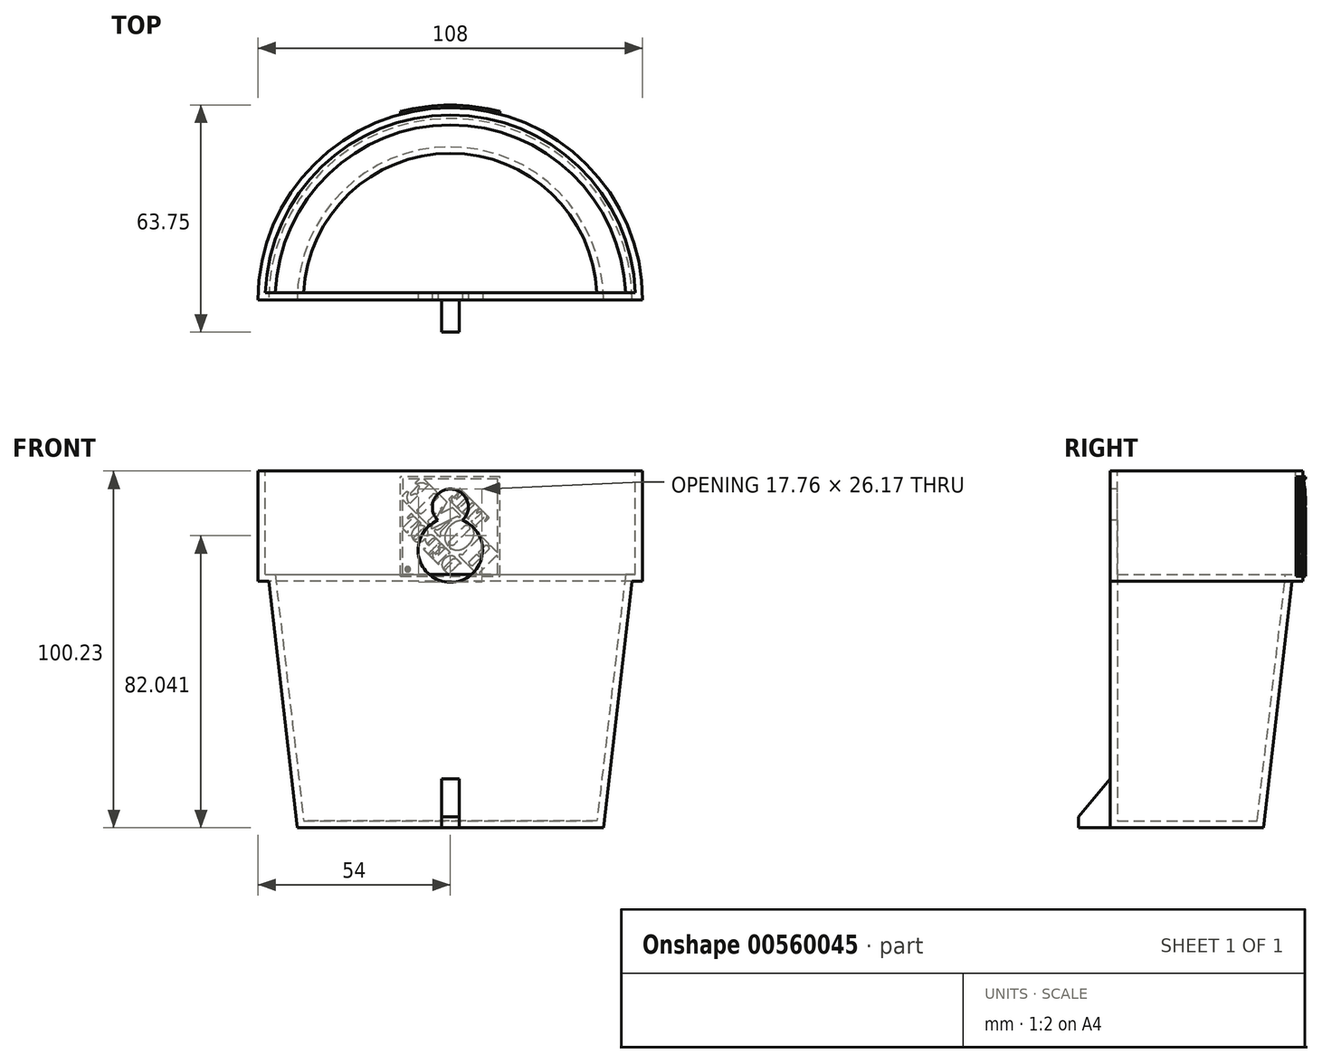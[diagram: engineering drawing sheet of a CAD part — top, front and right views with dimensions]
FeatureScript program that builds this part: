
annotation { "Feature Type Name" : "Feature", "Feature Type Description" : "" }
export const myFeature = defineFeature(function(context is Context, id is Id, definition is map)
    precondition{}
    {
        {
            var Q0;
            Q0=qCreatedBy(makeId("Front.planeOp"),FACE);
            var sketch = newSketch(context, id + "F0", { "sketchPlane" : qUnion([Q0])});
            skLineSegment(sketch, "E0", {"start": v(0, 77.42) * mm, "end": v(-54, 77.42) * mm});
            skLineSegment(sketch, "E1", {"start": v(-54, 77.42) * mm, "end": v(-54, 46.42) * mm});
            skLineSegment(sketch, "E2", {"start": v(0, -22.8) * mm, "end": v(-43, -22.8) * mm});
            skLineSegment(sketch, "E3", {"start": v(-54, 46.42) * mm, "end": v(-51, 46.42) * mm});
            skLineSegment(sketch, "E4", {"start": v(0, 77.42) * mm, "end": v(0, -22.8) * mm});
            skLineSegment(sketch, "E5", {"start": v(-51, 46.42) * mm, "end": v(-43, -22.8) * mm});
            skLineSegment(sketch, "E6.MirrorCS", {"start": v(0, 77.42) * mm, "end": v(54, 77.42) * mm});
            skLineSegment(sketch, "E7.MirrorCS", {"start": v(54, 77.42) * mm, "end": v(54, 46.42) * mm});
            skLineSegment(sketch, "E8.MirrorCS", {"start": v(54, 46.42) * mm, "end": v(51, 46.42) * mm});
            skLineSegment(sketch, "E9.MirrorCS", {"start": v(51, 46.42) * mm, "end": v(43, -22.8) * mm});
            skLineSegment(sketch, "E10.MirrorCS", {"start": v(0, -22.8) * mm, "end": v(43, -22.8) * mm});
            skSolve(sketch);
        }
        {
            var Q0;
            {var subQ0=sQuery(id+"F0.wireOp",EDGE,"E3");Q0=makeQuery(id+"F0.imprint","IMPRINT",FACE,{"disambiguationData":[TD([[makeQuery(id+"F0.imprint","IMPRINT",EDGE,{"derivedFrom":subQ0}),1.0]])]});}
            var Q1;
            {var subQ1=sQuery(id+"F0.wireOp",EDGE,"E0");Q1=makeQuery(id+"F0.imprint","IMPRINT",FACE,{"disambiguationData":[TD([[makeQuery(id+"F0.imprint","IMPRINT",EDGE,{"derivedFrom":subQ1}),1.0]])]});}
            var Q2;
            Q2=makeQuery(id+"F0.imprint","IMPRINT",FACE,{"disambiguationData":[TD([[makeQuery(id+"F0.imprint","IMPRINT",EDGE,{"derivedFrom":sQuery(id+"F0.wireOp",EDGE,"Kfnrekvc-ZjTY-c2iQ-cK4z-hKnBe4uEAVNk")}),1.0]])]});
            var Q3;
            Q3=sQuery(id+"F0.wireOp",EDGE,"E4");
            revolve(context, id + "F1", {"entities" : qUnion([Q0, Q1, Q2]), "axis" : qUnion([Q3]), "revolveType" : RevolveType.ONE_DIRECTION, "angle" : 180 * degree});
        }
        {
            var Q0;
            Q0=makeQuery(id+"FK2OT3XlAi37Aaq_1.splitOp","SPLIT",FACE,{"derivedFrom":makeQuery(id+"F1.opRevolve","SWEPT_FACE",FACE,{"disambiguationData":[OSD([sQuery(id+"F0.wireOp",EDGE,"E0")])]}),"isFromBackBody":true});
            shell(context, id + "F2", {"entities" : qUnion([Q0]), "thickness" : 2 * mm});
        }
        {
            var Q0;
            Q0=qCreatedBy(makeId("Front.planeOp"),FACE);
            var sketch = newSketch(context, id + "F3", { "sketchPlane" : qUnion([Q0])});
            skLineSegment(sketch, "E11.bottom", {"start": v(-2.5, -7.8) * mm, "end": v(2.5, -7.8) * mm});
            skLineSegment(sketch, "E11.top", {"start": v(-2.5, -22.8) * mm, "end": v(2.5, -22.8) * mm});
            skLineSegment(sketch, "E11.left", {"start": v(-2.5, -7.8) * mm, "end": v(-2.5, -22.8) * mm});
            skLineSegment(sketch, "E11.right", {"start": v(2.5, -7.8) * mm, "end": v(2.5, -22.8) * mm});
            skPoint(sketch, "E11.middle", {"position": v(0, -15.3) * mm});
            skSolve(sketch);
        }
        {
            var Q0;
            Q0=qSketchRegion(id+"F3",true);
            extrude(context, id + "F4", {"entities" : qUnion([Q0]), "operationType" : NewBodyOperationType.ADD, "depth" : 9 * mm});
        }
        {
            var Q0;
            Q0=qCreatedBy(makeId("Front.planeOp"),FACE);
            var sketch = newSketch(context, id + "F5", { "sketchPlane" : qUnion([Q0])});
            skCircle(sketch, "E12", {"center": v(0, 67.27) * mm, "radius": 5.05 * mm});
            skCircle(sketch, "E13", {"center": v(0, 55.2) * mm, "radius": 9.05 * mm});
            skSolve(sketch);
        }
        {
            var Q0;
            {var subQ0=sQuery(id+"F5.wireOp",EDGE,"E13");var subQ1=sQuery(id+"F5.wireOp",EDGE,"E12");var subQ2=makeQuery(id+"F5.imprint","INTERSECT",VERTEX,{"disambiguationData":[OD(0.0)],"derivedFrom":[subQ1,subQ0]});Q0=makeQuery(id+"F5.imprint","IMPRINT",FACE,{"disambiguationData":[TD([[makeQuery(id+"F5.imprint","IMPRINT",EDGE,{"disambiguationData":[TD([[subQ2,1.0]])],"derivedFrom":subQ1}),1.0]])]});}
            var Q1;
            {var subQ0=sQuery(id+"F5.wireOp",EDGE,"E13");var subQ1=sQuery(id+"F5.wireOp",EDGE,"E12");var subQ2=makeQuery(id+"F5.imprint","INTERSECT",VERTEX,{"disambiguationData":[OD(0.0)],"derivedFrom":[subQ1,subQ0]});Q1=makeQuery(id+"F5.imprint","IMPRINT",FACE,{"disambiguationData":[TD([[makeQuery(id+"F5.imprint","IMPRINT",EDGE,{"disambiguationData":[TD([[subQ2,-1.0]])],"derivedFrom":subQ1}),-1.0]])]});}
            var Q2;
            {var subQ0=sQuery(id+"F5.wireOp",EDGE,"E13");var subQ1=sQuery(id+"F5.wireOp",EDGE,"E12");var subQ2=makeQuery(id+"F5.imprint","INTERSECT",VERTEX,{"disambiguationData":[OD(0.0)],"derivedFrom":[subQ1,subQ0]});Q2=makeQuery(id+"F5.imprint","IMPRINT",FACE,{"disambiguationData":[TD([[makeQuery(id+"F5.imprint","IMPRINT",EDGE,{"disambiguationData":[TD([[subQ2,-1.0]])],"derivedFrom":subQ1}),1.0]])]});}
            var Q3;
            Q3=sQuery(id+"F5.wireOp",EDGE,"E12");
            var Q4;
            Q4=sQuery(id+"F5.wireOp",EDGE,"E13");
            extrude(context, id + "F6", {"entities" : qUnion([Q0, Q1, Q2]), "operationType" : NewBodyOperationType.REMOVE, "surfaceEntities" : qUnion([Q3, Q4]), "oppositeDirection" : true, "depth" : 10 * mm});
        }
        {
            var Q0;
            Q0=makeQuery(id+"F4.opExtrude","CAP_EDGE",EDGE,{"disambiguationData":[OSD([sQuery(id+"F3.wireOp",EDGE,"E11.bottom")])],"isStart":false});
            chamfer(context, id + "F7", {"entities" : qUnion([Q0]), "chamferType" : ChamferType.OFFSET_ANGLE, "width" : 10 * mm, "oppositeDirection" : false, "angle" : 50 * degree, "tangentPropagation" : true});
        }
        {
            var Q0;
            Q0=makeQuery(id+"F1.opRevolve","SWEPT_BODY",BODY,{"disambiguationData":[OSD([sQuery(id+"F0.wireOp",EDGE,"E0"),sQuery(id+"F0.wireOp",EDGE,"E1"),sQuery(id+"F0.wireOp",EDGE,"E2"),sQuery(id+"F0.wireOp",EDGE,"E3"),sQuery(id+"F0.wireOp",EDGE,"E4"),sQuery(id+"F0.wireOp",EDGE,"E5")])]});
            transform(context, id + "F8", {"entities" : qUnion([Q0]), "transformType" : TransformType.TRANSLATION_3D, "dx" : 0 * mm, "dy" : 0 * mm, "dz" : -7 * mm, "makeCopy" : false});
        }
        {
            var Q0;
            Q0=makeQuery(id+"F2.opShell","OFFSET_FACE",FACE,{"disambiguationData":[OSD([sQuery(id+"F0.wireOp",EDGE,"E0"),sQuery(id+"F0.wireOp",EDGE,"E1"),sQuery(id+"F0.wireOp",EDGE,"E2"),sQuery(id+"F0.wireOp",EDGE,"E3"),sQuery(id+"F0.wireOp",EDGE,"E4"),sQuery(id+"F0.wireOp",EDGE,"E5")])]});
            cPlane(context, id + "F9", {"entities" : qUnion([Q0]), "cplaneType" : CPlaneType.OFFSET, "offset" : 80 * mm, "width" : 150 * mm, "height" : 150 * mm});
        }
        {
            var Q0;
            Q0=qCreatedBy(id+"F9.planeOp",FACE);
            var sketch = newSketch(context, id + "F10", { "sketchPlane" : qUnion([Q0])});
            skLineSegment(sketch, "E14", {"start": v(0.66, 41.55) * mm, "end": v(0.66, 41.55) * mm});
            skLineSegment(sketch, "E15", {"start": v(0.66, 41.55) * mm, "end": v(0.66, 41.54) * mm});
            skLineSegment(sketch, "E16", {"start": v(0.66, 41.54) * mm, "end": v(0.66, 41.55) * mm});
            skLineSegment(sketch, "E17", {"start": v(11.7, 43.25) * mm, "end": v(11.7, 42.39) * mm});
            skLineSegment(sketch, "E18", {"start": v(11.7, 42.39) * mm, "end": v(11.82, 42.39) * mm});
            skLineSegment(sketch, "E19", {"start": v(11.82, 42.39) * mm, "end": v(11.82, 42.76) * mm});
            skLineSegment(sketch, "E20", {"start": v(11.82, 42.76) * mm, "end": v(11.97, 42.76) * mm});
            skLineSegment(sketch, "E21", {"start": v(11.97, 42.76) * mm, "end": v(12.05, 42.63) * mm});
            skLineSegment(sketch, "E22", {"start": v(12.05, 42.63) * mm, "end": v(12.07, 42.6) * mm});
            skLineSegment(sketch, "E23", {"start": v(12.07, 42.6) * mm, "end": v(12.2, 42.4) * mm});
            skLineSegment(sketch, "E24", {"start": v(12.2, 42.4) * mm, "end": v(12.34, 42.39) * mm});
            skLineSegment(sketch, "E25", {"start": v(12.34, 42.39) * mm, "end": v(12.34, 42.4) * mm});
            skLineSegment(sketch, "E26", {"start": v(12.34, 42.4) * mm, "end": v(12.32, 42.42) * mm});
            skLineSegment(sketch, "E27", {"start": v(12.32, 42.42) * mm, "end": v(12.3, 42.45) * mm});
            skLineSegment(sketch, "E28", {"start": v(12.3, 42.45) * mm, "end": v(12.14, 42.7) * mm});
            skLineSegment(sketch, "E29", {"start": v(12.14, 42.7) * mm, "end": v(12.12, 42.73) * mm});
            skLineSegment(sketch, "E30", {"start": v(12.12, 42.73) * mm, "end": v(12.1, 42.76) * mm});
            skLineSegment(sketch, "E31", {"start": v(12.1, 42.76) * mm, "end": v(12.1, 42.77) * mm});
            skLineSegment(sketch, "E32", {"start": v(12.1, 42.77) * mm, "end": v(12.12, 42.77) * mm});
            skLineSegment(sketch, "E33", {"start": v(12.12, 42.77) * mm, "end": v(12.17, 42.78) * mm});
            skLineSegment(sketch, "E34", {"start": v(12.17, 42.78) * mm, "end": v(12.2, 42.8) * mm});
            skLineSegment(sketch, "E35", {"start": v(12.2, 42.8) * mm, "end": v(12.23, 42.82) * mm});
            skLineSegment(sketch, "E36", {"start": v(12.23, 42.82) * mm, "end": v(12.26, 42.84) * mm});
            skLineSegment(sketch, "E37", {"start": v(12.26, 42.84) * mm, "end": v(12.3, 42.87) * mm});
            skLineSegment(sketch, "E38", {"start": v(12.3, 42.87) * mm, "end": v(12.3, 42.9) * mm});
            skLineSegment(sketch, "E39", {"start": v(12.3, 42.9) * mm, "end": v(12.32, 42.95) * mm});
            skLineSegment(sketch, "E40", {"start": v(12.32, 42.95) * mm, "end": v(12.32, 43) * mm});
            skLineSegment(sketch, "E41", {"start": v(12.32, 43) * mm, "end": v(12.32, 43.06) * mm});
            skLineSegment(sketch, "E42", {"start": v(12.32, 43.06) * mm, "end": v(12.31, 43.1) * mm});
            skLineSegment(sketch, "E43", {"start": v(12.31, 43.1) * mm, "end": v(12.3, 43.13) * mm});
            skLineSegment(sketch, "E44", {"start": v(12.3, 43.13) * mm, "end": v(12.28, 43.16) * mm});
            skLineSegment(sketch, "E45", {"start": v(12.28, 43.16) * mm, "end": v(12.26, 43.18) * mm});
            skLineSegment(sketch, "E46", {"start": v(12.26, 43.18) * mm, "end": v(12.23, 43.2) * mm});
            skLineSegment(sketch, "E47", {"start": v(12.23, 43.2) * mm, "end": v(12.2, 43.22) * mm});
            skLineSegment(sketch, "E48", {"start": v(12.2, 43.22) * mm, "end": v(12.15, 43.23) * mm});
            skLineSegment(sketch, "E49", {"start": v(12.15, 43.23) * mm, "end": v(12.1, 43.25) * mm});
            skLineSegment(sketch, "E50", {"start": v(12.1, 43.25) * mm, "end": v(11.7, 43.25) * mm});
            skLineSegment(sketch, "E51", {"start": v(12.1, 42.2) * mm, "end": v(12.16, 42.22) * mm});
            skLineSegment(sketch, "E52", {"start": v(12.16, 42.22) * mm, "end": v(12.2, 42.24) * mm});
            skLineSegment(sketch, "E53", {"start": v(12.2, 42.24) * mm, "end": v(12.28, 42.27) * mm});
            skLineSegment(sketch, "E54", {"start": v(12.28, 42.27) * mm, "end": v(12.35, 42.31) * mm});
            skLineSegment(sketch, "E55", {"start": v(12.35, 42.31) * mm, "end": v(12.37, 42.32) * mm});
            skLineSegment(sketch, "E56", {"start": v(12.37, 42.32) * mm, "end": v(12.37, 42.33) * mm});
            skLineSegment(sketch, "E57", {"start": v(12.37, 42.33) * mm, "end": v(12.4, 42.37) * mm});
            skLineSegment(sketch, "E58", {"start": v(12.4, 42.37) * mm, "end": v(12.47, 42.43) * mm});
            skLineSegment(sketch, "E59", {"start": v(12.47, 42.43) * mm, "end": v(12.48, 42.45) * mm});
            skLineSegment(sketch, "E60", {"start": v(12.48, 42.45) * mm, "end": v(12.48, 42.45) * mm});
            skLineSegment(sketch, "E61", {"start": v(12.48, 42.45) * mm, "end": v(12.49, 42.46) * mm});
            skLineSegment(sketch, "E62", {"start": v(12.49, 42.46) * mm, "end": v(12.55, 42.57) * mm});
            skLineSegment(sketch, "E63", {"start": v(12.55, 42.57) * mm, "end": v(12.55, 42.58) * mm});
            skLineSegment(sketch, "E64", {"start": v(12.55, 42.58) * mm, "end": v(12.56, 42.61) * mm});
            skLineSegment(sketch, "E65", {"start": v(12.56, 42.61) * mm, "end": v(12.57, 42.66) * mm});
            skLineSegment(sketch, "E66", {"start": v(12.57, 42.66) * mm, "end": v(12.58, 42.7) * mm});
            skLineSegment(sketch, "E67", {"start": v(12.58, 42.7) * mm, "end": v(12.59, 42.8) * mm});
            skLineSegment(sketch, "E68", {"start": v(12.59, 42.8) * mm, "end": v(12.58, 42.9) * mm});
            skLineSegment(sketch, "E69", {"start": v(12.58, 42.9) * mm, "end": v(12.58, 42.95) * mm});
            skLineSegment(sketch, "E70", {"start": v(12.58, 42.95) * mm, "end": v(12.57, 43) * mm});
            skLineSegment(sketch, "E71", {"start": v(12.57, 43) * mm, "end": v(12.54, 43.06) * mm});
            skLineSegment(sketch, "E72", {"start": v(12.54, 43.06) * mm, "end": v(12.51, 43.13) * mm});
            skLineSegment(sketch, "E73", {"start": v(12.51, 43.13) * mm, "end": v(12.47, 43.2) * mm});
            skLineSegment(sketch, "E74", {"start": v(12.47, 43.2) * mm, "end": v(12.43, 43.25) * mm});
            skLineSegment(sketch, "E75", {"start": v(12.43, 43.25) * mm, "end": v(12.37, 43.3) * mm});
            skLineSegment(sketch, "E76", {"start": v(12.37, 43.3) * mm, "end": v(12.31, 43.34) * mm});
            skLineSegment(sketch, "E77", {"start": v(12.31, 43.34) * mm, "end": v(12.25, 43.38) * mm});
            skLineSegment(sketch, "E78", {"start": v(12.25, 43.38) * mm, "end": v(12.18, 43.4) * mm});
            skLineSegment(sketch, "E79", {"start": v(12.18, 43.4) * mm, "end": v(12.13, 43.43) * mm});
            skLineSegment(sketch, "E80", {"start": v(12.13, 43.43) * mm, "end": v(12.07, 43.44) * mm});
            skLineSegment(sketch, "E81", {"start": v(12.07, 43.44) * mm, "end": v(12, 43.44) * mm});
            skLineSegment(sketch, "E82", {"start": v(12, 43.44) * mm, "end": v(11.95, 43.44) * mm});
            skLineSegment(sketch, "E83", {"start": v(11.95, 43.44) * mm, "end": v(11.89, 43.44) * mm});
            skLineSegment(sketch, "E84", {"start": v(11.89, 43.44) * mm, "end": v(11.83, 43.43) * mm});
            skLineSegment(sketch, "E85", {"start": v(11.83, 43.43) * mm, "end": v(11.78, 43.41) * mm});
            skLineSegment(sketch, "E86", {"start": v(11.78, 43.41) * mm, "end": v(11.72, 43.39) * mm});
            skLineSegment(sketch, "E87", {"start": v(11.72, 43.39) * mm, "end": v(11.68, 43.37) * mm});
            skLineSegment(sketch, "E88", {"start": v(11.68, 43.37) * mm, "end": v(11.67, 43.37) * mm});
            skLineSegment(sketch, "E89", {"start": v(11.67, 43.37) * mm, "end": v(11.67, 43.37) * mm});
            skLineSegment(sketch, "E90", {"start": v(11.67, 43.37) * mm, "end": v(11.64, 43.34) * mm});
            skLineSegment(sketch, "E91", {"start": v(11.64, 43.34) * mm, "end": v(11.6, 43.31) * mm});
            skLineSegment(sketch, "E92", {"start": v(11.6, 43.31) * mm, "end": v(11.56, 43.28) * mm});
            skLineSegment(sketch, "E93", {"start": v(11.56, 43.28) * mm, "end": v(11.53, 43.25) * mm});
            skLineSegment(sketch, "E94", {"start": v(11.53, 43.25) * mm, "end": v(11.5, 43.21) * mm});
            skLineSegment(sketch, "E95", {"start": v(11.5, 43.21) * mm, "end": v(11.47, 43.17) * mm});
            skLineSegment(sketch, "E96", {"start": v(11.47, 43.17) * mm, "end": v(11.45, 43.13) * mm});
            skLineSegment(sketch, "E97", {"start": v(11.45, 43.13) * mm, "end": v(11.42, 43.09) * mm});
            skLineSegment(sketch, "E98", {"start": v(11.42, 43.09) * mm, "end": v(11.4, 43.04) * mm});
            skLineSegment(sketch, "E99", {"start": v(11.4, 43.04) * mm, "end": v(11.4, 43) * mm});
            skLineSegment(sketch, "E100", {"start": v(11.4, 43) * mm, "end": v(11.38, 42.95) * mm});
            skLineSegment(sketch, "E101", {"start": v(11.38, 42.95) * mm, "end": v(11.37, 42.9) * mm});
            skLineSegment(sketch, "E102", {"start": v(11.37, 42.9) * mm, "end": v(11.37, 42.85) * mm});
            skLineSegment(sketch, "E103", {"start": v(11.37, 42.85) * mm, "end": v(11.37, 42.8) * mm});
            skLineSegment(sketch, "E104", {"start": v(11.37, 42.8) * mm, "end": v(11.37, 42.75) * mm});
            skLineSegment(sketch, "E105", {"start": v(11.37, 42.75) * mm, "end": v(11.38, 42.7) * mm});
            skLineSegment(sketch, "E106", {"start": v(11.38, 42.7) * mm, "end": v(11.39, 42.65) * mm});
            skLineSegment(sketch, "E107", {"start": v(11.39, 42.65) * mm, "end": v(11.4, 42.6) * mm});
            skLineSegment(sketch, "E108", {"start": v(11.4, 42.6) * mm, "end": v(11.43, 42.53) * mm});
            skLineSegment(sketch, "E109", {"start": v(11.43, 42.53) * mm, "end": v(11.46, 42.48) * mm});
            skLineSegment(sketch, "E110", {"start": v(11.46, 42.48) * mm, "end": v(11.5, 42.43) * mm});
            skLineSegment(sketch, "E111", {"start": v(11.5, 42.43) * mm, "end": v(11.53, 42.39) * mm});
            skLineSegment(sketch, "E112", {"start": v(11.53, 42.39) * mm, "end": v(11.58, 42.34) * mm});
            skLineSegment(sketch, "E113", {"start": v(11.58, 42.34) * mm, "end": v(11.62, 42.3) * mm});
            skLineSegment(sketch, "E114", {"start": v(11.62, 42.3) * mm, "end": v(11.68, 42.27) * mm});
            skLineSegment(sketch, "E115", {"start": v(11.68, 42.27) * mm, "end": v(11.72, 42.25) * mm});
            skLineSegment(sketch, "E116", {"start": v(11.72, 42.25) * mm, "end": v(11.77, 42.23) * mm});
            skLineSegment(sketch, "E117", {"start": v(11.77, 42.23) * mm, "end": v(11.82, 42.21) * mm});
            skLineSegment(sketch, "E118", {"start": v(11.82, 42.21) * mm, "end": v(11.86, 42.2) * mm});
            skLineSegment(sketch, "E119", {"start": v(11.86, 42.2) * mm, "end": v(11.92, 42.2) * mm});
            skLineSegment(sketch, "E120", {"start": v(11.92, 42.2) * mm, "end": v(11.99, 42.2) * mm});
            skLineSegment(sketch, "E121", {"start": v(11.99, 42.2) * mm, "end": v(12.05, 42.2) * mm});
            skLineSegment(sketch, "E122", {"start": v(12.05, 42.2) * mm, "end": v(12.1, 42.2) * mm});
            skLineSegment(sketch, "E123", {"start": v(11.82, 42.87) * mm, "end": v(12.09, 42.88) * mm});
            skLineSegment(sketch, "E124", {"start": v(12.09, 42.88) * mm, "end": v(12.1, 42.88) * mm});
            skLineSegment(sketch, "E125", {"start": v(12.1, 42.88) * mm, "end": v(12.14, 42.9) * mm});
            skLineSegment(sketch, "E126", {"start": v(12.14, 42.9) * mm, "end": v(12.16, 42.91) * mm});
            skLineSegment(sketch, "E127", {"start": v(12.16, 42.91) * mm, "end": v(12.17, 42.93) * mm});
            skLineSegment(sketch, "E128", {"start": v(12.17, 42.93) * mm, "end": v(12.18, 42.97) * mm});
            skLineSegment(sketch, "E129", {"start": v(12.18, 42.97) * mm, "end": v(12.19, 43.01) * mm});
            skLineSegment(sketch, "E130", {"start": v(12.19, 43.01) * mm, "end": v(12.18, 43.05) * mm});
            skLineSegment(sketch, "E131", {"start": v(12.18, 43.05) * mm, "end": v(12.17, 43.08) * mm});
            skLineSegment(sketch, "E132", {"start": v(12.17, 43.08) * mm, "end": v(12.14, 43.1) * mm});
            skLineSegment(sketch, "E133", {"start": v(12.14, 43.1) * mm, "end": v(12.11, 43.13) * mm});
            skLineSegment(sketch, "E134", {"start": v(12.11, 43.13) * mm, "end": v(12.09, 43.14) * mm});
            skLineSegment(sketch, "E135", {"start": v(12.09, 43.14) * mm, "end": v(11.82, 43.14) * mm});
            skLineSegment(sketch, "E136", {"start": v(11.82, 43.14) * mm, "end": v(11.82, 42.87) * mm});
            skLineSegment(sketch, "E137", {"start": v(11.82, 42.87) * mm, "end": v(11.82, 42.87) * mm});
            skLineSegment(sketch, "E138", {"start": v(1.57, 42.94) * mm, "end": v(1.82, 42.7) * mm});
            skLineSegment(sketch, "E139", {"start": v(1.82, 42.7) * mm, "end": v(1.83, 42.7) * mm});
            skLineSegment(sketch, "E140", {"start": v(1.83, 42.7) * mm, "end": v(1.93, 42.8) * mm});
            skLineSegment(sketch, "E141", {"start": v(1.93, 42.8) * mm, "end": v(1.93, 42.8) * mm});
            skLineSegment(sketch, "E142", {"start": v(1.93, 42.8) * mm, "end": v(1.96, 42.84) * mm});
            skLineSegment(sketch, "E143", {"start": v(1.96, 42.84) * mm, "end": v(2.02, 42.92) * mm});
            skLineSegment(sketch, "E144", {"start": v(2.02, 42.92) * mm, "end": v(2.06, 42.97) * mm});
            skLineSegment(sketch, "E145", {"start": v(2.06, 42.97) * mm, "end": v(2.06, 42.98) * mm});
            skLineSegment(sketch, "E146", {"start": v(2.06, 42.98) * mm, "end": v(2.06, 42.98) * mm});
            skLineSegment(sketch, "E147", {"start": v(2.06, 42.98) * mm, "end": v(2.07, 42.98) * mm});
            skLineSegment(sketch, "E148", {"start": v(2.07, 42.98) * mm, "end": v(2.1, 43.04) * mm});
            skLineSegment(sketch, "E149", {"start": v(2.1, 43.04) * mm, "end": v(2.16, 43.14) * mm});
            skLineSegment(sketch, "E150", {"start": v(2.16, 43.14) * mm, "end": v(2.2, 43.24) * mm});
            skLineSegment(sketch, "E151", {"start": v(2.2, 43.24) * mm, "end": v(2.25, 43.33) * mm});
            skLineSegment(sketch, "E152", {"start": v(2.25, 43.33) * mm, "end": v(2.29, 43.43) * mm});
            skLineSegment(sketch, "E153", {"start": v(2.29, 43.43) * mm, "end": v(2.32, 43.53) * mm});
            skLineSegment(sketch, "E154", {"start": v(2.32, 43.53) * mm, "end": v(2.35, 43.64) * mm});
            skLineSegment(sketch, "E155", {"start": v(2.35, 43.64) * mm, "end": v(2.37, 43.74) * mm});
            skLineSegment(sketch, "E156", {"start": v(2.37, 43.74) * mm, "end": v(2.38, 43.85) * mm});
            skLineSegment(sketch, "E157", {"start": v(2.38, 43.85) * mm, "end": v(2.4, 43.92) * mm});
            skLineSegment(sketch, "E158", {"start": v(2.4, 43.92) * mm, "end": v(2.4, 44.17) * mm});
            skLineSegment(sketch, "E159", {"start": v(2.4, 44.17) * mm, "end": v(2.4, 44.25) * mm});
            skLineSegment(sketch, "E160", {"start": v(2.4, 44.25) * mm, "end": v(2.37, 44.4) * mm});
            skLineSegment(sketch, "E161", {"start": v(2.37, 44.4) * mm, "end": v(2.35, 44.56) * mm});
            skLineSegment(sketch, "E162", {"start": v(2.35, 44.56) * mm, "end": v(2.3, 44.7) * mm});
            skLineSegment(sketch, "E163", {"start": v(2.3, 44.7) * mm, "end": v(2.26, 44.85) * mm});
            skLineSegment(sketch, "E164", {"start": v(2.26, 44.85) * mm, "end": v(2.2, 45) * mm});
            skLineSegment(sketch, "E165", {"start": v(2.2, 45) * mm, "end": v(2.12, 45.13) * mm});
            skLineSegment(sketch, "E166", {"start": v(2.12, 45.13) * mm, "end": v(2.04, 45.27) * mm});
            skLineSegment(sketch, "E167", {"start": v(2.04, 45.27) * mm, "end": v(1.94, 45.4) * mm});
            skLineSegment(sketch, "E168", {"start": v(1.94, 45.4) * mm, "end": v(1.9, 45.47) * mm});
            skLineSegment(sketch, "E169", {"start": v(1.9, 45.47) * mm, "end": v(1.87, 45.5) * mm});
            skLineSegment(sketch, "E170", {"start": v(1.87, 45.5) * mm, "end": v(1.82, 45.56) * mm});
            skLineSegment(sketch, "E171", {"start": v(1.82, 45.56) * mm, "end": v(1.79, 45.6) * mm});
            skLineSegment(sketch, "E172", {"start": v(1.79, 45.6) * mm, "end": v(1.72, 45.66) * mm});
            skLineSegment(sketch, "E173", {"start": v(1.72, 45.66) * mm, "end": v(1.63, 45.75) * mm});
            skLineSegment(sketch, "E174", {"start": v(1.63, 45.75) * mm, "end": v(1.53, 45.84) * mm});
            skLineSegment(sketch, "E175", {"start": v(1.53, 45.84) * mm, "end": v(1.43, 45.93) * mm});
            skLineSegment(sketch, "E176", {"start": v(1.43, 45.93) * mm, "end": v(1.32, 46) * mm});
            skLineSegment(sketch, "E177", {"start": v(1.32, 46) * mm, "end": v(1.21, 46.1) * mm});
            skLineSegment(sketch, "E178", {"start": v(1.21, 46.1) * mm, "end": v(1.1, 46.17) * mm});
            skLineSegment(sketch, "E179", {"start": v(1.1, 46.17) * mm, "end": v(1, 46.23) * mm});
            skLineSegment(sketch, "E180", {"start": v(1, 46.23) * mm, "end": v(0.88, 46.3) * mm});
            skLineSegment(sketch, "E181", {"start": v(0.88, 46.3) * mm, "end": v(0.82, 46.33) * mm});
            skLineSegment(sketch, "E182", {"start": v(0.82, 46.33) * mm, "end": v(0.82, 46.33) * mm});
            skLineSegment(sketch, "E183", {"start": v(0.82, 46.33) * mm, "end": v(0.77, 46.35) * mm});
            skLineSegment(sketch, "E184", {"start": v(0.77, 46.35) * mm, "end": v(0.68, 46.4) * mm});
            skLineSegment(sketch, "E185", {"start": v(0.68, 46.4) * mm, "end": v(0.58, 46.44) * mm});
            skLineSegment(sketch, "E186", {"start": v(0.58, 46.44) * mm, "end": v(0.49, 46.47) * mm});
            skLineSegment(sketch, "E187", {"start": v(0.49, 46.47) * mm, "end": v(0.4, 46.5) * mm});
            skLineSegment(sketch, "E188", {"start": v(0.4, 46.5) * mm, "end": v(0.3, 46.53) * mm});
            skLineSegment(sketch, "E189", {"start": v(0.3, 46.53) * mm, "end": v(0.2, 46.55) * mm});
            skLineSegment(sketch, "E190", {"start": v(0.2, 46.55) * mm, "end": v(0.1, 46.56) * mm});
            skLineSegment(sketch, "E191", {"start": v(0.1, 46.56) * mm, "end": v(0, 46.57) * mm});
            skLineSegment(sketch, "E192", {"start": v(0, 46.57) * mm, "end": v(-0.06, 46.58) * mm});
            skLineSegment(sketch, "E193", {"start": v(-0.06, 46.58) * mm, "end": v(-0.34, 46.57) * mm});
            skLineSegment(sketch, "E194", {"start": v(-0.34, 46.57) * mm, "end": v(-0.41, 46.56) * mm});
            skLineSegment(sketch, "E195", {"start": v(-0.41, 46.56) * mm, "end": v(-0.52, 46.54) * mm});
            skLineSegment(sketch, "E196", {"start": v(-0.52, 46.54) * mm, "end": v(-0.62, 46.52) * mm});
            skLineSegment(sketch, "E197", {"start": v(-0.62, 46.52) * mm, "end": v(-0.72, 46.49) * mm});
            skLineSegment(sketch, "E198", {"start": v(-0.72, 46.49) * mm, "end": v(-0.82, 46.45) * mm});
            skLineSegment(sketch, "E199", {"start": v(-0.82, 46.45) * mm, "end": v(-0.91, 46.4) * mm});
            skLineSegment(sketch, "E200", {"start": v(-0.91, 46.4) * mm, "end": v(-1, 46.36) * mm});
            skLineSegment(sketch, "E201", {"start": v(-1, 46.36) * mm, "end": v(-1.1, 46.3) * mm});
            skLineSegment(sketch, "E202", {"start": v(-1.1, 46.3) * mm, "end": v(-1.2, 46.25) * mm});
            skLineSegment(sketch, "E203", {"start": v(-1.2, 46.25) * mm, "end": v(-1.23, 46.22) * mm});
            skLineSegment(sketch, "E204", {"start": v(-1.23, 46.22) * mm, "end": v(-1.27, 46.19) * mm});
            skLineSegment(sketch, "E205", {"start": v(-1.27, 46.19) * mm, "end": v(-1.36, 46.11) * mm});
            skLineSegment(sketch, "E206", {"start": v(-1.36, 46.11) * mm, "end": v(-1.45, 46.03) * mm});
            skLineSegment(sketch, "E207", {"start": v(-1.45, 46.03) * mm, "end": v(-1.48, 46) * mm});
            skLineSegment(sketch, "E208", {"start": v(-1.48, 46) * mm, "end": v(-1.23, 45.74) * mm});
            skLineSegment(sketch, "E209", {"start": v(-1.23, 45.74) * mm, "end": v(-1.2, 45.77) * mm});
            skLineSegment(sketch, "E210", {"start": v(-1.2, 45.77) * mm, "end": v(-1.13, 45.8) * mm});
            skLineSegment(sketch, "E211", {"start": v(-1.13, 45.8) * mm, "end": v(-1.07, 45.83) * mm});
            skLineSegment(sketch, "E212", {"start": v(-1.07, 45.83) * mm, "end": v(-1, 45.84) * mm});
            skLineSegment(sketch, "E213", {"start": v(-1, 45.84) * mm, "end": v(-0.94, 45.84) * mm});
            skLineSegment(sketch, "E214", {"start": v(-0.94, 45.84) * mm, "end": v(-0.87, 45.83) * mm});
            skLineSegment(sketch, "E215", {"start": v(-0.87, 45.83) * mm, "end": v(-0.8, 45.8) * mm});
            skLineSegment(sketch, "E216", {"start": v(-0.8, 45.8) * mm, "end": v(-0.73, 45.77) * mm});
            skLineSegment(sketch, "E217", {"start": v(-0.73, 45.77) * mm, "end": v(-0.65, 45.71) * mm});
            skLineSegment(sketch, "E218", {"start": v(-0.65, 45.71) * mm, "end": v(-0.59, 45.67) * mm});
            skLineSegment(sketch, "E219", {"start": v(-0.59, 45.67) * mm, "end": v(1.47, 43.6) * mm});
            skLineSegment(sketch, "E220", {"start": v(1.47, 43.6) * mm, "end": v(1.5, 43.59) * mm});
            skLineSegment(sketch, "E221", {"start": v(1.5, 43.59) * mm, "end": v(1.55, 43.51) * mm});
            skLineSegment(sketch, "E222", {"start": v(1.55, 43.51) * mm, "end": v(1.59, 43.47) * mm});
            skLineSegment(sketch, "E223", {"start": v(1.59, 43.47) * mm, "end": v(1.59, 43.46) * mm});
            skLineSegment(sketch, "E224", {"start": v(1.59, 43.46) * mm, "end": v(1.6, 43.46) * mm});
            skLineSegment(sketch, "E225", {"start": v(1.6, 43.46) * mm, "end": v(1.6, 43.46) * mm});
            skLineSegment(sketch, "E226", {"start": v(1.6, 43.46) * mm, "end": v(1.61, 43.42) * mm});
            skLineSegment(sketch, "E227", {"start": v(1.61, 43.42) * mm, "end": v(1.64, 43.36) * mm});
            skLineSegment(sketch, "E228", {"start": v(1.64, 43.36) * mm, "end": v(1.66, 43.3) * mm});
            skLineSegment(sketch, "E229", {"start": v(1.66, 43.3) * mm, "end": v(1.67, 43.25) * mm});
            skLineSegment(sketch, "E230", {"start": v(1.67, 43.25) * mm, "end": v(1.67, 43.2) * mm});
            skLineSegment(sketch, "E231", {"start": v(1.67, 43.2) * mm, "end": v(1.66, 43.14) * mm});
            skLineSegment(sketch, "E232", {"start": v(1.66, 43.14) * mm, "end": v(1.65, 43.08) * mm});
            skLineSegment(sketch, "E233", {"start": v(1.65, 43.08) * mm, "end": v(1.62, 43.03) * mm});
            skLineSegment(sketch, "E234", {"start": v(1.62, 43.03) * mm, "end": v(1.6, 42.97) * mm});
            skLineSegment(sketch, "E235", {"start": v(1.6, 42.97) * mm, "end": v(1.57, 42.94) * mm});
            skLineSegment(sketch, "E236", {"start": v(11.84, 42.08) * mm, "end": v(11.9, 42.07) * mm});
            skLineSegment(sketch, "E237", {"start": v(11.9, 42.07) * mm, "end": v(12, 42.07) * mm});
            skLineSegment(sketch, "E238", {"start": v(12, 42.07) * mm, "end": v(12.1, 42.08) * mm});
            skLineSegment(sketch, "E239", {"start": v(12.1, 42.08) * mm, "end": v(12.14, 42.09) * mm});
            skLineSegment(sketch, "E240", {"start": v(12.14, 42.09) * mm, "end": v(12.2, 42.1) * mm});
            skLineSegment(sketch, "E241", {"start": v(12.2, 42.1) * mm, "end": v(12.25, 42.12) * mm});
            skLineSegment(sketch, "E242", {"start": v(12.25, 42.12) * mm, "end": v(12.3, 42.14) * mm});
            skLineSegment(sketch, "E243", {"start": v(12.3, 42.14) * mm, "end": v(12.35, 42.17) * mm});
            skLineSegment(sketch, "E244", {"start": v(12.35, 42.17) * mm, "end": v(12.4, 42.2) * mm});
            skLineSegment(sketch, "E245", {"start": v(12.4, 42.2) * mm, "end": v(12.44, 42.23) * mm});
            skLineSegment(sketch, "E246", {"start": v(12.44, 42.23) * mm, "end": v(12.49, 42.26) * mm});
            skLineSegment(sketch, "E247", {"start": v(12.49, 42.26) * mm, "end": v(12.53, 42.3) * mm});
            skLineSegment(sketch, "E248", {"start": v(12.53, 42.3) * mm, "end": v(12.56, 42.34) * mm});
            skLineSegment(sketch, "E249", {"start": v(12.56, 42.34) * mm, "end": v(12.6, 42.38) * mm});
            skLineSegment(sketch, "E250", {"start": v(12.6, 42.38) * mm, "end": v(12.63, 42.43) * mm});
            skLineSegment(sketch, "E251", {"start": v(12.63, 42.43) * mm, "end": v(12.65, 42.48) * mm});
            skLineSegment(sketch, "E252", {"start": v(12.65, 42.48) * mm, "end": v(12.68, 42.53) * mm});
            skLineSegment(sketch, "E253", {"start": v(12.68, 42.53) * mm, "end": v(12.7, 42.58) * mm});
            skLineSegment(sketch, "E254", {"start": v(12.7, 42.58) * mm, "end": v(12.71, 42.63) * mm});
            skLineSegment(sketch, "E255", {"start": v(12.71, 42.63) * mm, "end": v(12.73, 42.69) * mm});
            skLineSegment(sketch, "E256", {"start": v(12.73, 42.69) * mm, "end": v(12.73, 42.75) * mm});
            skLineSegment(sketch, "E257", {"start": v(12.73, 42.75) * mm, "end": v(12.73, 42.82) * mm});
            skLineSegment(sketch, "E258", {"start": v(12.73, 42.82) * mm, "end": v(12.73, 42.89) * mm});
            skLineSegment(sketch, "E259", {"start": v(12.73, 42.89) * mm, "end": v(12.73, 42.95) * mm});
            skLineSegment(sketch, "E260", {"start": v(12.73, 42.95) * mm, "end": v(12.71, 43) * mm});
            skLineSegment(sketch, "E261", {"start": v(12.71, 43) * mm, "end": v(12.7, 43.06) * mm});
            skLineSegment(sketch, "E262", {"start": v(12.7, 43.06) * mm, "end": v(12.67, 43.12) * mm});
            skLineSegment(sketch, "E263", {"start": v(12.67, 43.12) * mm, "end": v(12.65, 43.17) * mm});
            skLineSegment(sketch, "E264", {"start": v(12.65, 43.17) * mm, "end": v(12.62, 43.22) * mm});
            skLineSegment(sketch, "E265", {"start": v(12.62, 43.22) * mm, "end": v(12.58, 43.27) * mm});
            skLineSegment(sketch, "E266", {"start": v(12.58, 43.27) * mm, "end": v(12.55, 43.32) * mm});
            skLineSegment(sketch, "E267", {"start": v(12.55, 43.32) * mm, "end": v(12.5, 43.36) * mm});
            skLineSegment(sketch, "E268", {"start": v(12.5, 43.36) * mm, "end": v(12.46, 43.4) * mm});
            skLineSegment(sketch, "E269", {"start": v(12.46, 43.4) * mm, "end": v(12.42, 43.43) * mm});
            skLineSegment(sketch, "E270", {"start": v(12.42, 43.43) * mm, "end": v(12.38, 43.45) * mm});
            skLineSegment(sketch, "E271", {"start": v(12.38, 43.45) * mm, "end": v(12.33, 43.48) * mm});
            skLineSegment(sketch, "E272", {"start": v(12.33, 43.48) * mm, "end": v(12.29, 43.5) * mm});
            skLineSegment(sketch, "E273", {"start": v(12.29, 43.5) * mm, "end": v(12.24, 43.52) * mm});
            skLineSegment(sketch, "E274", {"start": v(12.24, 43.52) * mm, "end": v(12.19, 43.54) * mm});
            skLineSegment(sketch, "E275", {"start": v(12.19, 43.54) * mm, "end": v(12.13, 43.55) * mm});
            skLineSegment(sketch, "E276", {"start": v(12.13, 43.55) * mm, "end": v(12.07, 43.56) * mm});
            skLineSegment(sketch, "E277", {"start": v(12.07, 43.56) * mm, "end": v(12, 43.57) * mm});
            skLineSegment(sketch, "E278", {"start": v(12, 43.57) * mm, "end": v(11.94, 43.56) * mm});
            skLineSegment(sketch, "E279", {"start": v(11.94, 43.56) * mm, "end": v(11.88, 43.56) * mm});
            skLineSegment(sketch, "E280", {"start": v(11.88, 43.56) * mm, "end": v(11.81, 43.55) * mm});
            skLineSegment(sketch, "E281", {"start": v(11.81, 43.55) * mm, "end": v(11.75, 43.53) * mm});
            skLineSegment(sketch, "E282", {"start": v(11.75, 43.53) * mm, "end": v(11.7, 43.5) * mm});
            skLineSegment(sketch, "E283", {"start": v(11.7, 43.5) * mm, "end": v(11.63, 43.48) * mm});
            skLineSegment(sketch, "E284", {"start": v(11.63, 43.48) * mm, "end": v(11.56, 43.44) * mm});
            skLineSegment(sketch, "E285", {"start": v(11.56, 43.44) * mm, "end": v(11.49, 43.4) * mm});
            skLineSegment(sketch, "E286", {"start": v(11.49, 43.4) * mm, "end": v(11.43, 43.34) * mm});
            skLineSegment(sketch, "E287", {"start": v(11.43, 43.34) * mm, "end": v(11.37, 43.27) * mm});
            skLineSegment(sketch, "E288", {"start": v(11.37, 43.27) * mm, "end": v(11.33, 43.2) * mm});
            skLineSegment(sketch, "E289", {"start": v(11.33, 43.2) * mm, "end": v(11.29, 43.13) * mm});
            skLineSegment(sketch, "E290", {"start": v(11.29, 43.13) * mm, "end": v(11.26, 43.05) * mm});
            skLineSegment(sketch, "E291", {"start": v(11.26, 43.05) * mm, "end": v(11.23, 42.97) * mm});
            skLineSegment(sketch, "E292", {"start": v(11.23, 42.97) * mm, "end": v(11.22, 42.92) * mm});
            skLineSegment(sketch, "E293", {"start": v(11.22, 42.92) * mm, "end": v(11.22, 42.71) * mm});
            skLineSegment(sketch, "E294", {"start": v(11.22, 42.71) * mm, "end": v(11.23, 42.67) * mm});
            skLineSegment(sketch, "E295", {"start": v(11.23, 42.67) * mm, "end": v(11.25, 42.61) * mm});
            skLineSegment(sketch, "E296", {"start": v(11.25, 42.61) * mm, "end": v(11.27, 42.56) * mm});
            skLineSegment(sketch, "E297", {"start": v(11.27, 42.56) * mm, "end": v(11.29, 42.51) * mm});
            skLineSegment(sketch, "E298", {"start": v(11.29, 42.51) * mm, "end": v(11.3, 42.47) * mm});
            skLineSegment(sketch, "E299", {"start": v(11.3, 42.47) * mm, "end": v(11.34, 42.42) * mm});
            skLineSegment(sketch, "E300", {"start": v(11.34, 42.42) * mm, "end": v(11.37, 42.38) * mm});
            skLineSegment(sketch, "E301", {"start": v(11.37, 42.38) * mm, "end": v(11.4, 42.33) * mm});
            skLineSegment(sketch, "E302", {"start": v(11.4, 42.33) * mm, "end": v(11.44, 42.3) * mm});
            skLineSegment(sketch, "E303", {"start": v(11.44, 42.3) * mm, "end": v(11.48, 42.25) * mm});
            skLineSegment(sketch, "E304", {"start": v(11.48, 42.25) * mm, "end": v(11.53, 42.22) * mm});
            skLineSegment(sketch, "E305", {"start": v(11.53, 42.22) * mm, "end": v(11.57, 42.19) * mm});
            skLineSegment(sketch, "E306", {"start": v(11.57, 42.19) * mm, "end": v(11.62, 42.16) * mm});
            skLineSegment(sketch, "E307", {"start": v(11.62, 42.16) * mm, "end": v(11.67, 42.13) * mm});
            skLineSegment(sketch, "E308", {"start": v(11.67, 42.13) * mm, "end": v(11.73, 42.11) * mm});
            skLineSegment(sketch, "E309", {"start": v(11.73, 42.11) * mm, "end": v(11.78, 42.1) * mm});
            skLineSegment(sketch, "E310", {"start": v(11.78, 42.1) * mm, "end": v(11.84, 42.08) * mm});
            skLineSegment(sketch, "E311", {"start": v(4.6, 45.96) * mm, "end": v(4.84, 45.71) * mm});
            skLineSegment(sketch, "E312", {"start": v(4.84, 45.71) * mm, "end": v(4.85, 45.71) * mm});
            skLineSegment(sketch, "E313", {"start": v(4.85, 45.71) * mm, "end": v(5.86, 46.72) * mm});
            skLineSegment(sketch, "E314", {"start": v(5.86, 46.72) * mm, "end": v(4.92, 47.66) * mm});
            skLineSegment(sketch, "E315", {"start": v(4.92, 47.66) * mm, "end": v(4.9, 47.67) * mm});
            skLineSegment(sketch, "E316", {"start": v(4.9, 47.67) * mm, "end": v(4.85, 47.69) * mm});
            skLineSegment(sketch, "E317", {"start": v(4.85, 47.69) * mm, "end": v(4.8, 47.69) * mm});
            skLineSegment(sketch, "E318", {"start": v(4.8, 47.69) * mm, "end": v(4.76, 47.68) * mm});
            skLineSegment(sketch, "E319", {"start": v(4.76, 47.68) * mm, "end": v(4.72, 47.65) * mm});
            skLineSegment(sketch, "E320", {"start": v(4.72, 47.65) * mm, "end": v(4.7, 47.63) * mm});
            skLineSegment(sketch, "E321", {"start": v(4.7, 47.63) * mm, "end": v(4.68, 47.6) * mm});
            skLineSegment(sketch, "E322", {"start": v(4.68, 47.6) * mm, "end": v(4.67, 47.58) * mm});
            skLineSegment(sketch, "E323", {"start": v(4.67, 47.58) * mm, "end": v(4.66, 47.56) * mm});
            skLineSegment(sketch, "E324", {"start": v(4.66, 47.56) * mm, "end": v(4.66, 47.53) * mm});
            skLineSegment(sketch, "E325", {"start": v(4.66, 47.53) * mm, "end": v(4.66, 47.5) * mm});
            skLineSegment(sketch, "E326", {"start": v(4.66, 47.5) * mm, "end": v(4.66, 47.47) * mm});
            skLineSegment(sketch, "E327", {"start": v(4.66, 47.47) * mm, "end": v(4.67, 47.43) * mm});
            skLineSegment(sketch, "E328", {"start": v(4.67, 47.43) * mm, "end": v(4.72, 47.31) * mm});
            skLineSegment(sketch, "E329", {"start": v(4.72, 47.31) * mm, "end": v(4.76, 47.21) * mm});
            skLineSegment(sketch, "E330", {"start": v(4.76, 47.21) * mm, "end": v(4.8, 47.11) * mm});
            skLineSegment(sketch, "E331", {"start": v(4.8, 47.11) * mm, "end": v(4.82, 47.01) * mm});
            skLineSegment(sketch, "E332", {"start": v(4.82, 47.01) * mm, "end": v(4.84, 46.91) * mm});
            skLineSegment(sketch, "E333", {"start": v(4.84, 46.91) * mm, "end": v(4.85, 46.85) * mm});
            skLineSegment(sketch, "E334", {"start": v(4.85, 46.85) * mm, "end": v(4.85, 46.6) * mm});
            skLineSegment(sketch, "E335", {"start": v(4.85, 46.6) * mm, "end": v(4.84, 46.54) * mm});
            skLineSegment(sketch, "E336", {"start": v(4.84, 46.54) * mm, "end": v(4.82, 46.43) * mm});
            skLineSegment(sketch, "E337", {"start": v(4.82, 46.43) * mm, "end": v(4.79, 46.32) * mm});
            skLineSegment(sketch, "E338", {"start": v(4.79, 46.32) * mm, "end": v(4.75, 46.22) * mm});
            skLineSegment(sketch, "E339", {"start": v(4.75, 46.22) * mm, "end": v(4.7, 46.13) * mm});
            skLineSegment(sketch, "E340", {"start": v(4.7, 46.13) * mm, "end": v(4.68, 46.09) * mm});
            skLineSegment(sketch, "E341", {"start": v(4.68, 46.09) * mm, "end": v(4.68, 46.09) * mm});
            skLineSegment(sketch, "E342", {"start": v(4.68, 46.09) * mm, "end": v(4.68, 46.08) * mm});
            skLineSegment(sketch, "E343", {"start": v(4.68, 46.08) * mm, "end": v(4.67, 46.08) * mm});
            skLineSegment(sketch, "E344", {"start": v(4.67, 46.08) * mm, "end": v(4.6, 45.97) * mm});
            skLineSegment(sketch, "E345", {"start": v(4.6, 45.97) * mm, "end": v(4.6, 45.96) * mm});
            skLineSegment(sketch, "E346", {"start": v(-1.23, 45.77) * mm, "end": v(-1.23, 45.77) * mm});
            skLineSegment(sketch, "E347", {"start": v(-3.36, 46.87) * mm, "end": v(-3.36, 46.87) * mm});
            skLineSegment(sketch, "E348", {"start": v(3.25, 44.27) * mm, "end": v(3.27, 44.26) * mm});
            skLineSegment(sketch, "E349", {"start": v(3.27, 44.26) * mm, "end": v(3.3, 44.26) * mm});
            skLineSegment(sketch, "E350", {"start": v(3.3, 44.26) * mm, "end": v(3.33, 44.26) * mm});
            skLineSegment(sketch, "E351", {"start": v(3.33, 44.26) * mm, "end": v(3.36, 44.27) * mm});
            skLineSegment(sketch, "E352", {"start": v(3.36, 44.27) * mm, "end": v(3.4, 44.29) * mm});
            skLineSegment(sketch, "E353", {"start": v(3.4, 44.29) * mm, "end": v(3.43, 44.3) * mm});
            skLineSegment(sketch, "E354", {"start": v(3.43, 44.3) * mm, "end": v(3.46, 44.32) * mm});
            skLineSegment(sketch, "E355", {"start": v(3.46, 44.32) * mm, "end": v(4.64, 45.5) * mm});
            skLineSegment(sketch, "E356", {"start": v(4.64, 45.5) * mm, "end": v(1.34, 48.82) * mm});
            skLineSegment(sketch, "E357", {"start": v(1.34, 48.82) * mm, "end": v(0.14, 47.62) * mm});
            skLineSegment(sketch, "E358", {"start": v(0.14, 47.62) * mm, "end": v(0.14, 47.61) * mm});
            skLineSegment(sketch, "E359", {"start": v(0.14, 47.61) * mm, "end": v(0.14, 47.6) * mm});
            skLineSegment(sketch, "E360", {"start": v(0.14, 47.6) * mm, "end": v(0.14, 47.6) * mm});
            skLineSegment(sketch, "E361", {"start": v(0.14, 47.6) * mm, "end": v(0.13, 47.6) * mm});
            skLineSegment(sketch, "E362", {"start": v(0.13, 47.6) * mm, "end": v(0.1, 47.56) * mm});
            skLineSegment(sketch, "E363", {"start": v(0.1, 47.56) * mm, "end": v(0.1, 47.51) * mm});
            skLineSegment(sketch, "E364", {"start": v(0.1, 47.51) * mm, "end": v(0.09, 47.47) * mm});
            skLineSegment(sketch, "E365", {"start": v(0.09, 47.47) * mm, "end": v(0.1, 47.42) * mm});
            skLineSegment(sketch, "E366", {"start": v(0.1, 47.42) * mm, "end": v(0.1, 47.4) * mm});
            skLineSegment(sketch, "E367", {"start": v(0.1, 47.4) * mm, "end": v(0.1, 47.4) * mm});
            skLineSegment(sketch, "E368", {"start": v(0.1, 47.4) * mm, "end": v(0.11, 47.4) * mm});
            skLineSegment(sketch, "E369", {"start": v(0.11, 47.4) * mm, "end": v(0.11, 47.4) * mm});
            skLineSegment(sketch, "E370", {"start": v(0.11, 47.4) * mm, "end": v(0.12, 47.38) * mm});
            skLineSegment(sketch, "E371", {"start": v(0.12, 47.38) * mm, "end": v(0.14, 47.35) * mm});
            skLineSegment(sketch, "E372", {"start": v(0.14, 47.35) * mm, "end": v(0.17, 47.33) * mm});
            skLineSegment(sketch, "E373", {"start": v(0.17, 47.33) * mm, "end": v(0.2, 47.3) * mm});
            skLineSegment(sketch, "E374", {"start": v(0.2, 47.3) * mm, "end": v(0.24, 47.3) * mm});
            skLineSegment(sketch, "E375", {"start": v(0.24, 47.3) * mm, "end": v(0.28, 47.3) * mm});
            skLineSegment(sketch, "E376", {"start": v(0.28, 47.3) * mm, "end": v(0.32, 47.31) * mm});
            skLineSegment(sketch, "E377", {"start": v(0.32, 47.31) * mm, "end": v(0.38, 47.34) * mm});
            skLineSegment(sketch, "E378", {"start": v(0.38, 47.34) * mm, "end": v(0.45, 47.37) * mm});
            skLineSegment(sketch, "E379", {"start": v(0.45, 47.37) * mm, "end": v(0.48, 47.38) * mm});
            skLineSegment(sketch, "E380", {"start": v(0.48, 47.38) * mm, "end": v(0.52, 47.39) * mm});
            skLineSegment(sketch, "E381", {"start": v(0.52, 47.39) * mm, "end": v(0.55, 47.39) * mm});
            skLineSegment(sketch, "E382", {"start": v(0.55, 47.39) * mm, "end": v(0.58, 47.38) * mm});
            skLineSegment(sketch, "E383", {"start": v(0.58, 47.38) * mm, "end": v(0.62, 47.36) * mm});
            skLineSegment(sketch, "E384", {"start": v(0.62, 47.36) * mm, "end": v(0.64, 47.34) * mm});
            skLineSegment(sketch, "E385", {"start": v(0.64, 47.34) * mm, "end": v(3.19, 44.8) * mm});
            skLineSegment(sketch, "E386", {"start": v(3.19, 44.8) * mm, "end": v(3.2, 44.77) * mm});
            skLineSegment(sketch, "E387", {"start": v(3.2, 44.77) * mm, "end": v(3.2, 44.75) * mm});
            skLineSegment(sketch, "E388", {"start": v(3.2, 44.75) * mm, "end": v(3.21, 44.72) * mm});
            skLineSegment(sketch, "E389", {"start": v(3.21, 44.72) * mm, "end": v(3.22, 44.7) * mm});
            skLineSegment(sketch, "E390", {"start": v(3.22, 44.7) * mm, "end": v(3.21, 44.67) * mm});
            skLineSegment(sketch, "E391", {"start": v(3.21, 44.67) * mm, "end": v(3.2, 44.61) * mm});
            skLineSegment(sketch, "E392", {"start": v(3.2, 44.61) * mm, "end": v(3.16, 44.53) * mm});
            skLineSegment(sketch, "E393", {"start": v(3.16, 44.53) * mm, "end": v(3.14, 44.5) * mm});
            skLineSegment(sketch, "E394", {"start": v(3.14, 44.5) * mm, "end": v(3.13, 44.46) * mm});
            skLineSegment(sketch, "E395", {"start": v(3.13, 44.46) * mm, "end": v(3.13, 44.43) * mm});
            skLineSegment(sketch, "E396", {"start": v(3.13, 44.43) * mm, "end": v(3.13, 44.4) * mm});
            skLineSegment(sketch, "E397", {"start": v(3.13, 44.4) * mm, "end": v(3.14, 44.37) * mm});
            skLineSegment(sketch, "E398", {"start": v(3.14, 44.37) * mm, "end": v(3.15, 44.35) * mm});
            skLineSegment(sketch, "E399", {"start": v(3.15, 44.35) * mm, "end": v(3.17, 44.32) * mm});
            skLineSegment(sketch, "E400", {"start": v(3.17, 44.32) * mm, "end": v(3.19, 44.3) * mm});
            skLineSegment(sketch, "E401", {"start": v(3.19, 44.3) * mm, "end": v(3.22, 44.28) * mm});
            skLineSegment(sketch, "E402", {"start": v(3.22, 44.28) * mm, "end": v(3.25, 44.27) * mm});
            skLineSegment(sketch, "E403", {"start": v(-5.16, 44.02) * mm, "end": v(-5.1, 44.02) * mm});
            skLineSegment(sketch, "E404", {"start": v(-5.1, 44.02) * mm, "end": v(-5.03, 44.03) * mm});
            skLineSegment(sketch, "E405", {"start": v(-5.03, 44.03) * mm, "end": v(-5, 44.05) * mm});
            skLineSegment(sketch, "E406", {"start": v(-5, 44.05) * mm, "end": v(-4.94, 44.07) * mm});
            skLineSegment(sketch, "E407", {"start": v(-4.94, 44.07) * mm, "end": v(-4.9, 44.1) * mm});
            skLineSegment(sketch, "E408", {"start": v(-4.9, 44.1) * mm, "end": v(-4.86, 44.12) * mm});
            skLineSegment(sketch, "E409", {"start": v(-4.86, 44.12) * mm, "end": v(-4.83, 44.14) * mm});
            skLineSegment(sketch, "E410", {"start": v(-4.83, 44.14) * mm, "end": v(-2.57, 46.4) * mm});
            skLineSegment(sketch, "E411", {"start": v(-2.57, 46.4) * mm, "end": v(-2.54, 46.44) * mm});
            skLineSegment(sketch, "E412", {"start": v(-2.54, 46.44) * mm, "end": v(-2.5, 46.51) * mm});
            skLineSegment(sketch, "E413", {"start": v(-2.5, 46.51) * mm, "end": v(-2.47, 46.55) * mm});
            skLineSegment(sketch, "E414", {"start": v(-2.47, 46.55) * mm, "end": v(-2.46, 46.6) * mm});
            skLineSegment(sketch, "E415", {"start": v(-2.46, 46.6) * mm, "end": v(-2.44, 46.64) * mm});
            skLineSegment(sketch, "E416", {"start": v(-2.44, 46.64) * mm, "end": v(-2.44, 46.7) * mm});
            skLineSegment(sketch, "E417", {"start": v(-2.44, 46.7) * mm, "end": v(-2.44, 46.75) * mm});
            skLineSegment(sketch, "E418", {"start": v(-2.44, 46.75) * mm, "end": v(-2.45, 46.8) * mm});
            skLineSegment(sketch, "E419", {"start": v(-2.45, 46.8) * mm, "end": v(-2.48, 46.84) * mm});
            skLineSegment(sketch, "E420", {"start": v(-2.48, 46.84) * mm, "end": v(-2.5, 46.89) * mm});
            skLineSegment(sketch, "E421", {"start": v(-2.5, 46.89) * mm, "end": v(-2.55, 46.93) * mm});
            skLineSegment(sketch, "E422", {"start": v(-2.55, 46.93) * mm, "end": v(-2.6, 46.96) * mm});
            skLineSegment(sketch, "E423", {"start": v(-2.6, 46.96) * mm, "end": v(-2.62, 46.98) * mm});
            skLineSegment(sketch, "E424", {"start": v(-2.62, 46.98) * mm, "end": v(-2.65, 46.99) * mm});
            skLineSegment(sketch, "E425", {"start": v(-2.65, 46.99) * mm, "end": v(-2.7, 47) * mm});
            skLineSegment(sketch, "E426", {"start": v(-2.7, 47) * mm, "end": v(-2.77, 47) * mm});
            skLineSegment(sketch, "E427", {"start": v(-2.77, 47) * mm, "end": v(-2.8, 47) * mm});
            skLineSegment(sketch, "E428", {"start": v(-2.8, 47) * mm, "end": v(-2.84, 47) * mm});
            skLineSegment(sketch, "E429", {"start": v(-2.84, 47) * mm, "end": v(-2.88, 46.98) * mm});
            skLineSegment(sketch, "E430", {"start": v(-2.88, 46.98) * mm, "end": v(-2.95, 46.94) * mm});
            skLineSegment(sketch, "E431", {"start": v(-2.95, 46.94) * mm, "end": v(-3.03, 46.9) * mm});
            skLineSegment(sketch, "E432", {"start": v(-3.03, 46.9) * mm, "end": v(-3.1, 46.87) * mm});
            skLineSegment(sketch, "E433", {"start": v(-3.1, 46.87) * mm, "end": v(-3.16, 46.86) * mm});
            skLineSegment(sketch, "E434", {"start": v(-3.16, 46.86) * mm, "end": v(-3.21, 46.85) * mm});
            skLineSegment(sketch, "E435", {"start": v(-3.21, 46.85) * mm, "end": v(-3.26, 46.85) * mm});
            skLineSegment(sketch, "E436", {"start": v(-3.26, 46.85) * mm, "end": v(-3.3, 46.86) * mm});
            skLineSegment(sketch, "E437", {"start": v(-3.3, 46.86) * mm, "end": v(-3.35, 46.88) * mm});
            skLineSegment(sketch, "E438", {"start": v(-3.35, 46.88) * mm, "end": v(-3.4, 46.9) * mm});
            skLineSegment(sketch, "E439", {"start": v(-3.4, 46.9) * mm, "end": v(-3.44, 46.94) * mm});
            skLineSegment(sketch, "E440", {"start": v(-3.44, 46.94) * mm, "end": v(-7.89, 51.4) * mm});
            skLineSegment(sketch, "E441", {"start": v(-7.89, 51.4) * mm, "end": v(-7.92, 51.44) * mm});
            skLineSegment(sketch, "E442", {"start": v(-7.92, 51.44) * mm, "end": v(-7.96, 51.48) * mm});
            skLineSegment(sketch, "E443", {"start": v(-7.96, 51.48) * mm, "end": v(-7.98, 51.52) * mm});
            skLineSegment(sketch, "E444", {"start": v(-7.98, 51.52) * mm, "end": v(-8, 51.55) * mm});
            skLineSegment(sketch, "E445", {"start": v(-8, 51.55) * mm, "end": v(-8, 51.57) * mm});
            skLineSegment(sketch, "E446", {"start": v(-8, 51.57) * mm, "end": v(-8, 51.63) * mm});
            skLineSegment(sketch, "E447", {"start": v(-8, 51.63) * mm, "end": v(-8, 51.69) * mm});
            skLineSegment(sketch, "E448", {"start": v(-8, 51.69) * mm, "end": v(-7.98, 51.74) * mm});
            skLineSegment(sketch, "E449", {"start": v(-7.98, 51.74) * mm, "end": v(-7.96, 51.8) * mm});
            skLineSegment(sketch, "E450", {"start": v(-7.96, 51.8) * mm, "end": v(-7.87, 51.99) * mm});
            skLineSegment(sketch, "E451", {"start": v(-7.87, 51.99) * mm, "end": v(-7.86, 52.03) * mm});
            skLineSegment(sketch, "E452", {"start": v(-7.86, 52.03) * mm, "end": v(-7.85, 52.09) * mm});
            skLineSegment(sketch, "E453", {"start": v(-7.85, 52.09) * mm, "end": v(-7.85, 52.15) * mm});
            skLineSegment(sketch, "E454", {"start": v(-7.85, 52.15) * mm, "end": v(-7.86, 52.2) * mm});
            skLineSegment(sketch, "E455", {"start": v(-7.86, 52.2) * mm, "end": v(-7.88, 52.25) * mm});
            skLineSegment(sketch, "E456", {"start": v(-7.88, 52.25) * mm, "end": v(-7.9, 52.29) * mm});
            skLineSegment(sketch, "E457", {"start": v(-7.9, 52.29) * mm, "end": v(-7.94, 52.32) * mm});
            skLineSegment(sketch, "E458", {"start": v(-7.94, 52.32) * mm, "end": v(-7.97, 52.35) * mm});
            skLineSegment(sketch, "E459", {"start": v(-7.97, 52.35) * mm, "end": v(-8, 52.37) * mm});
            skLineSegment(sketch, "E460", {"start": v(-8, 52.37) * mm, "end": v(-8.04, 52.39) * mm});
            skLineSegment(sketch, "E461", {"start": v(-8.04, 52.39) * mm, "end": v(-8.07, 52.4) * mm});
            skLineSegment(sketch, "E462", {"start": v(-8.07, 52.4) * mm, "end": v(-8.11, 52.41) * mm});
            skLineSegment(sketch, "E463", {"start": v(-8.11, 52.41) * mm, "end": v(-8.15, 52.41) * mm});
            skLineSegment(sketch, "E464", {"start": v(-8.15, 52.41) * mm, "end": v(-8.21, 52.4) * mm});
            skLineSegment(sketch, "E465", {"start": v(-8.21, 52.4) * mm, "end": v(-8.27, 52.4) * mm});
            skLineSegment(sketch, "E466", {"start": v(-8.27, 52.4) * mm, "end": v(-8.33, 52.37) * mm});
            skLineSegment(sketch, "E467", {"start": v(-8.33, 52.37) * mm, "end": v(-8.4, 52.33) * mm});
            skLineSegment(sketch, "E468", {"start": v(-8.4, 52.33) * mm, "end": v(-8.43, 52.3) * mm});
            skLineSegment(sketch, "E469", {"start": v(-8.43, 52.3) * mm, "end": v(-10.7, 50.03) * mm});
            skLineSegment(sketch, "E470", {"start": v(-10.7, 50.03) * mm, "end": v(-10.73, 50) * mm});
            skLineSegment(sketch, "E471", {"start": v(-10.73, 50) * mm, "end": v(-10.76, 49.95) * mm});
            skLineSegment(sketch, "E472", {"start": v(-10.76, 49.95) * mm, "end": v(-10.79, 49.91) * mm});
            skLineSegment(sketch, "E473", {"start": v(-10.79, 49.91) * mm, "end": v(-10.8, 49.87) * mm});
            skLineSegment(sketch, "E474", {"start": v(-10.8, 49.87) * mm, "end": v(-10.82, 49.83) * mm});
            skLineSegment(sketch, "E475", {"start": v(-10.82, 49.83) * mm, "end": v(-10.83, 49.78) * mm});
            skLineSegment(sketch, "E476", {"start": v(-10.83, 49.78) * mm, "end": v(-10.83, 49.74) * mm});
            skLineSegment(sketch, "E477", {"start": v(-10.83, 49.74) * mm, "end": v(-10.83, 49.7) * mm});
            skLineSegment(sketch, "E478", {"start": v(-10.83, 49.7) * mm, "end": v(-10.82, 49.66) * mm});
            skLineSegment(sketch, "E479", {"start": v(-10.82, 49.66) * mm, "end": v(-10.8, 49.6) * mm});
            skLineSegment(sketch, "E480", {"start": v(-10.8, 49.6) * mm, "end": v(-10.8, 49.58) * mm});
            skLineSegment(sketch, "E481", {"start": v(-10.8, 49.58) * mm, "end": v(-10.78, 49.58) * mm});
            skLineSegment(sketch, "E482", {"start": v(-10.78, 49.58) * mm, "end": v(-10.78, 49.58) * mm});
            skLineSegment(sketch, "E483", {"start": v(-10.78, 49.58) * mm, "end": v(-10.78, 49.57) * mm});
            skLineSegment(sketch, "E484", {"start": v(-10.78, 49.57) * mm, "end": v(-10.78, 49.56) * mm});
            skLineSegment(sketch, "E485", {"start": v(-10.78, 49.56) * mm, "end": v(-10.75, 49.53) * mm});
            skLineSegment(sketch, "E486", {"start": v(-10.75, 49.53) * mm, "end": v(-10.71, 49.5) * mm});
            skLineSegment(sketch, "E487", {"start": v(-10.71, 49.5) * mm, "end": v(-10.68, 49.47) * mm});
            skLineSegment(sketch, "E488", {"start": v(-10.68, 49.47) * mm, "end": v(-10.65, 49.46) * mm});
            skLineSegment(sketch, "E489", {"start": v(-10.65, 49.46) * mm, "end": v(-10.62, 49.44) * mm});
            skLineSegment(sketch, "E490", {"start": v(-10.62, 49.44) * mm, "end": v(-10.58, 49.43) * mm});
            skLineSegment(sketch, "E491", {"start": v(-10.58, 49.43) * mm, "end": v(-10.54, 49.43) * mm});
            skLineSegment(sketch, "E492", {"start": v(-10.54, 49.43) * mm, "end": v(-10.5, 49.43) * mm});
            skLineSegment(sketch, "E493", {"start": v(-10.5, 49.43) * mm, "end": v(-10.45, 49.44) * mm});
            skLineSegment(sketch, "E494", {"start": v(-10.45, 49.44) * mm, "end": v(-10.42, 49.45) * mm});
            skLineSegment(sketch, "E495", {"start": v(-10.42, 49.45) * mm, "end": v(-10.2, 49.55) * mm});
            skLineSegment(sketch, "E496", {"start": v(-10.2, 49.55) * mm, "end": v(-10.15, 49.57) * mm});
            skLineSegment(sketch, "E497", {"start": v(-10.15, 49.57) * mm, "end": v(-10.1, 49.58) * mm});
            skLineSegment(sketch, "E498", {"start": v(-10.1, 49.58) * mm, "end": v(-10.06, 49.58) * mm});
            skLineSegment(sketch, "E499", {"start": v(-10.06, 49.58) * mm, "end": v(-10.02, 49.58) * mm});
            skLineSegment(sketch, "E500", {"start": v(-10.02, 49.58) * mm, "end": v(-9.98, 49.58) * mm});
            skLineSegment(sketch, "E501", {"start": v(-9.98, 49.58) * mm, "end": v(-9.94, 49.56) * mm});
            skLineSegment(sketch, "E502", {"start": v(-9.94, 49.56) * mm, "end": v(-9.9, 49.53) * mm});
            skLineSegment(sketch, "E503", {"start": v(-9.9, 49.53) * mm, "end": v(-9.85, 49.5) * mm});
            skLineSegment(sketch, "E504", {"start": v(-9.85, 49.5) * mm, "end": v(-9.8, 49.45) * mm});
            skLineSegment(sketch, "E505", {"start": v(-9.8, 49.45) * mm, "end": v(-9.73, 49.39) * mm});
            skLineSegment(sketch, "E506", {"start": v(-9.73, 49.39) * mm, "end": v(-7.88, 47.53) * mm});
            skLineSegment(sketch, "E507", {"start": v(-7.88, 47.53) * mm, "end": v(-7.88, 47.52) * mm});
            skLineSegment(sketch, "E508", {"start": v(-7.88, 47.52) * mm, "end": v(-8.56, 46.84) * mm});
            skLineSegment(sketch, "E509", {"start": v(-8.56, 46.84) * mm, "end": v(-8.19, 46.46) * mm});
            skLineSegment(sketch, "E510", {"start": v(-8.19, 46.46) * mm, "end": v(-8.1, 46.38) * mm});
            skLineSegment(sketch, "E511", {"start": v(-8.1, 46.38) * mm, "end": v(-7.42, 47.07) * mm});
            skLineSegment(sketch, "E512", {"start": v(-7.42, 47.07) * mm, "end": v(-7.42, 47.07) * mm});
            skLineSegment(sketch, "E513", {"start": v(-7.42, 47.07) * mm, "end": v(-5.38, 45.04) * mm});
            skLineSegment(sketch, "E514", {"start": v(-5.38, 45.04) * mm, "end": v(-5.35, 45) * mm});
            skLineSegment(sketch, "E515", {"start": v(-5.35, 45) * mm, "end": v(-5.3, 44.93) * mm});
            skLineSegment(sketch, "E516", {"start": v(-5.3, 44.93) * mm, "end": v(-5.28, 44.89) * mm});
            skLineSegment(sketch, "E517", {"start": v(-5.28, 44.89) * mm, "end": v(-5.28, 44.89) * mm});
            skLineSegment(sketch, "E518", {"start": v(-5.28, 44.89) * mm, "end": v(-5.27, 44.84) * mm});
            skLineSegment(sketch, "E519", {"start": v(-5.27, 44.84) * mm, "end": v(-5.27, 44.82) * mm});
            skLineSegment(sketch, "E520", {"start": v(-5.27, 44.82) * mm, "end": v(-5.27, 44.79) * mm});
            skLineSegment(sketch, "E521", {"start": v(-5.27, 44.79) * mm, "end": v(-5.28, 44.72) * mm});
            skLineSegment(sketch, "E522", {"start": v(-5.28, 44.72) * mm, "end": v(-5.31, 44.64) * mm});
            skLineSegment(sketch, "E523", {"start": v(-5.31, 44.64) * mm, "end": v(-5.36, 44.53) * mm});
            skLineSegment(sketch, "E524", {"start": v(-5.36, 44.53) * mm, "end": v(-5.4, 44.46) * mm});
            skLineSegment(sketch, "E525", {"start": v(-5.4, 44.46) * mm, "end": v(-5.4, 44.42) * mm});
            skLineSegment(sketch, "E526", {"start": v(-5.4, 44.42) * mm, "end": v(-5.42, 44.38) * mm});
            skLineSegment(sketch, "E527", {"start": v(-5.42, 44.38) * mm, "end": v(-5.42, 44.34) * mm});
            skLineSegment(sketch, "E528", {"start": v(-5.42, 44.34) * mm, "end": v(-5.42, 44.3) * mm});
            skLineSegment(sketch, "E529", {"start": v(-5.42, 44.3) * mm, "end": v(-5.42, 44.26) * mm});
            skLineSegment(sketch, "E530", {"start": v(-5.42, 44.26) * mm, "end": v(-5.4, 44.22) * mm});
            skLineSegment(sketch, "E531", {"start": v(-5.4, 44.22) * mm, "end": v(-5.4, 44.2) * mm});
            skLineSegment(sketch, "E532", {"start": v(-5.4, 44.2) * mm, "end": v(-5.38, 44.17) * mm});
            skLineSegment(sketch, "E533", {"start": v(-5.38, 44.17) * mm, "end": v(-5.37, 44.16) * mm});
            skLineSegment(sketch, "E534", {"start": v(-5.37, 44.16) * mm, "end": v(-5.37, 44.16) * mm});
            skLineSegment(sketch, "E535", {"start": v(-5.37, 44.16) * mm, "end": v(-5.37, 44.15) * mm});
            skLineSegment(sketch, "E536", {"start": v(-5.37, 44.15) * mm, "end": v(-5.36, 44.15) * mm});
            skLineSegment(sketch, "E537", {"start": v(-5.36, 44.15) * mm, "end": v(-5.36, 44.14) * mm});
            skLineSegment(sketch, "E538", {"start": v(-5.36, 44.14) * mm, "end": v(-5.36, 44.14) * mm});
            skLineSegment(sketch, "E539", {"start": v(-5.36, 44.14) * mm, "end": v(-5.36, 44.13) * mm});
            skLineSegment(sketch, "E540", {"start": v(-5.36, 44.13) * mm, "end": v(-5.33, 44.1) * mm});
            skLineSegment(sketch, "E541", {"start": v(-5.33, 44.1) * mm, "end": v(-5.29, 44.07) * mm});
            skLineSegment(sketch, "E542", {"start": v(-5.29, 44.07) * mm, "end": v(-5.25, 44.05) * mm});
            skLineSegment(sketch, "E543", {"start": v(-5.25, 44.05) * mm, "end": v(-5.2, 44.03) * mm});
            skLineSegment(sketch, "E544", {"start": v(-5.2, 44.03) * mm, "end": v(-5.16, 44.02) * mm});
            skLineSegment(sketch, "E545", {"start": v(5.99, 46.99) * mm, "end": v(6.02, 46.98) * mm});
            skLineSegment(sketch, "E546", {"start": v(6.02, 46.98) * mm, "end": v(6.05, 46.98) * mm});
            skLineSegment(sketch, "E547", {"start": v(6.05, 46.98) * mm, "end": v(6.09, 46.99) * mm});
            skLineSegment(sketch, "E548", {"start": v(6.09, 46.99) * mm, "end": v(6.12, 47) * mm});
            skLineSegment(sketch, "E549", {"start": v(6.12, 47) * mm, "end": v(6.15, 47.01) * mm});
            skLineSegment(sketch, "E550", {"start": v(6.15, 47.01) * mm, "end": v(7.45, 48.31) * mm});
            skLineSegment(sketch, "E551", {"start": v(7.45, 48.31) * mm, "end": v(7.47, 48.35) * mm});
            skLineSegment(sketch, "E552", {"start": v(7.47, 48.35) * mm, "end": v(7.48, 48.38) * mm});
            skLineSegment(sketch, "E553", {"start": v(7.48, 48.38) * mm, "end": v(7.5, 48.41) * mm});
            skLineSegment(sketch, "E554", {"start": v(7.5, 48.41) * mm, "end": v(7.5, 48.44) * mm});
            skLineSegment(sketch, "E555", {"start": v(7.5, 48.44) * mm, "end": v(7.5, 48.47) * mm});
            skLineSegment(sketch, "E556", {"start": v(7.5, 48.47) * mm, "end": v(7.5, 48.5) * mm});
            skLineSegment(sketch, "E557", {"start": v(7.5, 48.5) * mm, "end": v(7.49, 48.53) * mm});
            skLineSegment(sketch, "E558", {"start": v(7.49, 48.53) * mm, "end": v(7.48, 48.55) * mm});
            skLineSegment(sketch, "E559", {"start": v(7.48, 48.55) * mm, "end": v(7.46, 48.58) * mm});
            skLineSegment(sketch, "E560", {"start": v(7.46, 48.58) * mm, "end": v(7.42, 48.6) * mm});
            skLineSegment(sketch, "E561", {"start": v(7.42, 48.6) * mm, "end": v(7.38, 48.63) * mm});
            skLineSegment(sketch, "E562", {"start": v(7.38, 48.63) * mm, "end": v(7.34, 48.63) * mm});
            skLineSegment(sketch, "E563", {"start": v(7.34, 48.63) * mm, "end": v(7.3, 48.63) * mm});
            skLineSegment(sketch, "E564", {"start": v(7.3, 48.63) * mm, "end": v(7.27, 48.62) * mm});
            skLineSegment(sketch, "E565", {"start": v(7.27, 48.62) * mm, "end": v(7.2, 48.6) * mm});
            skLineSegment(sketch, "E566", {"start": v(7.2, 48.6) * mm, "end": v(7.15, 48.57) * mm});
            skLineSegment(sketch, "E567", {"start": v(7.15, 48.57) * mm, "end": v(7.1, 48.55) * mm});
            skLineSegment(sketch, "E568", {"start": v(7.1, 48.55) * mm, "end": v(7.06, 48.55) * mm});
            skLineSegment(sketch, "E569", {"start": v(7.06, 48.55) * mm, "end": v(7.01, 48.55) * mm});
            skLineSegment(sketch, "E570", {"start": v(7.01, 48.55) * mm, "end": v(7, 48.56) * mm});
            skLineSegment(sketch, "E571", {"start": v(7, 48.56) * mm, "end": v(6.97, 48.58) * mm});
            skLineSegment(sketch, "E572", {"start": v(6.97, 48.58) * mm, "end": v(6.94, 48.6) * mm});
            skLineSegment(sketch, "E573", {"start": v(6.94, 48.6) * mm, "end": v(4.03, 51.5) * mm});
            skLineSegment(sketch, "E574", {"start": v(4.03, 51.5) * mm, "end": v(3.2, 50.69) * mm});
            skLineSegment(sketch, "E575", {"start": v(3.2, 50.69) * mm, "end": v(2.85, 50.33) * mm});
            skLineSegment(sketch, "E576", {"start": v(2.85, 50.33) * mm, "end": v(2.83, 50.3) * mm});
            skLineSegment(sketch, "E577", {"start": v(2.83, 50.3) * mm, "end": v(2.8, 50.26) * mm});
            skLineSegment(sketch, "E578", {"start": v(2.8, 50.26) * mm, "end": v(2.8, 50.23) * mm});
            skLineSegment(sketch, "E579", {"start": v(2.8, 50.23) * mm, "end": v(2.79, 50.2) * mm});
            skLineSegment(sketch, "E580", {"start": v(2.79, 50.2) * mm, "end": v(2.78, 50.17) * mm});
            skLineSegment(sketch, "E581", {"start": v(2.78, 50.17) * mm, "end": v(2.79, 50.13) * mm});
            skLineSegment(sketch, "E582", {"start": v(2.79, 50.13) * mm, "end": v(2.8, 50.1) * mm});
            skLineSegment(sketch, "E583", {"start": v(2.8, 50.1) * mm, "end": v(2.82, 50.07) * mm});
            skLineSegment(sketch, "E584", {"start": v(2.82, 50.07) * mm, "end": v(2.84, 50.04) * mm});
            skLineSegment(sketch, "E585", {"start": v(2.84, 50.04) * mm, "end": v(2.87, 50.02) * mm});
            skLineSegment(sketch, "E586", {"start": v(2.87, 50.02) * mm, "end": v(2.9, 50) * mm});
            skLineSegment(sketch, "E587", {"start": v(2.9, 50) * mm, "end": v(2.92, 50) * mm});
            skLineSegment(sketch, "E588", {"start": v(2.92, 50) * mm, "end": v(2.95, 50) * mm});
            skLineSegment(sketch, "E589", {"start": v(2.95, 50) * mm, "end": v(2.98, 50) * mm});
            skLineSegment(sketch, "E590", {"start": v(2.98, 50) * mm, "end": v(3, 50) * mm});
            skLineSegment(sketch, "E591", {"start": v(3, 50) * mm, "end": v(3.07, 50.03) * mm});
            skLineSegment(sketch, "E592", {"start": v(3.07, 50.03) * mm, "end": v(3.15, 50.07) * mm});
            skLineSegment(sketch, "E593", {"start": v(3.15, 50.07) * mm, "end": v(3.18, 50.08) * mm});
            skLineSegment(sketch, "E594", {"start": v(3.18, 50.08) * mm, "end": v(3.21, 50.08) * mm});
            skLineSegment(sketch, "E595", {"start": v(3.21, 50.08) * mm, "end": v(3.24, 50.08) * mm});
            skLineSegment(sketch, "E596", {"start": v(3.24, 50.08) * mm, "end": v(3.27, 50.08) * mm});
            skLineSegment(sketch, "E597", {"start": v(3.27, 50.08) * mm, "end": v(3.3, 50.07) * mm});
            skLineSegment(sketch, "E598", {"start": v(3.3, 50.07) * mm, "end": v(3.31, 50.06) * mm});
            skLineSegment(sketch, "E599", {"start": v(3.31, 50.06) * mm, "end": v(3.32, 50.06) * mm});
            skLineSegment(sketch, "E600", {"start": v(3.32, 50.06) * mm, "end": v(3.32, 50.06) * mm});
            skLineSegment(sketch, "E601", {"start": v(3.32, 50.06) * mm, "end": v(3.32, 50.05) * mm});
            skLineSegment(sketch, "E602", {"start": v(3.32, 50.05) * mm, "end": v(3.33, 50.04) * mm});
            skLineSegment(sketch, "E603", {"start": v(3.33, 50.04) * mm, "end": v(3.35, 50.03) * mm});
            skLineSegment(sketch, "E604", {"start": v(3.35, 50.03) * mm, "end": v(3.34, 50.03) * mm});
            skLineSegment(sketch, "E605", {"start": v(3.34, 50.03) * mm, "end": v(5.89, 47.49) * mm});
            skLineSegment(sketch, "E606", {"start": v(5.89, 47.49) * mm, "end": v(5.9, 47.47) * mm});
            skLineSegment(sketch, "E607", {"start": v(5.9, 47.47) * mm, "end": v(5.92, 47.45) * mm});
            skLineSegment(sketch, "E608", {"start": v(5.92, 47.45) * mm, "end": v(5.93, 47.42) * mm});
            skLineSegment(sketch, "E609", {"start": v(5.93, 47.42) * mm, "end": v(5.93, 47.4) * mm});
            skLineSegment(sketch, "E610", {"start": v(5.93, 47.4) * mm, "end": v(5.93, 47.37) * mm});
            skLineSegment(sketch, "E611", {"start": v(5.93, 47.37) * mm, "end": v(5.92, 47.34) * mm});
            skLineSegment(sketch, "E612", {"start": v(5.92, 47.34) * mm, "end": v(5.86, 47.21) * mm});
            skLineSegment(sketch, "E613", {"start": v(5.86, 47.21) * mm, "end": v(5.85, 47.19) * mm});
            skLineSegment(sketch, "E614", {"start": v(5.85, 47.19) * mm, "end": v(5.85, 47.16) * mm});
            skLineSegment(sketch, "E615", {"start": v(5.85, 47.16) * mm, "end": v(5.86, 47.13) * mm});
            skLineSegment(sketch, "E616", {"start": v(5.86, 47.13) * mm, "end": v(5.87, 47.1) * mm});
            skLineSegment(sketch, "E617", {"start": v(5.87, 47.1) * mm, "end": v(5.88, 47.07) * mm});
            skLineSegment(sketch, "E618", {"start": v(5.88, 47.07) * mm, "end": v(5.9, 47.04) * mm});
            skLineSegment(sketch, "E619", {"start": v(5.9, 47.04) * mm, "end": v(5.93, 47.02) * mm});
            skLineSegment(sketch, "E620", {"start": v(5.93, 47.02) * mm, "end": v(5.96, 47) * mm});
            skLineSegment(sketch, "E621", {"start": v(5.96, 47) * mm, "end": v(5.99, 46.99) * mm});
            skLineSegment(sketch, "E622", {"start": v(4.08, 47.14) * mm, "end": v(4.12, 47.13) * mm});
            skLineSegment(sketch, "E623", {"start": v(4.12, 47.13) * mm, "end": v(4.15, 47.13) * mm});
            skLineSegment(sketch, "E624", {"start": v(4.15, 47.13) * mm, "end": v(4.19, 47.13) * mm});
            skLineSegment(sketch, "E625", {"start": v(4.19, 47.13) * mm, "end": v(4.22, 47.14) * mm});
            skLineSegment(sketch, "E626", {"start": v(4.22, 47.14) * mm, "end": v(4.25, 47.16) * mm});
            skLineSegment(sketch, "E627", {"start": v(4.25, 47.16) * mm, "end": v(4.28, 47.2) * mm});
            skLineSegment(sketch, "E628", {"start": v(4.28, 47.2) * mm, "end": v(4.3, 47.22) * mm});
            skLineSegment(sketch, "E629", {"start": v(4.3, 47.22) * mm, "end": v(4.32, 47.25) * mm});
            skLineSegment(sketch, "E630", {"start": v(4.32, 47.25) * mm, "end": v(4.32, 47.27) * mm});
            skLineSegment(sketch, "E631", {"start": v(4.32, 47.27) * mm, "end": v(4.32, 47.3) * mm});
            skLineSegment(sketch, "E632", {"start": v(4.32, 47.3) * mm, "end": v(4.31, 47.33) * mm});
            skLineSegment(sketch, "E633", {"start": v(4.31, 47.33) * mm, "end": v(4.3, 47.36) * mm});
            skLineSegment(sketch, "E634", {"start": v(4.3, 47.36) * mm, "end": v(4.29, 47.4) * mm});
            skLineSegment(sketch, "E635", {"start": v(4.29, 47.4) * mm, "end": v(3.16, 48.52) * mm});
            skLineSegment(sketch, "E636", {"start": v(3.16, 48.52) * mm, "end": v(3.15, 48.53) * mm});
            skLineSegment(sketch, "E637", {"start": v(3.15, 48.53) * mm, "end": v(3.1, 48.56) * mm});
            skLineSegment(sketch, "E638", {"start": v(3.1, 48.56) * mm, "end": v(3.07, 48.57) * mm});
            skLineSegment(sketch, "E639", {"start": v(3.07, 48.57) * mm, "end": v(3.02, 48.57) * mm});
            skLineSegment(sketch, "E640", {"start": v(3.02, 48.57) * mm, "end": v(2.99, 48.56) * mm});
            skLineSegment(sketch, "E641", {"start": v(2.99, 48.56) * mm, "end": v(2.94, 48.54) * mm});
            skLineSegment(sketch, "E642", {"start": v(2.94, 48.54) * mm, "end": v(2.91, 48.5) * mm});
            skLineSegment(sketch, "E643", {"start": v(2.91, 48.5) * mm, "end": v(2.89, 48.46) * mm});
            skLineSegment(sketch, "E644", {"start": v(2.89, 48.46) * mm, "end": v(2.88, 48.42) * mm});
            skLineSegment(sketch, "E645", {"start": v(2.88, 48.42) * mm, "end": v(2.88, 48.38) * mm});
            skLineSegment(sketch, "E646", {"start": v(2.88, 48.38) * mm, "end": v(2.89, 48.34) * mm});
            skLineSegment(sketch, "E647", {"start": v(2.89, 48.34) * mm, "end": v(2.9, 48.3) * mm});
            skLineSegment(sketch, "E648", {"start": v(2.9, 48.3) * mm, "end": v(2.93, 48.24) * mm});
            skLineSegment(sketch, "E649", {"start": v(2.93, 48.24) * mm, "end": v(3, 48.12) * mm});
            skLineSegment(sketch, "E650", {"start": v(3, 48.12) * mm, "end": v(3.03, 48.05) * mm});
            skLineSegment(sketch, "E651", {"start": v(3.03, 48.05) * mm, "end": v(3.04, 48.04) * mm});
            skLineSegment(sketch, "E652", {"start": v(3.04, 48.04) * mm, "end": v(3.05, 48) * mm});
            skLineSegment(sketch, "E653", {"start": v(3.05, 48) * mm, "end": v(3.07, 47.94) * mm});
            skLineSegment(sketch, "E654", {"start": v(3.07, 47.94) * mm, "end": v(3.08, 47.88) * mm});
            skLineSegment(sketch, "E655", {"start": v(3.08, 47.88) * mm, "end": v(3.08, 47.83) * mm});
            skLineSegment(sketch, "E656", {"start": v(3.08, 47.83) * mm, "end": v(3.08, 47.78) * mm});
            skLineSegment(sketch, "E657", {"start": v(3.08, 47.78) * mm, "end": v(3.08, 47.72) * mm});
            skLineSegment(sketch, "E658", {"start": v(3.08, 47.72) * mm, "end": v(3.07, 47.67) * mm});
            skLineSegment(sketch, "E659", {"start": v(3.07, 47.67) * mm, "end": v(3.05, 47.62) * mm});
            skLineSegment(sketch, "E660", {"start": v(3.05, 47.62) * mm, "end": v(3.03, 47.58) * mm});
            skLineSegment(sketch, "E661", {"start": v(3.03, 47.58) * mm, "end": v(3.01, 47.54) * mm});
            skLineSegment(sketch, "E662", {"start": v(3.01, 47.54) * mm, "end": v(3.28, 47.27) * mm});
            skLineSegment(sketch, "E663", {"start": v(3.28, 47.27) * mm, "end": v(3.3, 47.27) * mm});
            skLineSegment(sketch, "E664", {"start": v(3.3, 47.27) * mm, "end": v(3.3, 47.27) * mm});
            skLineSegment(sketch, "E665", {"start": v(3.3, 47.27) * mm, "end": v(3.3, 47.28) * mm});
            skLineSegment(sketch, "E666", {"start": v(3.3, 47.28) * mm, "end": v(3.3, 47.28) * mm});
            skLineSegment(sketch, "E667", {"start": v(3.3, 47.28) * mm, "end": v(3.32, 47.28) * mm});
            skLineSegment(sketch, "E668", {"start": v(3.32, 47.28) * mm, "end": v(3.34, 47.3) * mm});
            skLineSegment(sketch, "E669", {"start": v(3.34, 47.3) * mm, "end": v(3.39, 47.3) * mm});
            skLineSegment(sketch, "E670", {"start": v(3.39, 47.3) * mm, "end": v(3.43, 47.32) * mm});
            skLineSegment(sketch, "E671", {"start": v(3.43, 47.32) * mm, "end": v(3.48, 47.33) * mm});
            skLineSegment(sketch, "E672", {"start": v(3.48, 47.33) * mm, "end": v(3.54, 47.33) * mm});
            skLineSegment(sketch, "E673", {"start": v(3.54, 47.33) * mm, "end": v(3.6, 47.33) * mm});
            skLineSegment(sketch, "E674", {"start": v(3.6, 47.33) * mm, "end": v(3.64, 47.32) * mm});
            skLineSegment(sketch, "E675", {"start": v(3.64, 47.32) * mm, "end": v(3.69, 47.32) * mm});
            skLineSegment(sketch, "E676", {"start": v(3.69, 47.32) * mm, "end": v(3.74, 47.3) * mm});
            skLineSegment(sketch, "E677", {"start": v(3.74, 47.3) * mm, "end": v(3.8, 47.28) * mm});
            skLineSegment(sketch, "E678", {"start": v(3.8, 47.28) * mm, "end": v(3.85, 47.26) * mm});
            skLineSegment(sketch, "E679", {"start": v(3.85, 47.26) * mm, "end": v(3.98, 47.2) * mm});
            skLineSegment(sketch, "E680", {"start": v(3.98, 47.2) * mm, "end": v(4.03, 47.16) * mm});
            skLineSegment(sketch, "E681", {"start": v(4.03, 47.16) * mm, "end": v(4.08, 47.14) * mm});
            skLineSegment(sketch, "E682", {"start": v(1.54, 49.02) * mm, "end": v(1.79, 48.76) * mm});
            skLineSegment(sketch, "E683", {"start": v(1.79, 48.76) * mm, "end": v(1.8, 48.77) * mm});
            skLineSegment(sketch, "E684", {"start": v(1.8, 48.77) * mm, "end": v(1.86, 48.8) * mm});
            skLineSegment(sketch, "E685", {"start": v(1.86, 48.8) * mm, "end": v(1.93, 48.85) * mm});
            skLineSegment(sketch, "E686", {"start": v(1.93, 48.85) * mm, "end": v(2, 48.89) * mm});
            skLineSegment(sketch, "E687", {"start": v(2, 48.89) * mm, "end": v(2.06, 48.92) * mm});
            skLineSegment(sketch, "E688", {"start": v(2.06, 48.92) * mm, "end": v(2.13, 48.95) * mm});
            skLineSegment(sketch, "E689", {"start": v(2.13, 48.95) * mm, "end": v(2.2, 48.97) * mm});
            skLineSegment(sketch, "E690", {"start": v(2.2, 48.97) * mm, "end": v(2.27, 49) * mm});
            skLineSegment(sketch, "E691", {"start": v(2.27, 49) * mm, "end": v(2.33, 49) * mm});
            skLineSegment(sketch, "E692", {"start": v(2.33, 49) * mm, "end": v(2.4, 49.02) * mm});
            skLineSegment(sketch, "E693", {"start": v(2.4, 49.02) * mm, "end": v(2.47, 49.02) * mm});
            skLineSegment(sketch, "E694", {"start": v(2.47, 49.02) * mm, "end": v(2.54, 49.02) * mm});
            skLineSegment(sketch, "E695", {"start": v(2.54, 49.02) * mm, "end": v(2.62, 49.02) * mm});
            skLineSegment(sketch, "E696", {"start": v(2.62, 49.02) * mm, "end": v(2.69, 49.01) * mm});
            skLineSegment(sketch, "E697", {"start": v(2.69, 49.01) * mm, "end": v(2.76, 49) * mm});
            skLineSegment(sketch, "E698", {"start": v(2.76, 49) * mm, "end": v(2.83, 48.98) * mm});
            skLineSegment(sketch, "E699", {"start": v(2.83, 48.98) * mm, "end": v(2.9, 48.96) * mm});
            skLineSegment(sketch, "E700", {"start": v(2.9, 48.96) * mm, "end": v(2.98, 48.93) * mm});
            skLineSegment(sketch, "E701", {"start": v(2.98, 48.93) * mm, "end": v(3.04, 48.91) * mm});
            skLineSegment(sketch, "E702", {"start": v(3.04, 48.91) * mm, "end": v(3.05, 48.9) * mm});
            skLineSegment(sketch, "E703", {"start": v(3.05, 48.9) * mm, "end": v(3.07, 48.9) * mm});
            skLineSegment(sketch, "E704", {"start": v(3.07, 48.9) * mm, "end": v(3.08, 48.9) * mm});
            skLineSegment(sketch, "E705", {"start": v(3.08, 48.9) * mm, "end": v(3.22, 48.82) * mm});
            skLineSegment(sketch, "E706", {"start": v(3.22, 48.82) * mm, "end": v(3.26, 48.82) * mm});
            skLineSegment(sketch, "E707", {"start": v(3.26, 48.82) * mm, "end": v(3.3, 48.81) * mm});
            skLineSegment(sketch, "E708", {"start": v(3.3, 48.81) * mm, "end": v(3.32, 48.82) * mm});
            skLineSegment(sketch, "E709", {"start": v(3.32, 48.82) * mm, "end": v(3.34, 48.83) * mm});
            skLineSegment(sketch, "E710", {"start": v(3.34, 48.83) * mm, "end": v(3.37, 48.85) * mm});
            skLineSegment(sketch, "E711", {"start": v(3.37, 48.85) * mm, "end": v(3.4, 48.88) * mm});
            skLineSegment(sketch, "E712", {"start": v(3.4, 48.88) * mm, "end": v(3.42, 48.9) * mm});
            skLineSegment(sketch, "E713", {"start": v(3.42, 48.9) * mm, "end": v(3.44, 48.93) * mm});
            skLineSegment(sketch, "E714", {"start": v(3.44, 48.93) * mm, "end": v(3.45, 48.96) * mm});
            skLineSegment(sketch, "E715", {"start": v(3.45, 48.96) * mm, "end": v(3.46, 48.98) * mm});
            skLineSegment(sketch, "E716", {"start": v(3.46, 48.98) * mm, "end": v(3.46, 49.01) * mm});
            skLineSegment(sketch, "E717", {"start": v(3.46, 49.01) * mm, "end": v(3.46, 49.04) * mm});
            skLineSegment(sketch, "E718", {"start": v(3.46, 49.04) * mm, "end": v(3.45, 49.06) * mm});
            skLineSegment(sketch, "E719", {"start": v(3.45, 49.06) * mm, "end": v(3.44, 49.09) * mm});
            skLineSegment(sketch, "E720", {"start": v(3.44, 49.09) * mm, "end": v(2.52, 50) * mm});
            skLineSegment(sketch, "E721", {"start": v(2.52, 50) * mm, "end": v(1.54, 49.02) * mm});
            skLineSegment(sketch, "E722", {"start": v(6.02, 49.92) * mm, "end": v(6.27, 49.67) * mm});
            skLineSegment(sketch, "E723", {"start": v(6.27, 49.67) * mm, "end": v(6.33, 49.72) * mm});
            skLineSegment(sketch, "E724", {"start": v(6.33, 49.72) * mm, "end": v(6.47, 49.88) * mm});
            skLineSegment(sketch, "E725", {"start": v(6.47, 49.88) * mm, "end": v(6.58, 50) * mm});
            skLineSegment(sketch, "E726", {"start": v(6.58, 50) * mm, "end": v(6.64, 50.07) * mm});
            skLineSegment(sketch, "E727", {"start": v(6.64, 50.07) * mm, "end": v(6.66, 50.1) * mm});
            skLineSegment(sketch, "E728", {"start": v(6.66, 50.1) * mm, "end": v(6.76, 50.23) * mm});
            skLineSegment(sketch, "E729", {"start": v(6.76, 50.23) * mm, "end": v(6.8, 50.28) * mm});
            skLineSegment(sketch, "E730", {"start": v(6.8, 50.28) * mm, "end": v(6.79, 50.29) * mm});
            skLineSegment(sketch, "E731", {"start": v(6.79, 50.29) * mm, "end": v(6.79, 50.29) * mm});
            skLineSegment(sketch, "E732", {"start": v(6.79, 50.29) * mm, "end": v(6.8, 50.29) * mm});
            skLineSegment(sketch, "E733", {"start": v(6.8, 50.29) * mm, "end": v(6.8, 50.29) * mm});
            skLineSegment(sketch, "E734", {"start": v(6.8, 50.29) * mm, "end": v(6.83, 50.34) * mm});
            skLineSegment(sketch, "E735", {"start": v(6.83, 50.34) * mm, "end": v(6.9, 50.48) * mm});
            skLineSegment(sketch, "E736", {"start": v(6.9, 50.48) * mm, "end": v(6.93, 50.54) * mm});
            skLineSegment(sketch, "E737", {"start": v(6.93, 50.54) * mm, "end": v(6.95, 50.61) * mm});
            skLineSegment(sketch, "E738", {"start": v(6.95, 50.61) * mm, "end": v(6.98, 50.68) * mm});
            skLineSegment(sketch, "E739", {"start": v(6.98, 50.68) * mm, "end": v(7, 50.75) * mm});
            skLineSegment(sketch, "E740", {"start": v(7, 50.75) * mm, "end": v(7.02, 50.9) * mm});
            skLineSegment(sketch, "E741", {"start": v(7.02, 50.9) * mm, "end": v(7.03, 50.94) * mm});
            skLineSegment(sketch, "E742", {"start": v(7.03, 50.94) * mm, "end": v(7.03, 51.16) * mm});
            skLineSegment(sketch, "E743", {"start": v(7.03, 51.16) * mm, "end": v(7.02, 51.2) * mm});
            skLineSegment(sketch, "E744", {"start": v(7.02, 51.2) * mm, "end": v(7, 51.32) * mm});
            skLineSegment(sketch, "E745", {"start": v(7, 51.32) * mm, "end": v(6.97, 51.42) * mm});
            skLineSegment(sketch, "E746", {"start": v(6.97, 51.42) * mm, "end": v(6.96, 51.46) * mm});
            skLineSegment(sketch, "E747", {"start": v(6.96, 51.46) * mm, "end": v(6.96, 51.47) * mm});
            skLineSegment(sketch, "E748", {"start": v(6.96, 51.47) * mm, "end": v(7.03, 51.4) * mm});
            skLineSegment(sketch, "E749", {"start": v(7.03, 51.4) * mm, "end": v(7.04, 51.4) * mm});
            skLineSegment(sketch, "E750", {"start": v(7.04, 51.4) * mm, "end": v(7.04, 51.4) * mm});
            skLineSegment(sketch, "E751", {"start": v(7.04, 51.4) * mm, "end": v(7.04, 51.38) * mm});
            skLineSegment(sketch, "E752", {"start": v(7.04, 51.38) * mm, "end": v(7.24, 51.19) * mm});
            skLineSegment(sketch, "E753", {"start": v(7.24, 51.19) * mm, "end": v(7.34, 51.1) * mm});
            skLineSegment(sketch, "E754", {"start": v(7.34, 51.1) * mm, "end": v(7.34, 51.1) * mm});
            skLineSegment(sketch, "E755", {"start": v(7.34, 51.1) * mm, "end": v(7.35, 51.1) * mm});
            skLineSegment(sketch, "E756", {"start": v(7.35, 51.1) * mm, "end": v(7.35, 51.1) * mm});
            skLineSegment(sketch, "E757", {"start": v(7.35, 51.1) * mm, "end": v(7.34, 51.1) * mm});
            skLineSegment(sketch, "E758", {"start": v(7.34, 51.1) * mm, "end": v(7.4, 51.05) * mm});
            skLineSegment(sketch, "E759", {"start": v(7.4, 51.05) * mm, "end": v(7.5, 50.96) * mm});
            skLineSegment(sketch, "E760", {"start": v(7.5, 50.96) * mm, "end": v(7.57, 50.91) * mm});
            skLineSegment(sketch, "E761", {"start": v(7.57, 50.91) * mm, "end": v(7.6, 50.9) * mm});
            skLineSegment(sketch, "E762", {"start": v(7.6, 50.9) * mm, "end": v(7.64, 50.88) * mm});
            skLineSegment(sketch, "E763", {"start": v(7.64, 50.88) * mm, "end": v(7.64, 50.87) * mm});
            skLineSegment(sketch, "E764", {"start": v(7.64, 50.87) * mm, "end": v(7.66, 50.86) * mm});
            skLineSegment(sketch, "E765", {"start": v(7.66, 50.86) * mm, "end": v(7.68, 50.84) * mm});
            skLineSegment(sketch, "E766", {"start": v(7.68, 50.84) * mm, "end": v(7.76, 50.8) * mm});
            skLineSegment(sketch, "E767", {"start": v(7.76, 50.8) * mm, "end": v(7.88, 50.73) * mm});
            skLineSegment(sketch, "E768", {"start": v(7.88, 50.73) * mm, "end": v(7.99, 50.67) * mm});
            skLineSegment(sketch, "E769", {"start": v(7.99, 50.67) * mm, "end": v(8.1, 50.62) * mm});
            skLineSegment(sketch, "E770", {"start": v(8.1, 50.62) * mm, "end": v(8.22, 50.58) * mm});
            skLineSegment(sketch, "E771", {"start": v(8.22, 50.58) * mm, "end": v(8.33, 50.54) * mm});
            skLineSegment(sketch, "E772", {"start": v(8.33, 50.54) * mm, "end": v(8.45, 50.5) * mm});
            skLineSegment(sketch, "E773", {"start": v(8.45, 50.5) * mm, "end": v(8.57, 50.48) * mm});
            skLineSegment(sketch, "E774", {"start": v(8.57, 50.48) * mm, "end": v(8.7, 50.46) * mm});
            skLineSegment(sketch, "E775", {"start": v(8.7, 50.46) * mm, "end": v(8.75, 50.45) * mm});
            skLineSegment(sketch, "E776", {"start": v(8.75, 50.45) * mm, "end": v(9.1, 50.45) * mm});
            skLineSegment(sketch, "E777", {"start": v(9.1, 50.45) * mm, "end": v(9.16, 50.46) * mm});
            skLineSegment(sketch, "E778", {"start": v(9.16, 50.46) * mm, "end": v(9.29, 50.49) * mm});
            skLineSegment(sketch, "E779", {"start": v(9.29, 50.49) * mm, "end": v(9.41, 50.52) * mm});
            skLineSegment(sketch, "E780", {"start": v(9.41, 50.52) * mm, "end": v(9.54, 50.56) * mm});
            skLineSegment(sketch, "E781", {"start": v(9.54, 50.56) * mm, "end": v(9.67, 50.6) * mm});
            skLineSegment(sketch, "E782", {"start": v(9.67, 50.6) * mm, "end": v(9.7, 50.62) * mm});
            skLineSegment(sketch, "E783", {"start": v(9.7, 50.62) * mm, "end": v(9.77, 50.65) * mm});
            skLineSegment(sketch, "E784", {"start": v(9.77, 50.65) * mm, "end": v(9.91, 50.73) * mm});
            skLineSegment(sketch, "E785", {"start": v(9.91, 50.73) * mm, "end": v(9.99, 50.78) * mm});
            skLineSegment(sketch, "E786", {"start": v(9.99, 50.78) * mm, "end": v(10, 50.79) * mm});
            skLineSegment(sketch, "E787", {"start": v(10, 50.79) * mm, "end": v(10.04, 50.81) * mm});
            skLineSegment(sketch, "E788", {"start": v(10.04, 50.81) * mm, "end": v(10.06, 50.83) * mm});
            skLineSegment(sketch, "E789", {"start": v(10.06, 50.83) * mm, "end": v(10.06, 50.83) * mm});
            skLineSegment(sketch, "E790", {"start": v(10.06, 50.83) * mm, "end": v(10.1, 50.85) * mm});
            skLineSegment(sketch, "E791", {"start": v(10.1, 50.85) * mm, "end": v(10.11, 50.87) * mm});
            skLineSegment(sketch, "E792", {"start": v(10.11, 50.87) * mm, "end": v(10.22, 50.95) * mm});
            skLineSegment(sketch, "E793", {"start": v(10.22, 50.95) * mm, "end": v(9.97, 51.2) * mm});
            skLineSegment(sketch, "E794", {"start": v(9.97, 51.2) * mm, "end": v(9.95, 51.2) * mm});
            skLineSegment(sketch, "E795", {"start": v(9.95, 51.2) * mm, "end": v(9.86, 51.17) * mm});
            skLineSegment(sketch, "E796", {"start": v(9.86, 51.17) * mm, "end": v(9.78, 51.15) * mm});
            skLineSegment(sketch, "E797", {"start": v(9.78, 51.15) * mm, "end": v(9.71, 51.15) * mm});
            skLineSegment(sketch, "E798", {"start": v(9.71, 51.15) * mm, "end": v(9.64, 51.16) * mm});
            skLineSegment(sketch, "E799", {"start": v(9.64, 51.16) * mm, "end": v(9.6, 51.17) * mm});
            skLineSegment(sketch, "E800", {"start": v(9.6, 51.17) * mm, "end": v(9.57, 51.18) * mm});
            skLineSegment(sketch, "E801", {"start": v(9.57, 51.18) * mm, "end": v(9.54, 51.2) * mm});
            skLineSegment(sketch, "E802", {"start": v(9.54, 51.2) * mm, "end": v(9.5, 51.23) * mm});
            skLineSegment(sketch, "E803", {"start": v(9.5, 51.23) * mm, "end": v(9.46, 51.26) * mm});
            skLineSegment(sketch, "E804", {"start": v(9.46, 51.26) * mm, "end": v(7.08, 53.64) * mm});
            skLineSegment(sketch, "E805", {"start": v(7.08, 53.64) * mm, "end": v(7.06, 53.67) * mm});
            skLineSegment(sketch, "E806", {"start": v(7.06, 53.67) * mm, "end": v(7.02, 53.72) * mm});
            skLineSegment(sketch, "E807", {"start": v(7.02, 53.72) * mm, "end": v(7, 53.78) * mm});
            skLineSegment(sketch, "E808", {"start": v(7, 53.78) * mm, "end": v(6.98, 53.84) * mm});
            skLineSegment(sketch, "E809", {"start": v(6.98, 53.84) * mm, "end": v(6.98, 53.9) * mm});
            skLineSegment(sketch, "E810", {"start": v(6.98, 53.9) * mm, "end": v(6.98, 53.95) * mm});
            skLineSegment(sketch, "E811", {"start": v(6.98, 53.95) * mm, "end": v(6.99, 54) * mm});
            skLineSegment(sketch, "E812", {"start": v(6.99, 54) * mm, "end": v(7, 54.05) * mm});
            skLineSegment(sketch, "E813", {"start": v(7, 54.05) * mm, "end": v(7.02, 54.1) * mm});
            skLineSegment(sketch, "E814", {"start": v(7.02, 54.1) * mm, "end": v(7.03, 54.14) * mm});
            skLineSegment(sketch, "E815", {"start": v(7.03, 54.14) * mm, "end": v(6.78, 54.4) * mm});
            skLineSegment(sketch, "E816", {"start": v(6.78, 54.4) * mm, "end": v(6.76, 54.37) * mm});
            skLineSegment(sketch, "E817", {"start": v(6.76, 54.37) * mm, "end": v(6.75, 54.36) * mm});
            skLineSegment(sketch, "E818", {"start": v(6.75, 54.36) * mm, "end": v(6.75, 54.35) * mm});
            skLineSegment(sketch, "E819", {"start": v(6.75, 54.35) * mm, "end": v(6.75, 54.35) * mm});
            skLineSegment(sketch, "E820", {"start": v(6.75, 54.35) * mm, "end": v(6.74, 54.35) * mm});
            skLineSegment(sketch, "E821", {"start": v(6.74, 54.35) * mm, "end": v(6.7, 54.29) * mm});
            skLineSegment(sketch, "E822", {"start": v(6.7, 54.29) * mm, "end": v(6.61, 54.17) * mm});
            skLineSegment(sketch, "E823", {"start": v(6.61, 54.17) * mm, "end": v(6.54, 54.05) * mm});
            skLineSegment(sketch, "E824", {"start": v(6.54, 54.05) * mm, "end": v(6.47, 53.93) * mm});
            skLineSegment(sketch, "E825", {"start": v(6.47, 53.93) * mm, "end": v(6.42, 53.8) * mm});
            skLineSegment(sketch, "E826", {"start": v(6.42, 53.8) * mm, "end": v(6.37, 53.68) * mm});
            skLineSegment(sketch, "E827", {"start": v(6.37, 53.68) * mm, "end": v(6.34, 53.55) * mm});
            skLineSegment(sketch, "E828", {"start": v(6.34, 53.55) * mm, "end": v(6.3, 53.41) * mm});
            skLineSegment(sketch, "E829", {"start": v(6.3, 53.41) * mm, "end": v(6.29, 53.27) * mm});
            skLineSegment(sketch, "E830", {"start": v(6.29, 53.27) * mm, "end": v(6.28, 53.22) * mm});
            skLineSegment(sketch, "E831", {"start": v(6.28, 53.22) * mm, "end": v(6.28, 52.97) * mm});
            skLineSegment(sketch, "E832", {"start": v(6.28, 52.97) * mm, "end": v(6.29, 52.9) * mm});
            skLineSegment(sketch, "E833", {"start": v(6.29, 52.9) * mm, "end": v(6.3, 52.8) * mm});
            skLineSegment(sketch, "E834", {"start": v(6.3, 52.8) * mm, "end": v(6.32, 52.7) * mm});
            skLineSegment(sketch, "E835", {"start": v(6.32, 52.7) * mm, "end": v(6.34, 52.6) * mm});
            skLineSegment(sketch, "E836", {"start": v(6.34, 52.6) * mm, "end": v(6.37, 52.5) * mm});
            skLineSegment(sketch, "E837", {"start": v(6.37, 52.5) * mm, "end": v(6.4, 52.4) * mm});
            skLineSegment(sketch, "E838", {"start": v(6.4, 52.4) * mm, "end": v(6.43, 52.31) * mm});
            skLineSegment(sketch, "E839", {"start": v(6.43, 52.31) * mm, "end": v(6.47, 52.22) * mm});
            skLineSegment(sketch, "E840", {"start": v(6.47, 52.22) * mm, "end": v(6.52, 52.13) * mm});
            skLineSegment(sketch, "E841", {"start": v(6.52, 52.13) * mm, "end": v(6.55, 52.06) * mm});
            skLineSegment(sketch, "E842", {"start": v(6.55, 52.06) * mm, "end": v(6.54, 52.06) * mm});
            skLineSegment(sketch, "E843", {"start": v(6.54, 52.06) * mm, "end": v(6.5, 52.1) * mm});
            skLineSegment(sketch, "E844", {"start": v(6.5, 52.1) * mm, "end": v(6.43, 52.16) * mm});
            skLineSegment(sketch, "E845", {"start": v(6.43, 52.16) * mm, "end": v(6.4, 52.17) * mm});
            skLineSegment(sketch, "E846", {"start": v(6.4, 52.17) * mm, "end": v(6.4, 52.17) * mm});
            skLineSegment(sketch, "E847", {"start": v(6.4, 52.17) * mm, "end": v(6.4, 52.18) * mm});
            skLineSegment(sketch, "E848", {"start": v(6.4, 52.18) * mm, "end": v(6.36, 52.22) * mm});
            skLineSegment(sketch, "E849", {"start": v(6.36, 52.22) * mm, "end": v(6.28, 52.27) * mm});
            skLineSegment(sketch, "E850", {"start": v(6.28, 52.27) * mm, "end": v(6.21, 52.3) * mm});
            skLineSegment(sketch, "E851", {"start": v(6.21, 52.3) * mm, "end": v(6.15, 52.34) * mm});
            skLineSegment(sketch, "E852", {"start": v(6.15, 52.34) * mm, "end": v(6.07, 52.38) * mm});
            skLineSegment(sketch, "E853", {"start": v(6.07, 52.38) * mm, "end": v(6.01, 52.4) * mm});
            skLineSegment(sketch, "E854", {"start": v(6.01, 52.4) * mm, "end": v(5.95, 52.42) * mm});
            skLineSegment(sketch, "E855", {"start": v(5.95, 52.42) * mm, "end": v(5.89, 52.44) * mm});
            skLineSegment(sketch, "E856", {"start": v(5.89, 52.44) * mm, "end": v(5.82, 52.45) * mm});
            skLineSegment(sketch, "E857", {"start": v(5.82, 52.45) * mm, "end": v(5.76, 52.46) * mm});
            skLineSegment(sketch, "E858", {"start": v(5.76, 52.46) * mm, "end": v(5.7, 52.47) * mm});
            skLineSegment(sketch, "E859", {"start": v(5.7, 52.47) * mm, "end": v(5.63, 52.47) * mm});
            skLineSegment(sketch, "E860", {"start": v(5.63, 52.47) * mm, "end": v(5.56, 52.47) * mm});
            skLineSegment(sketch, "E861", {"start": v(5.56, 52.47) * mm, "end": v(5.43, 52.45) * mm});
            skLineSegment(sketch, "E862", {"start": v(5.43, 52.45) * mm, "end": v(5.3, 52.43) * mm});
            skLineSegment(sketch, "E863", {"start": v(5.3, 52.43) * mm, "end": v(5.16, 52.39) * mm});
            skLineSegment(sketch, "E864", {"start": v(5.16, 52.39) * mm, "end": v(5.03, 52.33) * mm});
            skLineSegment(sketch, "E865", {"start": v(5.03, 52.33) * mm, "end": v(4.92, 52.28) * mm});
            skLineSegment(sketch, "E866", {"start": v(4.92, 52.28) * mm, "end": v(4.8, 52.2) * mm});
            skLineSegment(sketch, "E867", {"start": v(4.8, 52.2) * mm, "end": v(4.7, 52.13) * mm});
            skLineSegment(sketch, "E868", {"start": v(4.7, 52.13) * mm, "end": v(4.6, 52.05) * mm});
            skLineSegment(sketch, "E869", {"start": v(4.6, 52.05) * mm, "end": v(4.55, 52) * mm});
            skLineSegment(sketch, "E870", {"start": v(4.55, 52) * mm, "end": v(4.43, 51.9) * mm});
            skLineSegment(sketch, "E871", {"start": v(4.43, 51.9) * mm, "end": v(4.4, 51.87) * mm});
            skLineSegment(sketch, "E872", {"start": v(4.4, 51.87) * mm, "end": v(4.23, 51.71) * mm});
            skLineSegment(sketch, "E873", {"start": v(4.23, 51.71) * mm, "end": v(4.49, 51.46) * mm});
            skLineSegment(sketch, "E874", {"start": v(4.49, 51.46) * mm, "end": v(4.52, 51.48) * mm});
            skLineSegment(sketch, "E875", {"start": v(4.52, 51.48) * mm, "end": v(4.58, 51.51) * mm});
            skLineSegment(sketch, "E876", {"start": v(4.58, 51.51) * mm, "end": v(4.64, 51.54) * mm});
            skLineSegment(sketch, "E877", {"start": v(4.64, 51.54) * mm, "end": v(4.7, 51.55) * mm});
            skLineSegment(sketch, "E878", {"start": v(4.7, 51.55) * mm, "end": v(4.77, 51.55) * mm});
            skLineSegment(sketch, "E879", {"start": v(4.77, 51.55) * mm, "end": v(4.83, 51.54) * mm});
            skLineSegment(sketch, "E880", {"start": v(4.83, 51.54) * mm, "end": v(4.9, 51.52) * mm});
            skLineSegment(sketch, "E881", {"start": v(4.9, 51.52) * mm, "end": v(4.97, 51.48) * mm});
            skLineSegment(sketch, "E882", {"start": v(4.97, 51.48) * mm, "end": v(5.03, 51.44) * mm});
            skLineSegment(sketch, "E883", {"start": v(5.03, 51.44) * mm, "end": v(5.09, 51.4) * mm});
            skLineSegment(sketch, "E884", {"start": v(5.09, 51.4) * mm, "end": v(5.91, 50.58) * mm});
            skLineSegment(sketch, "E885", {"start": v(5.91, 50.58) * mm, "end": v(5.96, 50.53) * mm});
            skLineSegment(sketch, "E886", {"start": v(5.96, 50.53) * mm, "end": v(6.03, 50.44) * mm});
            skLineSegment(sketch, "E887", {"start": v(6.03, 50.44) * mm, "end": v(6.05, 50.4) * mm});
            skLineSegment(sketch, "E888", {"start": v(6.05, 50.4) * mm, "end": v(6.08, 50.36) * mm});
            skLineSegment(sketch, "E889", {"start": v(6.08, 50.36) * mm, "end": v(6.1, 50.33) * mm});
            skLineSegment(sketch, "E890", {"start": v(6.1, 50.33) * mm, "end": v(6.1, 50.29) * mm});
            skLineSegment(sketch, "E891", {"start": v(6.1, 50.29) * mm, "end": v(6.11, 50.25) * mm});
            skLineSegment(sketch, "E892", {"start": v(6.11, 50.25) * mm, "end": v(6.11, 50.2) * mm});
            skLineSegment(sketch, "E893", {"start": v(6.11, 50.2) * mm, "end": v(6.11, 50.15) * mm});
            skLineSegment(sketch, "E894", {"start": v(6.11, 50.15) * mm, "end": v(6.1, 50.1) * mm});
            skLineSegment(sketch, "E895", {"start": v(6.1, 50.1) * mm, "end": v(6.08, 50.03) * mm});
            skLineSegment(sketch, "E896", {"start": v(6.08, 50.03) * mm, "end": v(6.05, 49.97) * mm});
            skLineSegment(sketch, "E897", {"start": v(6.05, 49.97) * mm, "end": v(6.02, 49.93) * mm});
            skLineSegment(sketch, "E898", {"start": v(6.02, 49.93) * mm, "end": v(6.02, 49.92) * mm});
            skLineSegment(sketch, "E899", {"start": v(-5.16, 49.77) * mm, "end": v(-5.16, 49.77) * mm});
            skLineSegment(sketch, "E900", {"start": v(-5.16, 49.77) * mm, "end": v(-5.16, 49.76) * mm});
            skLineSegment(sketch, "E901", {"start": v(-5.16, 49.76) * mm, "end": v(-5.16, 49.77) * mm});
            skLineSegment(sketch, "E902", {"start": v(-2.14, 48.21) * mm, "end": v(-2.06, 48.2) * mm});
            skLineSegment(sketch, "E903", {"start": v(-2.06, 48.2) * mm, "end": v(-1.74, 48.21) * mm});
            skLineSegment(sketch, "E904", {"start": v(-1.74, 48.21) * mm, "end": v(-1.67, 48.22) * mm});
            skLineSegment(sketch, "E905", {"start": v(-1.67, 48.22) * mm, "end": v(-1.49, 48.24) * mm});
            skLineSegment(sketch, "E906", {"start": v(-1.49, 48.24) * mm, "end": v(-1.3, 48.27) * mm});
            skLineSegment(sketch, "E907", {"start": v(-1.3, 48.27) * mm, "end": v(-1.13, 48.3) * mm});
            skLineSegment(sketch, "E908", {"start": v(-1.13, 48.3) * mm, "end": v(-0.95, 48.36) * mm});
            skLineSegment(sketch, "E909", {"start": v(-0.95, 48.36) * mm, "end": v(-0.78, 48.42) * mm});
            skLineSegment(sketch, "E910", {"start": v(-0.78, 48.42) * mm, "end": v(-0.6, 48.49) * mm});
            skLineSegment(sketch, "E911", {"start": v(-0.6, 48.49) * mm, "end": v(-0.44, 48.57) * mm});
            skLineSegment(sketch, "E912", {"start": v(-0.44, 48.57) * mm, "end": v(-0.27, 48.66) * mm});
            skLineSegment(sketch, "E913", {"start": v(-0.27, 48.66) * mm, "end": v(-0.2, 48.7) * mm});
            skLineSegment(sketch, "E914", {"start": v(-0.2, 48.7) * mm, "end": v(-0.12, 48.75) * mm});
            skLineSegment(sketch, "E915", {"start": v(-0.12, 48.75) * mm, "end": v(-0.12, 48.75) * mm});
            skLineSegment(sketch, "E916", {"start": v(-0.12, 48.75) * mm, "end": v(-0.1, 48.75) * mm});
            skLineSegment(sketch, "E917", {"start": v(-0.1, 48.75) * mm, "end": v(0, 48.82) * mm});
            skLineSegment(sketch, "E918", {"start": v(0, 48.82) * mm, "end": v(0.18, 48.95) * mm});
            skLineSegment(sketch, "E919", {"start": v(0.18, 48.95) * mm, "end": v(0.27, 49.01) * mm});
            skLineSegment(sketch, "E920", {"start": v(0.27, 49.01) * mm, "end": v(0.36, 49.1) * mm});
            skLineSegment(sketch, "E921", {"start": v(0.36, 49.1) * mm, "end": v(-0.1, 49.55) * mm});
            skLineSegment(sketch, "E922", {"start": v(-0.1, 49.55) * mm, "end": v(-0.15, 49.52) * mm});
            skLineSegment(sketch, "E923", {"start": v(-0.15, 49.52) * mm, "end": v(-0.25, 49.49) * mm});
            skLineSegment(sketch, "E924", {"start": v(-0.25, 49.49) * mm, "end": v(-0.34, 49.46) * mm});
            skLineSegment(sketch, "E925", {"start": v(-0.34, 49.46) * mm, "end": v(-0.4, 49.45) * mm});
            skLineSegment(sketch, "E926", {"start": v(-0.4, 49.45) * mm, "end": v(-0.47, 49.45) * mm});
            skLineSegment(sketch, "E927", {"start": v(-0.47, 49.45) * mm, "end": v(-0.55, 49.45) * mm});
            skLineSegment(sketch, "E928", {"start": v(-0.55, 49.45) * mm, "end": v(-0.6, 49.45) * mm});
            skLineSegment(sketch, "E929", {"start": v(-0.6, 49.45) * mm, "end": v(-0.68, 49.47) * mm});
            skLineSegment(sketch, "E930", {"start": v(-0.68, 49.47) * mm, "end": v(-0.75, 49.5) * mm});
            skLineSegment(sketch, "E931", {"start": v(-0.75, 49.5) * mm, "end": v(-0.83, 49.53) * mm});
            skLineSegment(sketch, "E932", {"start": v(-0.83, 49.53) * mm, "end": v(-0.9, 49.57) * mm});
            skLineSegment(sketch, "E933", {"start": v(-0.9, 49.57) * mm, "end": v(-0.94, 49.6) * mm});
            skLineSegment(sketch, "E934", {"start": v(-0.94, 49.6) * mm, "end": v(-0.95, 49.6) * mm});
            skLineSegment(sketch, "E935", {"start": v(-0.95, 49.6) * mm, "end": v(-0.95, 49.61) * mm});
            skLineSegment(sketch, "E936", {"start": v(-0.95, 49.61) * mm, "end": v(-0.97, 49.63) * mm});
            skLineSegment(sketch, "E937", {"start": v(-0.97, 49.63) * mm, "end": v(-1, 49.65) * mm});
            skLineSegment(sketch, "E938", {"start": v(-1, 49.65) * mm, "end": v(-5.2, 53.86) * mm});
            skLineSegment(sketch, "E939", {"start": v(-5.2, 53.86) * mm, "end": v(-5.23, 53.9) * mm});
            skLineSegment(sketch, "E940", {"start": v(-5.23, 53.9) * mm, "end": v(-5.3, 53.98) * mm});
            skLineSegment(sketch, "E941", {"start": v(-5.3, 53.98) * mm, "end": v(-5.32, 54.03) * mm});
            skLineSegment(sketch, "E942", {"start": v(-5.32, 54.03) * mm, "end": v(-5.35, 54.07) * mm});
            skLineSegment(sketch, "E943", {"start": v(-5.35, 54.07) * mm, "end": v(-5.37, 54.12) * mm});
            skLineSegment(sketch, "E944", {"start": v(-5.37, 54.12) * mm, "end": v(-5.38, 54.17) * mm});
            skLineSegment(sketch, "E945", {"start": v(-5.38, 54.17) * mm, "end": v(-5.4, 54.21) * mm});
            skLineSegment(sketch, "E946", {"start": v(-5.4, 54.21) * mm, "end": v(-5.4, 54.26) * mm});
            skLineSegment(sketch, "E947", {"start": v(-5.4, 54.26) * mm, "end": v(-5.4, 54.31) * mm});
            skLineSegment(sketch, "E948", {"start": v(-5.4, 54.31) * mm, "end": v(-5.4, 54.36) * mm});
            skLineSegment(sketch, "E949", {"start": v(-5.4, 54.36) * mm, "end": v(-5.4, 54.41) * mm});
            skLineSegment(sketch, "E950", {"start": v(-5.4, 54.41) * mm, "end": v(-5.4, 54.47) * mm});
            skLineSegment(sketch, "E951", {"start": v(-5.4, 54.47) * mm, "end": v(-5.37, 54.57) * mm});
            skLineSegment(sketch, "E952", {"start": v(-5.37, 54.57) * mm, "end": v(-5.34, 54.69) * mm});
            skLineSegment(sketch, "E953", {"start": v(-5.34, 54.69) * mm, "end": v(-5.3, 54.76) * mm});
            skLineSegment(sketch, "E954", {"start": v(-5.3, 54.76) * mm, "end": v(-5.76, 55.22) * mm});
            skLineSegment(sketch, "E955", {"start": v(-5.76, 55.22) * mm, "end": v(-5.77, 55.2) * mm});
            skLineSegment(sketch, "E956", {"start": v(-5.77, 55.2) * mm, "end": v(-5.8, 55.17) * mm});
            skLineSegment(sketch, "E957", {"start": v(-5.8, 55.17) * mm, "end": v(-5.81, 55.15) * mm});
            skLineSegment(sketch, "E958", {"start": v(-5.81, 55.15) * mm, "end": v(-5.85, 55.1) * mm});
            skLineSegment(sketch, "E959", {"start": v(-5.85, 55.1) * mm, "end": v(-5.92, 55) * mm});
            skLineSegment(sketch, "E960", {"start": v(-5.92, 55) * mm, "end": v(-6, 54.9) * mm});
            skLineSegment(sketch, "E961", {"start": v(-6, 54.9) * mm, "end": v(-6.03, 54.85) * mm});
            skLineSegment(sketch, "E962", {"start": v(-6.03, 54.85) * mm, "end": v(-6.03, 54.85) * mm});
            skLineSegment(sketch, "E963", {"start": v(-6.03, 54.85) * mm, "end": v(-6.04, 54.84) * mm});
            skLineSegment(sketch, "E964", {"start": v(-6.04, 54.84) * mm, "end": v(-6.06, 54.8) * mm});
            skLineSegment(sketch, "E965", {"start": v(-6.06, 54.8) * mm, "end": v(-6.08, 54.78) * mm});
            skLineSegment(sketch, "E966", {"start": v(-6.08, 54.78) * mm, "end": v(-6.08, 54.77) * mm});
            skLineSegment(sketch, "E967", {"start": v(-6.08, 54.77) * mm, "end": v(-6.08, 54.76) * mm});
            skLineSegment(sketch, "E968", {"start": v(-6.08, 54.76) * mm, "end": v(-6.08, 54.77) * mm});
            skLineSegment(sketch, "E969", {"start": v(-6.08, 54.77) * mm, "end": v(-6.09, 54.76) * mm});
            skLineSegment(sketch, "E970", {"start": v(-6.09, 54.76) * mm, "end": v(-6.1, 54.75) * mm});
            skLineSegment(sketch, "E971", {"start": v(-6.1, 54.75) * mm, "end": v(-6.1, 54.74) * mm});
            skLineSegment(sketch, "E972", {"start": v(-6.1, 54.74) * mm, "end": v(-6.1, 54.72) * mm});
            skLineSegment(sketch, "E973", {"start": v(-6.1, 54.72) * mm, "end": v(-6.1, 54.72) * mm});
            skLineSegment(sketch, "E974", {"start": v(-6.1, 54.72) * mm, "end": v(-6.11, 54.73) * mm});
            skLineSegment(sketch, "E975", {"start": v(-6.11, 54.73) * mm, "end": v(-6.16, 54.65) * mm});
            skLineSegment(sketch, "E976", {"start": v(-6.16, 54.65) * mm, "end": v(-6.22, 54.53) * mm});
            skLineSegment(sketch, "E977", {"start": v(-6.22, 54.53) * mm, "end": v(-6.29, 54.4) * mm});
            skLineSegment(sketch, "E978", {"start": v(-6.29, 54.4) * mm, "end": v(-6.35, 54.28) * mm});
            skLineSegment(sketch, "E979", {"start": v(-6.35, 54.28) * mm, "end": v(-6.4, 54.15) * mm});
            skLineSegment(sketch, "E980", {"start": v(-6.4, 54.15) * mm, "end": v(-6.45, 54.04) * mm});
            skLineSegment(sketch, "E981", {"start": v(-6.45, 54.04) * mm, "end": v(-6.48, 53.93) * mm});
            skLineSegment(sketch, "E982", {"start": v(-6.48, 53.93) * mm, "end": v(-6.52, 53.82) * mm});
            skLineSegment(sketch, "E983", {"start": v(-6.52, 53.82) * mm, "end": v(-6.55, 53.71) * mm});
            skLineSegment(sketch, "E984", {"start": v(-6.55, 53.71) * mm, "end": v(-6.57, 53.6) * mm});
            skLineSegment(sketch, "E985", {"start": v(-6.57, 53.6) * mm, "end": v(-6.6, 53.48) * mm});
            skLineSegment(sketch, "E986", {"start": v(-6.6, 53.48) * mm, "end": v(-6.61, 53.36) * mm});
            skLineSegment(sketch, "E987", {"start": v(-6.61, 53.36) * mm, "end": v(-6.63, 53.24) * mm});
            skLineSegment(sketch, "E988", {"start": v(-6.63, 53.24) * mm, "end": v(-6.64, 53.15) * mm});
            skLineSegment(sketch, "E989", {"start": v(-6.64, 53.15) * mm, "end": v(-6.64, 52.68) * mm});
            skLineSegment(sketch, "E990", {"start": v(-6.64, 52.68) * mm, "end": v(-6.63, 52.61) * mm});
            skLineSegment(sketch, "E991", {"start": v(-6.63, 52.61) * mm, "end": v(-6.62, 52.47) * mm});
            skLineSegment(sketch, "E992", {"start": v(-6.62, 52.47) * mm, "end": v(-6.6, 52.33) * mm});
            skLineSegment(sketch, "E993", {"start": v(-6.6, 52.33) * mm, "end": v(-6.57, 52.19) * mm});
            skLineSegment(sketch, "E994", {"start": v(-6.57, 52.19) * mm, "end": v(-6.54, 52.05) * mm});
            skLineSegment(sketch, "E995", {"start": v(-6.54, 52.05) * mm, "end": v(-6.5, 51.92) * mm});
            skLineSegment(sketch, "E996", {"start": v(-6.5, 51.92) * mm, "end": v(-6.46, 51.78) * mm});
            skLineSegment(sketch, "E997", {"start": v(-6.46, 51.78) * mm, "end": v(-6.42, 51.65) * mm});
            skLineSegment(sketch, "E998", {"start": v(-6.42, 51.65) * mm, "end": v(-6.36, 51.51) * mm});
            skLineSegment(sketch, "E999", {"start": v(-6.36, 51.51) * mm, "end": v(-6.32, 51.42) * mm});
            skLineSegment(sketch, "E1000", {"start": v(-6.32, 51.42) * mm, "end": v(-6.28, 51.32) * mm});
            skLineSegment(sketch, "E1001", {"start": v(-6.28, 51.32) * mm, "end": v(-6.28, 51.32) * mm});
            skLineSegment(sketch, "E1002", {"start": v(-6.28, 51.32) * mm, "end": v(-6.24, 51.23) * mm});
            skLineSegment(sketch, "E1003", {"start": v(-6.24, 51.23) * mm, "end": v(-6.15, 51.05) * mm});
            skLineSegment(sketch, "E1004", {"start": v(-6.15, 51.05) * mm, "end": v(-6.04, 50.87) * mm});
            skLineSegment(sketch, "E1005", {"start": v(-6.04, 50.87) * mm, "end": v(-5.93, 50.68) * mm});
            skLineSegment(sketch, "E1006", {"start": v(-5.93, 50.68) * mm, "end": v(-5.82, 50.52) * mm});
            skLineSegment(sketch, "E1007", {"start": v(-5.82, 50.52) * mm, "end": v(-5.77, 50.46) * mm});
            skLineSegment(sketch, "E1008", {"start": v(-5.77, 50.46) * mm, "end": v(-5.77, 50.44) * mm});
            skLineSegment(sketch, "E1009", {"start": v(-5.77, 50.44) * mm, "end": v(-5.73, 50.4) * mm});
            skLineSegment(sketch, "E1010", {"start": v(-5.73, 50.4) * mm, "end": v(-5.7, 50.37) * mm});
            skLineSegment(sketch, "E1011", {"start": v(-5.7, 50.37) * mm, "end": v(-5.64, 50.28) * mm});
            skLineSegment(sketch, "E1012", {"start": v(-5.64, 50.28) * mm, "end": v(-5.5, 50.11) * mm});
            skLineSegment(sketch, "E1013", {"start": v(-5.5, 50.11) * mm, "end": v(-5.44, 50.04) * mm});
            skLineSegment(sketch, "E1014", {"start": v(-5.44, 50.04) * mm, "end": v(-5.4, 50) * mm});
            skLineSegment(sketch, "E1015", {"start": v(-5.4, 50) * mm, "end": v(-5.23, 49.8) * mm});
            skLineSegment(sketch, "E1016", {"start": v(-5.23, 49.8) * mm, "end": v(-5.03, 49.61) * mm});
            skLineSegment(sketch, "E1017", {"start": v(-5.03, 49.61) * mm, "end": v(-4.83, 49.43) * mm});
            skLineSegment(sketch, "E1018", {"start": v(-4.83, 49.43) * mm, "end": v(-4.64, 49.26) * mm});
            skLineSegment(sketch, "E1019", {"start": v(-4.64, 49.26) * mm, "end": v(-4.57, 49.21) * mm});
            skLineSegment(sketch, "E1020", {"start": v(-4.57, 49.21) * mm, "end": v(-4.56, 49.2) * mm});
            skLineSegment(sketch, "E1021", {"start": v(-4.56, 49.2) * mm, "end": v(-4.42, 49.1) * mm});
            skLineSegment(sketch, "E1022", {"start": v(-4.42, 49.1) * mm, "end": v(-4.36, 49.05) * mm});
            skLineSegment(sketch, "E1023", {"start": v(-4.36, 49.05) * mm, "end": v(-4.32, 49.02) * mm});
            skLineSegment(sketch, "E1024", {"start": v(-4.32, 49.02) * mm, "end": v(-4.24, 48.97) * mm});
            skLineSegment(sketch, "E1025", {"start": v(-4.24, 48.97) * mm, "end": v(-4.08, 48.87) * mm});
            skLineSegment(sketch, "E1026", {"start": v(-4.08, 48.87) * mm, "end": v(-3.92, 48.77) * mm});
            skLineSegment(sketch, "E1027", {"start": v(-3.92, 48.77) * mm, "end": v(-3.85, 48.73) * mm});
            skLineSegment(sketch, "E1028", {"start": v(-3.85, 48.73) * mm, "end": v(-3.82, 48.72) * mm});
            skLineSegment(sketch, "E1029", {"start": v(-3.82, 48.72) * mm, "end": v(-3.8, 48.7) * mm});
            skLineSegment(sketch, "E1030", {"start": v(-3.8, 48.7) * mm, "end": v(-3.79, 48.7) * mm});
            skLineSegment(sketch, "E1031", {"start": v(-3.79, 48.7) * mm, "end": v(-3.78, 48.7) * mm});
            skLineSegment(sketch, "E1032", {"start": v(-3.78, 48.7) * mm, "end": v(-3.78, 48.7) * mm});
            skLineSegment(sketch, "E1033", {"start": v(-3.78, 48.7) * mm, "end": v(-3.79, 48.7) * mm});
            skLineSegment(sketch, "E1034", {"start": v(-3.79, 48.7) * mm, "end": v(-3.68, 48.64) * mm});
            skLineSegment(sketch, "E1035", {"start": v(-3.68, 48.64) * mm, "end": v(-3.49, 48.55) * mm});
            skLineSegment(sketch, "E1036", {"start": v(-3.49, 48.55) * mm, "end": v(-3.3, 48.47) * mm});
            skLineSegment(sketch, "E1037", {"start": v(-3.3, 48.47) * mm, "end": v(-3.1, 48.4) * mm});
            skLineSegment(sketch, "E1038", {"start": v(-3.1, 48.4) * mm, "end": v(-2.91, 48.34) * mm});
            skLineSegment(sketch, "E1039", {"start": v(-2.91, 48.34) * mm, "end": v(-2.72, 48.3) * mm});
            skLineSegment(sketch, "E1040", {"start": v(-2.72, 48.3) * mm, "end": v(-2.53, 48.26) * mm});
            skLineSegment(sketch, "E1041", {"start": v(-2.53, 48.26) * mm, "end": v(-2.34, 48.23) * mm});
            skLineSegment(sketch, "E1042", {"start": v(-2.34, 48.23) * mm, "end": v(-2.14, 48.21) * mm});
            skLineSegment(sketch, "E1043", {"start": v(0.27, 49.9) * mm, "end": v(0.72, 49.45) * mm});
            skLineSegment(sketch, "E1044", {"start": v(0.72, 49.45) * mm, "end": v(0.72, 49.45) * mm});
            skLineSegment(sketch, "E1045", {"start": v(0.72, 49.45) * mm, "end": v(0.8, 49.54) * mm});
            skLineSegment(sketch, "E1046", {"start": v(0.8, 49.54) * mm, "end": v(0.83, 49.6) * mm});
            skLineSegment(sketch, "E1047", {"start": v(0.83, 49.6) * mm, "end": v(0.86, 49.62) * mm});
            skLineSegment(sketch, "E1048", {"start": v(0.86, 49.62) * mm, "end": v(0.9, 49.7) * mm});
            skLineSegment(sketch, "E1049", {"start": v(0.9, 49.7) * mm, "end": v(1, 49.83) * mm});
            skLineSegment(sketch, "E1050", {"start": v(1, 49.83) * mm, "end": v(1.06, 49.91) * mm});
            skLineSegment(sketch, "E1051", {"start": v(1.06, 49.91) * mm, "end": v(1.07, 49.93) * mm});
            skLineSegment(sketch, "E1052", {"start": v(1.07, 49.93) * mm, "end": v(1.11, 50) * mm});
            skLineSegment(sketch, "E1053", {"start": v(1.11, 50) * mm, "end": v(1.18, 50.11) * mm});
            skLineSegment(sketch, "E1054", {"start": v(1.18, 50.11) * mm, "end": v(1.2, 50.15) * mm});
            skLineSegment(sketch, "E1055", {"start": v(1.2, 50.15) * mm, "end": v(1.24, 50.24) * mm});
            skLineSegment(sketch, "E1056", {"start": v(1.24, 50.24) * mm, "end": v(1.3, 50.38) * mm});
            skLineSegment(sketch, "E1057", {"start": v(1.3, 50.38) * mm, "end": v(1.37, 50.52) * mm});
            skLineSegment(sketch, "E1058", {"start": v(1.37, 50.52) * mm, "end": v(1.42, 50.67) * mm});
            skLineSegment(sketch, "E1059", {"start": v(1.42, 50.67) * mm, "end": v(1.47, 50.81) * mm});
            skLineSegment(sketch, "E1060", {"start": v(1.47, 50.81) * mm, "end": v(1.5, 50.96) * mm});
            skLineSegment(sketch, "E1061", {"start": v(1.5, 50.96) * mm, "end": v(1.54, 51.11) * mm});
            skLineSegment(sketch, "E1062", {"start": v(1.54, 51.11) * mm, "end": v(1.57, 51.27) * mm});
            skLineSegment(sketch, "E1063", {"start": v(1.57, 51.27) * mm, "end": v(1.59, 51.42) * mm});
            skLineSegment(sketch, "E1064", {"start": v(1.59, 51.42) * mm, "end": v(1.6, 51.5) * mm});
            skLineSegment(sketch, "E1065", {"start": v(1.6, 51.5) * mm, "end": v(1.6, 51.63) * mm});
            skLineSegment(sketch, "E1066", {"start": v(1.6, 51.63) * mm, "end": v(1.6, 51.76) * mm});
            skLineSegment(sketch, "E1067", {"start": v(1.6, 51.76) * mm, "end": v(1.6, 51.88) * mm});
            skLineSegment(sketch, "E1068", {"start": v(1.6, 51.88) * mm, "end": v(1.6, 52.01) * mm});
            skLineSegment(sketch, "E1069", {"start": v(1.6, 52.01) * mm, "end": v(1.59, 52.1) * mm});
            skLineSegment(sketch, "E1070", {"start": v(1.59, 52.1) * mm, "end": v(1.57, 52.22) * mm});
            skLineSegment(sketch, "E1071", {"start": v(1.57, 52.22) * mm, "end": v(1.56, 52.35) * mm});
            skLineSegment(sketch, "E1072", {"start": v(1.56, 52.35) * mm, "end": v(1.53, 52.47) * mm});
            skLineSegment(sketch, "E1073", {"start": v(1.53, 52.47) * mm, "end": v(1.5, 52.6) * mm});
            skLineSegment(sketch, "E1074", {"start": v(1.5, 52.6) * mm, "end": v(1.47, 52.72) * mm});
            skLineSegment(sketch, "E1075", {"start": v(1.47, 52.72) * mm, "end": v(1.44, 52.84) * mm});
            skLineSegment(sketch, "E1076", {"start": v(1.44, 52.84) * mm, "end": v(1.4, 52.97) * mm});
            skLineSegment(sketch, "E1077", {"start": v(1.4, 52.97) * mm, "end": v(1.35, 53.1) * mm});
            skLineSegment(sketch, "E1078", {"start": v(1.35, 53.1) * mm, "end": v(1.28, 53.25) * mm});
            skLineSegment(sketch, "E1079", {"start": v(1.28, 53.25) * mm, "end": v(1.2, 53.41) * mm});
            skLineSegment(sketch, "E1080", {"start": v(1.2, 53.41) * mm, "end": v(1.13, 53.58) * mm});
            skLineSegment(sketch, "E1081", {"start": v(1.13, 53.58) * mm, "end": v(1.05, 53.73) * mm});
            skLineSegment(sketch, "E1082", {"start": v(1.05, 53.73) * mm, "end": v(0.99, 53.83) * mm});
            skLineSegment(sketch, "E1083", {"start": v(0.99, 53.83) * mm, "end": v(0.93, 53.93) * mm});
            skLineSegment(sketch, "E1084", {"start": v(0.93, 53.93) * mm, "end": v(0.87, 54.01) * mm});
            skLineSegment(sketch, "E1085", {"start": v(0.87, 54.01) * mm, "end": v(0.78, 54.15) * mm});
            skLineSegment(sketch, "E1086", {"start": v(0.78, 54.15) * mm, "end": v(0.73, 54.21) * mm});
            skLineSegment(sketch, "E1087", {"start": v(0.73, 54.21) * mm, "end": v(0.6, 54.4) * mm});
            skLineSegment(sketch, "E1088", {"start": v(0.6, 54.4) * mm, "end": v(0.57, 54.42) * mm});
            skLineSegment(sketch, "E1089", {"start": v(0.57, 54.42) * mm, "end": v(0.56, 54.44) * mm});
            skLineSegment(sketch, "E1090", {"start": v(0.56, 54.44) * mm, "end": v(0.56, 54.44) * mm});
            skLineSegment(sketch, "E1091", {"start": v(0.56, 54.44) * mm, "end": v(0.46, 54.57) * mm});
            skLineSegment(sketch, "E1092", {"start": v(0.46, 54.57) * mm, "end": v(0.44, 54.58) * mm});
            skLineSegment(sketch, "E1093", {"start": v(0.44, 54.58) * mm, "end": v(0.43, 54.6) * mm});
            skLineSegment(sketch, "E1094", {"start": v(0.43, 54.6) * mm, "end": v(0.42, 54.6) * mm});
            skLineSegment(sketch, "E1095", {"start": v(0.42, 54.6) * mm, "end": v(0.38, 54.65) * mm});
            skLineSegment(sketch, "E1096", {"start": v(0.38, 54.65) * mm, "end": v(0.24, 54.8) * mm});
            skLineSegment(sketch, "E1097", {"start": v(0.24, 54.8) * mm, "end": v(0.2, 54.85) * mm});
            skLineSegment(sketch, "E1098", {"start": v(0.2, 54.85) * mm, "end": v(0.1, 54.95) * mm});
            skLineSegment(sketch, "E1099", {"start": v(0.1, 54.95) * mm, "end": v(-0.08, 55.13) * mm});
            skLineSegment(sketch, "E1100", {"start": v(-0.08, 55.13) * mm, "end": v(-0.18, 55.21) * mm});
            skLineSegment(sketch, "E1101", {"start": v(-0.18, 55.21) * mm, "end": v(-0.24, 55.27) * mm});
            skLineSegment(sketch, "E1102", {"start": v(-0.24, 55.27) * mm, "end": v(-0.5, 55.48) * mm});
            skLineSegment(sketch, "E1103", {"start": v(-0.5, 55.48) * mm, "end": v(-0.62, 55.57) * mm});
            skLineSegment(sketch, "E1104", {"start": v(-0.62, 55.57) * mm, "end": v(-0.7, 55.63) * mm});
            skLineSegment(sketch, "E1105", {"start": v(-0.7, 55.63) * mm, "end": v(-0.72, 55.64) * mm});
            skLineSegment(sketch, "E1106", {"start": v(-0.72, 55.64) * mm, "end": v(-0.8, 55.7) * mm});
            skLineSegment(sketch, "E1107", {"start": v(-0.8, 55.7) * mm, "end": v(-0.96, 55.8) * mm});
            skLineSegment(sketch, "E1108", {"start": v(-0.96, 55.8) * mm, "end": v(-1.03, 55.84) * mm});
            skLineSegment(sketch, "E1109", {"start": v(-1.03, 55.84) * mm, "end": v(-1.03, 55.84) * mm});
            skLineSegment(sketch, "E1110", {"start": v(-1.03, 55.84) * mm, "end": v(-1.03, 55.85) * mm});
            skLineSegment(sketch, "E1111", {"start": v(-1.03, 55.85) * mm, "end": v(-1.1, 55.88) * mm});
            skLineSegment(sketch, "E1112", {"start": v(-1.1, 55.88) * mm, "end": v(-1.26, 55.97) * mm});
            skLineSegment(sketch, "E1113", {"start": v(-1.26, 55.97) * mm, "end": v(-1.36, 56.02) * mm});
            skLineSegment(sketch, "E1114", {"start": v(-1.36, 56.02) * mm, "end": v(-1.4, 56.05) * mm});
            skLineSegment(sketch, "E1115", {"start": v(-1.4, 56.05) * mm, "end": v(-1.61, 56.14) * mm});
            skLineSegment(sketch, "E1116", {"start": v(-1.61, 56.14) * mm, "end": v(-1.8, 56.22) * mm});
            skLineSegment(sketch, "E1117", {"start": v(-1.8, 56.22) * mm, "end": v(-1.92, 56.26) * mm});
            skLineSegment(sketch, "E1118", {"start": v(-1.92, 56.26) * mm, "end": v(-2.04, 56.3) * mm});
            skLineSegment(sketch, "E1119", {"start": v(-2.04, 56.3) * mm, "end": v(-2.17, 56.33) * mm});
            skLineSegment(sketch, "E1120", {"start": v(-2.17, 56.33) * mm, "end": v(-2.3, 56.36) * mm});
            skLineSegment(sketch, "E1121", {"start": v(-2.3, 56.36) * mm, "end": v(-2.41, 56.4) * mm});
            skLineSegment(sketch, "E1122", {"start": v(-2.41, 56.4) * mm, "end": v(-2.54, 56.41) * mm});
            skLineSegment(sketch, "E1123", {"start": v(-2.54, 56.41) * mm, "end": v(-2.66, 56.43) * mm});
            skLineSegment(sketch, "E1124", {"start": v(-2.66, 56.43) * mm, "end": v(-2.79, 56.44) * mm});
            skLineSegment(sketch, "E1125", {"start": v(-2.79, 56.44) * mm, "end": v(-2.88, 56.45) * mm});
            skLineSegment(sketch, "E1126", {"start": v(-2.88, 56.45) * mm, "end": v(-3.18, 56.46) * mm});
            skLineSegment(sketch, "E1127", {"start": v(-3.18, 56.46) * mm, "end": v(-3.28, 56.45) * mm});
            skLineSegment(sketch, "E1128", {"start": v(-3.28, 56.45) * mm, "end": v(-3.42, 56.44) * mm});
            skLineSegment(sketch, "E1129", {"start": v(-3.42, 56.44) * mm, "end": v(-3.56, 56.42) * mm});
            skLineSegment(sketch, "E1130", {"start": v(-3.56, 56.42) * mm, "end": v(-3.7, 56.4) * mm});
            skLineSegment(sketch, "E1131", {"start": v(-3.7, 56.4) * mm, "end": v(-3.84, 56.37) * mm});
            skLineSegment(sketch, "E1132", {"start": v(-3.84, 56.37) * mm, "end": v(-3.97, 56.34) * mm});
            skLineSegment(sketch, "E1133", {"start": v(-3.97, 56.34) * mm, "end": v(-4.1, 56.3) * mm});
            skLineSegment(sketch, "E1134", {"start": v(-4.1, 56.3) * mm, "end": v(-4.23, 56.26) * mm});
            skLineSegment(sketch, "E1135", {"start": v(-4.23, 56.26) * mm, "end": v(-4.35, 56.21) * mm});
            skLineSegment(sketch, "E1136", {"start": v(-4.35, 56.21) * mm, "end": v(-4.42, 56.18) * mm});
            skLineSegment(sketch, "E1137", {"start": v(-4.42, 56.18) * mm, "end": v(-4.43, 56.18) * mm});
            skLineSegment(sketch, "E1138", {"start": v(-4.43, 56.18) * mm, "end": v(-4.45, 56.17) * mm});
            skLineSegment(sketch, "E1139", {"start": v(-4.45, 56.17) * mm, "end": v(-4.45, 56.17) * mm});
            skLineSegment(sketch, "E1140", {"start": v(-4.45, 56.17) * mm, "end": v(-4.52, 56.14) * mm});
            skLineSegment(sketch, "E1141", {"start": v(-4.52, 56.14) * mm, "end": v(-4.62, 56.1) * mm});
            skLineSegment(sketch, "E1142", {"start": v(-4.62, 56.1) * mm, "end": v(-4.73, 56.03) * mm});
            skLineSegment(sketch, "E1143", {"start": v(-4.73, 56.03) * mm, "end": v(-4.79, 56) * mm});
            skLineSegment(sketch, "E1144", {"start": v(-4.79, 56) * mm, "end": v(-4.8, 55.99) * mm});
            skLineSegment(sketch, "E1145", {"start": v(-4.8, 55.99) * mm, "end": v(-4.84, 55.97) * mm});
            skLineSegment(sketch, "E1146", {"start": v(-4.84, 55.97) * mm, "end": v(-4.9, 55.93) * mm});
            skLineSegment(sketch, "E1147", {"start": v(-4.9, 55.93) * mm, "end": v(-5, 55.86) * mm});
            skLineSegment(sketch, "E1148", {"start": v(-5, 55.86) * mm, "end": v(-5.12, 55.79) * mm});
            skLineSegment(sketch, "E1149", {"start": v(-5.12, 55.79) * mm, "end": v(-5.22, 55.71) * mm});
            skLineSegment(sketch, "E1150", {"start": v(-5.22, 55.71) * mm, "end": v(-5.3, 55.66) * mm});
            skLineSegment(sketch, "E1151", {"start": v(-5.3, 55.66) * mm, "end": v(-5.32, 55.64) * mm});
            skLineSegment(sketch, "E1152", {"start": v(-5.32, 55.64) * mm, "end": v(-5.37, 55.6) * mm});
            skLineSegment(sketch, "E1153", {"start": v(-5.37, 55.6) * mm, "end": v(-5.4, 55.57) * mm});
            skLineSegment(sketch, "E1154", {"start": v(-5.4, 55.57) * mm, "end": v(-4.95, 55.12) * mm});
            skLineSegment(sketch, "E1155", {"start": v(-4.95, 55.12) * mm, "end": v(-4.9, 55.14) * mm});
            skLineSegment(sketch, "E1156", {"start": v(-4.9, 55.14) * mm, "end": v(-4.81, 55.17) * mm});
            skLineSegment(sketch, "E1157", {"start": v(-4.81, 55.17) * mm, "end": v(-4.74, 55.2) * mm});
            skLineSegment(sketch, "E1158", {"start": v(-4.74, 55.2) * mm, "end": v(-4.67, 55.2) * mm});
            skLineSegment(sketch, "E1159", {"start": v(-4.67, 55.2) * mm, "end": v(-4.6, 55.22) * mm});
            skLineSegment(sketch, "E1160", {"start": v(-4.6, 55.22) * mm, "end": v(-4.52, 55.22) * mm});
            skLineSegment(sketch, "E1161", {"start": v(-4.52, 55.22) * mm, "end": v(-4.45, 55.22) * mm});
            skLineSegment(sketch, "E1162", {"start": v(-4.45, 55.22) * mm, "end": v(-4.39, 55.2) * mm});
            skLineSegment(sketch, "E1163", {"start": v(-4.39, 55.2) * mm, "end": v(-4.32, 55.19) * mm});
            skLineSegment(sketch, "E1164", {"start": v(-4.32, 55.19) * mm, "end": v(-4.25, 55.16) * mm});
            skLineSegment(sketch, "E1165", {"start": v(-4.25, 55.16) * mm, "end": v(-4.2, 55.12) * mm});
            skLineSegment(sketch, "E1166", {"start": v(-4.2, 55.12) * mm, "end": v(-4.13, 55.08) * mm});
            skLineSegment(sketch, "E1167", {"start": v(-4.13, 55.08) * mm, "end": v(-4.07, 55.03) * mm});
            skLineSegment(sketch, "E1168", {"start": v(-4.07, 55.03) * mm, "end": v(-4.02, 54.99) * mm});
            skLineSegment(sketch, "E1169", {"start": v(-4.02, 54.99) * mm, "end": v(0.17, 50.8) * mm});
            skLineSegment(sketch, "E1170", {"start": v(0.17, 50.8) * mm, "end": v(0.23, 50.73) * mm});
            skLineSegment(sketch, "E1171", {"start": v(0.23, 50.73) * mm, "end": v(0.23, 50.72) * mm});
            skLineSegment(sketch, "E1172", {"start": v(0.23, 50.72) * mm, "end": v(0.26, 50.68) * mm});
            skLineSegment(sketch, "E1173", {"start": v(0.26, 50.68) * mm, "end": v(0.3, 50.6) * mm});
            skLineSegment(sketch, "E1174", {"start": v(0.3, 50.6) * mm, "end": v(0.34, 50.52) * mm});
            skLineSegment(sketch, "E1175", {"start": v(0.34, 50.52) * mm, "end": v(0.36, 50.43) * mm});
            skLineSegment(sketch, "E1176", {"start": v(0.36, 50.43) * mm, "end": v(0.37, 50.35) * mm});
            skLineSegment(sketch, "E1177", {"start": v(0.37, 50.35) * mm, "end": v(0.37, 50.26) * mm});
            skLineSegment(sketch, "E1178", {"start": v(0.37, 50.26) * mm, "end": v(0.35, 50.17) * mm});
            skLineSegment(sketch, "E1179", {"start": v(0.35, 50.17) * mm, "end": v(0.33, 50.08) * mm});
            skLineSegment(sketch, "E1180", {"start": v(0.33, 50.08) * mm, "end": v(0.3, 49.98) * mm});
            skLineSegment(sketch, "E1181", {"start": v(0.3, 49.98) * mm, "end": v(0.27, 49.9) * mm});
            skLineSegment(sketch, "E1182", {"start": v(-5.3, 53.97) * mm, "end": v(-5.3, 53.97) * mm});
            skLineSegment(sketch, "E1183", {"start": v(-5.3, 53.97) * mm, "end": v(-5.3, 53.96) * mm});
            skLineSegment(sketch, "E1184", {"start": v(-5.3, 53.96) * mm, "end": v(-5.3, 53.97) * mm});
            skLineSegment(sketch, "E1185", {"start": v(10.41, 51.16) * mm, "end": v(10.42, 51.15) * mm});
            skLineSegment(sketch, "E1186", {"start": v(10.42, 51.15) * mm, "end": v(10.43, 51.16) * mm});
            skLineSegment(sketch, "E1187", {"start": v(10.43, 51.16) * mm, "end": v(10.44, 51.17) * mm});
            skLineSegment(sketch, "E1188", {"start": v(10.44, 51.17) * mm, "end": v(10.5, 51.24) * mm});
            skLineSegment(sketch, "E1189", {"start": v(10.5, 51.24) * mm, "end": v(10.58, 51.36) * mm});
            skLineSegment(sketch, "E1190", {"start": v(10.58, 51.36) * mm, "end": v(10.6, 51.4) * mm});
            skLineSegment(sketch, "E1191", {"start": v(10.6, 51.4) * mm, "end": v(10.6, 51.4) * mm});
            skLineSegment(sketch, "E1192", {"start": v(10.6, 51.4) * mm, "end": v(10.6, 51.41) * mm});
            skLineSegment(sketch, "E1193", {"start": v(10.6, 51.41) * mm, "end": v(10.6, 51.41) * mm});
            skLineSegment(sketch, "E1194", {"start": v(10.6, 51.41) * mm, "end": v(10.6, 51.4) * mm});
            skLineSegment(sketch, "E1195", {"start": v(10.6, 51.4) * mm, "end": v(10.64, 51.46) * mm});
            skLineSegment(sketch, "E1196", {"start": v(10.64, 51.46) * mm, "end": v(10.7, 51.55) * mm});
            skLineSegment(sketch, "E1197", {"start": v(10.7, 51.55) * mm, "end": v(10.74, 51.65) * mm});
            skLineSegment(sketch, "E1198", {"start": v(10.74, 51.65) * mm, "end": v(10.78, 51.74) * mm});
            skLineSegment(sketch, "E1199", {"start": v(10.78, 51.74) * mm, "end": v(10.82, 51.84) * mm});
            skLineSegment(sketch, "E1200", {"start": v(10.82, 51.84) * mm, "end": v(10.85, 51.94) * mm});
            skLineSegment(sketch, "E1201", {"start": v(10.85, 51.94) * mm, "end": v(10.87, 52.04) * mm});
            skLineSegment(sketch, "E1202", {"start": v(10.87, 52.04) * mm, "end": v(10.9, 52.15) * mm});
            skLineSegment(sketch, "E1203", {"start": v(10.9, 52.15) * mm, "end": v(10.91, 52.26) * mm});
            skLineSegment(sketch, "E1204", {"start": v(10.91, 52.26) * mm, "end": v(10.92, 52.32) * mm});
            skLineSegment(sketch, "E1205", {"start": v(10.92, 52.32) * mm, "end": v(10.92, 52.59) * mm});
            skLineSegment(sketch, "E1206", {"start": v(10.92, 52.59) * mm, "end": v(10.9, 52.67) * mm});
            skLineSegment(sketch, "E1207", {"start": v(10.9, 52.67) * mm, "end": v(10.89, 52.8) * mm});
            skLineSegment(sketch, "E1208", {"start": v(10.89, 52.8) * mm, "end": v(10.86, 52.94) * mm});
            skLineSegment(sketch, "E1209", {"start": v(10.86, 52.94) * mm, "end": v(10.82, 53.07) * mm});
            skLineSegment(sketch, "E1210", {"start": v(10.82, 53.07) * mm, "end": v(10.77, 53.2) * mm});
            skLineSegment(sketch, "E1211", {"start": v(10.77, 53.2) * mm, "end": v(10.72, 53.33) * mm});
            skLineSegment(sketch, "E1212", {"start": v(10.72, 53.33) * mm, "end": v(10.66, 53.46) * mm});
            skLineSegment(sketch, "E1213", {"start": v(10.66, 53.46) * mm, "end": v(10.58, 53.6) * mm});
            skLineSegment(sketch, "E1214", {"start": v(10.58, 53.6) * mm, "end": v(10.5, 53.72) * mm});
            skLineSegment(sketch, "E1215", {"start": v(10.5, 53.72) * mm, "end": v(10.41, 53.86) * mm});
            skLineSegment(sketch, "E1216", {"start": v(10.41, 53.86) * mm, "end": v(10.32, 53.97) * mm});
            skLineSegment(sketch, "E1217", {"start": v(10.32, 53.97) * mm, "end": v(10.3, 54) * mm});
            skLineSegment(sketch, "E1218", {"start": v(10.3, 54) * mm, "end": v(10.17, 54.14) * mm});
            skLineSegment(sketch, "E1219", {"start": v(10.17, 54.14) * mm, "end": v(9.98, 54.34) * mm});
            skLineSegment(sketch, "E1220", {"start": v(9.98, 54.34) * mm, "end": v(9.93, 54.38) * mm});
            skLineSegment(sketch, "E1221", {"start": v(9.93, 54.38) * mm, "end": v(9.85, 54.45) * mm});
            skLineSegment(sketch, "E1222", {"start": v(9.85, 54.45) * mm, "end": v(9.8, 54.5) * mm});
            skLineSegment(sketch, "E1223", {"start": v(9.8, 54.5) * mm, "end": v(9.71, 54.56) * mm});
            skLineSegment(sketch, "E1224", {"start": v(9.71, 54.56) * mm, "end": v(9.6, 54.64) * mm});
            skLineSegment(sketch, "E1225", {"start": v(9.6, 54.64) * mm, "end": v(9.54, 54.69) * mm});
            skLineSegment(sketch, "E1226", {"start": v(9.54, 54.69) * mm, "end": v(9.53, 54.69) * mm});
            skLineSegment(sketch, "E1227", {"start": v(9.53, 54.69) * mm, "end": v(9.53, 54.69) * mm});
            skLineSegment(sketch, "E1228", {"start": v(9.53, 54.69) * mm, "end": v(9.54, 54.71) * mm});
            skLineSegment(sketch, "E1229", {"start": v(9.54, 54.71) * mm, "end": v(9.56, 54.74) * mm});
            skLineSegment(sketch, "E1230", {"start": v(9.56, 54.74) * mm, "end": v(9.57, 54.77) * mm});
            skLineSegment(sketch, "E1231", {"start": v(9.57, 54.77) * mm, "end": v(9.57, 54.8) * mm});
            skLineSegment(sketch, "E1232", {"start": v(9.57, 54.8) * mm, "end": v(9.57, 54.83) * mm});
            skLineSegment(sketch, "E1233", {"start": v(9.57, 54.83) * mm, "end": v(9.56, 54.87) * mm});
            skLineSegment(sketch, "E1234", {"start": v(9.56, 54.87) * mm, "end": v(9.55, 54.9) * mm});
            skLineSegment(sketch, "E1235", {"start": v(9.55, 54.9) * mm, "end": v(9.53, 54.94) * mm});
            skLineSegment(sketch, "E1236", {"start": v(9.53, 54.94) * mm, "end": v(9.5, 54.98) * mm});
            skLineSegment(sketch, "E1237", {"start": v(9.5, 54.98) * mm, "end": v(9.46, 55.05) * mm});
            skLineSegment(sketch, "E1238", {"start": v(9.46, 55.05) * mm, "end": v(9.44, 55.07) * mm});
            skLineSegment(sketch, "E1239", {"start": v(9.44, 55.07) * mm, "end": v(9.43, 55.09) * mm});
            skLineSegment(sketch, "E1240", {"start": v(9.43, 55.09) * mm, "end": v(9.42, 55.1) * mm});
            skLineSegment(sketch, "E1241", {"start": v(9.42, 55.1) * mm, "end": v(9.42, 55.1) * mm});
            skLineSegment(sketch, "E1242", {"start": v(9.42, 55.1) * mm, "end": v(9.42, 55.11) * mm});
            skLineSegment(sketch, "E1243", {"start": v(9.42, 55.11) * mm, "end": v(9.38, 55.17) * mm});
            skLineSegment(sketch, "E1244", {"start": v(9.38, 55.17) * mm, "end": v(9.31, 55.27) * mm});
            skLineSegment(sketch, "E1245", {"start": v(9.31, 55.27) * mm, "end": v(9.26, 55.35) * mm});
            skLineSegment(sketch, "E1246", {"start": v(9.26, 55.35) * mm, "end": v(9.23, 55.41) * mm});
            skLineSegment(sketch, "E1247", {"start": v(9.23, 55.41) * mm, "end": v(9.23, 55.4) * mm});
            skLineSegment(sketch, "E1248", {"start": v(9.23, 55.4) * mm, "end": v(9.23, 55.41) * mm});
            skLineSegment(sketch, "E1249", {"start": v(9.23, 55.41) * mm, "end": v(9.22, 55.44) * mm});
            skLineSegment(sketch, "E1250", {"start": v(9.22, 55.44) * mm, "end": v(9.21, 55.45) * mm});
            skLineSegment(sketch, "E1251", {"start": v(9.21, 55.45) * mm, "end": v(9.18, 55.52) * mm});
            skLineSegment(sketch, "E1252", {"start": v(9.18, 55.52) * mm, "end": v(9.14, 55.64) * mm});
            skLineSegment(sketch, "E1253", {"start": v(9.14, 55.64) * mm, "end": v(9.1, 55.76) * mm});
            skLineSegment(sketch, "E1254", {"start": v(9.1, 55.76) * mm, "end": v(9.1, 55.82) * mm});
            skLineSegment(sketch, "E1255", {"start": v(9.1, 55.82) * mm, "end": v(9.1, 55.88) * mm});
            skLineSegment(sketch, "E1256", {"start": v(9.1, 55.88) * mm, "end": v(9.1, 55.94) * mm});
            skLineSegment(sketch, "E1257", {"start": v(9.1, 55.94) * mm, "end": v(9.1, 56) * mm});
            skLineSegment(sketch, "E1258", {"start": v(9.1, 56) * mm, "end": v(9.1, 56.06) * mm});
            skLineSegment(sketch, "E1259", {"start": v(9.1, 56.06) * mm, "end": v(9.1, 56.08) * mm});
            skLineSegment(sketch, "E1260", {"start": v(9.1, 56.08) * mm, "end": v(8.85, 56.33) * mm});
            skLineSegment(sketch, "E1261", {"start": v(8.85, 56.33) * mm, "end": v(8.21, 55.7) * mm});
            skLineSegment(sketch, "E1262", {"start": v(8.21, 55.7) * mm, "end": v(8.91, 55) * mm});
            skLineSegment(sketch, "E1263", {"start": v(8.91, 55) * mm, "end": v(8.9, 55) * mm});
            skLineSegment(sketch, "E1264", {"start": v(8.9, 55) * mm, "end": v(8.86, 55) * mm});
            skLineSegment(sketch, "E1265", {"start": v(8.86, 55) * mm, "end": v(8.78, 55.03) * mm});
            skLineSegment(sketch, "E1266", {"start": v(8.78, 55.03) * mm, "end": v(8.7, 55.05) * mm});
            skLineSegment(sketch, "E1267", {"start": v(8.7, 55.05) * mm, "end": v(8.6, 55.06) * mm});
            skLineSegment(sketch, "E1268", {"start": v(8.6, 55.06) * mm, "end": v(8.51, 55.08) * mm});
            skLineSegment(sketch, "E1269", {"start": v(8.51, 55.08) * mm, "end": v(8.45, 55.09) * mm});
            skLineSegment(sketch, "E1270", {"start": v(8.45, 55.09) * mm, "end": v(8.33, 55.09) * mm});
            skLineSegment(sketch, "E1271", {"start": v(8.33, 55.09) * mm, "end": v(8.24, 55.1) * mm});
            skLineSegment(sketch, "E1272", {"start": v(8.24, 55.1) * mm, "end": v(8.14, 55.09) * mm});
            skLineSegment(sketch, "E1273", {"start": v(8.14, 55.09) * mm, "end": v(8.05, 55.08) * mm});
            skLineSegment(sketch, "E1274", {"start": v(8.05, 55.08) * mm, "end": v(7.96, 55.06) * mm});
            skLineSegment(sketch, "E1275", {"start": v(7.96, 55.06) * mm, "end": v(7.87, 55.05) * mm});
            skLineSegment(sketch, "E1276", {"start": v(7.87, 55.05) * mm, "end": v(7.78, 55.02) * mm});
            skLineSegment(sketch, "E1277", {"start": v(7.78, 55.02) * mm, "end": v(7.7, 55) * mm});
            skLineSegment(sketch, "E1278", {"start": v(7.7, 55) * mm, "end": v(7.6, 54.97) * mm});
            skLineSegment(sketch, "E1279", {"start": v(7.6, 54.97) * mm, "end": v(7.54, 54.94) * mm});
            skLineSegment(sketch, "E1280", {"start": v(7.54, 54.94) * mm, "end": v(7.53, 54.93) * mm});
            skLineSegment(sketch, "E1281", {"start": v(7.53, 54.93) * mm, "end": v(7.52, 54.93) * mm});
            skLineSegment(sketch, "E1282", {"start": v(7.52, 54.93) * mm, "end": v(7.52, 54.93) * mm});
            skLineSegment(sketch, "E1283", {"start": v(7.52, 54.93) * mm, "end": v(7.46, 54.9) * mm});
            skLineSegment(sketch, "E1284", {"start": v(7.46, 54.9) * mm, "end": v(7.34, 54.84) * mm});
            skLineSegment(sketch, "E1285", {"start": v(7.34, 54.84) * mm, "end": v(7.21, 54.76) * mm});
            skLineSegment(sketch, "E1286", {"start": v(7.21, 54.76) * mm, "end": v(7.16, 54.73) * mm});
            skLineSegment(sketch, "E1287", {"start": v(7.16, 54.73) * mm, "end": v(6.99, 54.6) * mm});
            skLineSegment(sketch, "E1288", {"start": v(6.99, 54.6) * mm, "end": v(6.98, 54.6) * mm});
            skLineSegment(sketch, "E1289", {"start": v(6.98, 54.6) * mm, "end": v(7.23, 54.34) * mm});
            skLineSegment(sketch, "E1290", {"start": v(7.23, 54.34) * mm, "end": v(7.26, 54.35) * mm});
            skLineSegment(sketch, "E1291", {"start": v(7.26, 54.35) * mm, "end": v(7.3, 54.37) * mm});
            skLineSegment(sketch, "E1292", {"start": v(7.3, 54.37) * mm, "end": v(7.35, 54.38) * mm});
            skLineSegment(sketch, "E1293", {"start": v(7.35, 54.38) * mm, "end": v(7.4, 54.39) * mm});
            skLineSegment(sketch, "E1294", {"start": v(7.4, 54.39) * mm, "end": v(7.44, 54.4) * mm});
            skLineSegment(sketch, "E1295", {"start": v(7.44, 54.4) * mm, "end": v(7.5, 54.4) * mm});
            skLineSegment(sketch, "E1296", {"start": v(7.5, 54.4) * mm, "end": v(7.57, 54.38) * mm});
            skLineSegment(sketch, "E1297", {"start": v(7.57, 54.38) * mm, "end": v(7.62, 54.36) * mm});
            skLineSegment(sketch, "E1298", {"start": v(7.62, 54.36) * mm, "end": v(7.68, 54.33) * mm});
            skLineSegment(sketch, "E1299", {"start": v(7.68, 54.33) * mm, "end": v(7.72, 54.3) * mm});
            skLineSegment(sketch, "E1300", {"start": v(7.72, 54.3) * mm, "end": v(10.1, 51.92) * mm});
            skLineSegment(sketch, "E1301", {"start": v(10.1, 51.92) * mm, "end": v(10.13, 51.88) * mm});
            skLineSegment(sketch, "E1302", {"start": v(10.13, 51.88) * mm, "end": v(10.16, 51.84) * mm});
            skLineSegment(sketch, "E1303", {"start": v(10.16, 51.84) * mm, "end": v(10.18, 51.8) * mm});
            skLineSegment(sketch, "E1304", {"start": v(10.18, 51.8) * mm, "end": v(10.2, 51.76) * mm});
            skLineSegment(sketch, "E1305", {"start": v(10.2, 51.76) * mm, "end": v(10.22, 51.72) * mm});
            skLineSegment(sketch, "E1306", {"start": v(10.22, 51.72) * mm, "end": v(10.22, 51.66) * mm});
            skLineSegment(sketch, "E1307", {"start": v(10.22, 51.66) * mm, "end": v(10.22, 51.59) * mm});
            skLineSegment(sketch, "E1308", {"start": v(10.22, 51.59) * mm, "end": v(10.2, 51.52) * mm});
            skLineSegment(sketch, "E1309", {"start": v(10.2, 51.52) * mm, "end": v(10.18, 51.44) * mm});
            skLineSegment(sketch, "E1310", {"start": v(10.18, 51.44) * mm, "end": v(10.17, 51.4) * mm});
            skLineSegment(sketch, "E1311", {"start": v(10.17, 51.4) * mm, "end": v(10.4, 51.17) * mm});
            skLineSegment(sketch, "E1312", {"start": v(10.4, 51.17) * mm, "end": v(10.4, 51.18) * mm});
            skLineSegment(sketch, "E1313", {"start": v(10.4, 51.18) * mm, "end": v(10.4, 51.18) * mm});
            skLineSegment(sketch, "E1314", {"start": v(10.4, 51.18) * mm, "end": v(10.4, 51.17) * mm});
            skLineSegment(sketch, "E1315", {"start": v(10.4, 51.17) * mm, "end": v(10.4, 51.17) * mm});
            skLineSegment(sketch, "E1316", {"start": v(10.4, 51.17) * mm, "end": v(10.41, 51.16) * mm});
            skLineSegment(sketch, "E1317", {"start": v(-8.35, 41.51) * mm, "end": v(-8.32, 41.6) * mm});
            skLineSegment(sketch, "E1318", {"start": v(-8.32, 41.6) * mm, "end": v(-8.26, 41.72) * mm});
            skLineSegment(sketch, "E1319", {"start": v(-8.26, 41.72) * mm, "end": v(-8.25, 41.78) * mm});
            skLineSegment(sketch, "E1320", {"start": v(-8.25, 41.78) * mm, "end": v(-8.24, 41.82) * mm});
            skLineSegment(sketch, "E1321", {"start": v(-8.24, 41.82) * mm, "end": v(-8.24, 41.87) * mm});
            skLineSegment(sketch, "E1322", {"start": v(-8.24, 41.87) * mm, "end": v(-8.25, 41.91) * mm});
            skLineSegment(sketch, "E1323", {"start": v(-8.25, 41.91) * mm, "end": v(-8.26, 41.94) * mm});
            skLineSegment(sketch, "E1324", {"start": v(-8.26, 41.94) * mm, "end": v(-8.28, 41.98) * mm});
            skLineSegment(sketch, "E1325", {"start": v(-8.28, 41.98) * mm, "end": v(-8.3, 42.01) * mm});
            skLineSegment(sketch, "E1326", {"start": v(-8.3, 42.01) * mm, "end": v(-8.34, 42.05) * mm});
            skLineSegment(sketch, "E1327", {"start": v(-8.34, 42.05) * mm, "end": v(-8.36, 42.08) * mm});
            skLineSegment(sketch, "E1328", {"start": v(-8.36, 42.08) * mm, "end": v(-12.76, 46.48) * mm});
            skLineSegment(sketch, "E1329", {"start": v(-12.76, 46.48) * mm, "end": v(-12.8, 46.51) * mm});
            skLineSegment(sketch, "E1330", {"start": v(-12.8, 46.51) * mm, "end": v(-12.85, 46.56) * mm});
            skLineSegment(sketch, "E1331", {"start": v(-12.85, 46.56) * mm, "end": v(-12.9, 46.59) * mm});
            skLineSegment(sketch, "E1332", {"start": v(-12.9, 46.59) * mm, "end": v(-12.95, 46.6) * mm});
            skLineSegment(sketch, "E1333", {"start": v(-12.95, 46.6) * mm, "end": v(-13, 46.62) * mm});
            skLineSegment(sketch, "E1334", {"start": v(-13, 46.62) * mm, "end": v(-13.05, 46.61) * mm});
            skLineSegment(sketch, "E1335", {"start": v(-13.05, 46.61) * mm, "end": v(-13.11, 46.6) * mm});
            skLineSegment(sketch, "E1336", {"start": v(-13.11, 46.6) * mm, "end": v(-13.18, 46.58) * mm});
            skLineSegment(sketch, "E1337", {"start": v(-13.18, 46.58) * mm, "end": v(-13.26, 46.54) * mm});
            skLineSegment(sketch, "E1338", {"start": v(-13.26, 46.54) * mm, "end": v(-13.34, 46.5) * mm});
            skLineSegment(sketch, "E1339", {"start": v(-13.34, 46.5) * mm, "end": v(-13.34, 41.51) * mm});
            skLineSegment(sketch, "E1340", {"start": v(-13.34, 41.51) * mm, "end": v(-8.35, 41.51) * mm});
            skLineSegment(sketch, "E1341", {"start": v(-7.06, 54.96) * mm, "end": v(-7.06, 54.96) * mm});
            skLineSegment(sketch, "E1342", {"start": v(-7.06, 54.96) * mm, "end": v(-7.07, 54.96) * mm});
            skLineSegment(sketch, "E1343", {"start": v(-7.07, 54.96) * mm, "end": v(-7.06, 54.95) * mm});
            skLineSegment(sketch, "E1344", {"start": v(-7.06, 54.95) * mm, "end": v(-7.06, 54.96) * mm});
            skLineSegment(sketch, "E1345", {"start": v(-7.02, 55) * mm, "end": v(-7.02, 55) * mm});
            skLineSegment(sketch, "E1346", {"start": v(4.6, 56.01) * mm, "end": v(4.59, 56.01) * mm});
            skLineSegment(sketch, "E1347", {"start": v(4.59, 56.01) * mm, "end": v(4.59, 56.01) * mm});
            skLineSegment(sketch, "E1348", {"start": v(4.59, 56.01) * mm, "end": v(4.59, 56) * mm});
            skLineSegment(sketch, "E1349", {"start": v(4.59, 56) * mm, "end": v(4.6, 56.01) * mm});
            skLineSegment(sketch, "E1350", {"start": v(-9.89, 56.3) * mm, "end": v(-9.86, 56.29) * mm});
            skLineSegment(sketch, "E1351", {"start": v(-9.86, 56.29) * mm, "end": v(-9.83, 56.29) * mm});
            skLineSegment(sketch, "E1352", {"start": v(-9.83, 56.29) * mm, "end": v(-9.8, 56.29) * mm});
            skLineSegment(sketch, "E1353", {"start": v(-9.8, 56.29) * mm, "end": v(-9.76, 56.3) * mm});
            skLineSegment(sketch, "E1354", {"start": v(-9.76, 56.3) * mm, "end": v(-9.73, 56.32) * mm});
            skLineSegment(sketch, "E1355", {"start": v(-9.73, 56.32) * mm, "end": v(-9.71, 56.33) * mm});
            skLineSegment(sketch, "E1356", {"start": v(-9.71, 56.33) * mm, "end": v(-9.7, 56.35) * mm});
            skLineSegment(sketch, "E1357", {"start": v(-9.7, 56.35) * mm, "end": v(-9.68, 56.37) * mm});
            skLineSegment(sketch, "E1358", {"start": v(-9.68, 56.37) * mm, "end": v(-9.66, 56.4) * mm});
            skLineSegment(sketch, "E1359", {"start": v(-9.66, 56.4) * mm, "end": v(-9.65, 56.42) * mm});
            skLineSegment(sketch, "E1360", {"start": v(-9.65, 56.42) * mm, "end": v(-9.65, 56.45) * mm});
            skLineSegment(sketch, "E1361", {"start": v(-9.65, 56.45) * mm, "end": v(-9.64, 56.49) * mm});
            skLineSegment(sketch, "E1362", {"start": v(-9.64, 56.49) * mm, "end": v(-9.65, 56.53) * mm});
            skLineSegment(sketch, "E1363", {"start": v(-9.65, 56.53) * mm, "end": v(-9.66, 56.56) * mm});
            skLineSegment(sketch, "E1364", {"start": v(-9.66, 56.56) * mm, "end": v(-9.68, 56.58) * mm});
            skLineSegment(sketch, "E1365", {"start": v(-9.68, 56.58) * mm, "end": v(-9.68, 56.59) * mm});
            skLineSegment(sketch, "E1366", {"start": v(-9.68, 56.59) * mm, "end": v(-9.7, 56.63) * mm});
            skLineSegment(sketch, "E1367", {"start": v(-9.7, 56.63) * mm, "end": v(-9.75, 56.7) * mm});
            skLineSegment(sketch, "E1368", {"start": v(-9.75, 56.7) * mm, "end": v(-9.78, 56.74) * mm});
            skLineSegment(sketch, "E1369", {"start": v(-9.78, 56.74) * mm, "end": v(-9.89, 56.9) * mm});
            skLineSegment(sketch, "E1370", {"start": v(-9.89, 56.9) * mm, "end": v(-9.9, 56.93) * mm});
            skLineSegment(sketch, "E1371", {"start": v(-9.9, 56.93) * mm, "end": v(-9.92, 56.95) * mm});
            skLineSegment(sketch, "E1372", {"start": v(-9.92, 56.95) * mm, "end": v(-9.93, 56.96) * mm});
            skLineSegment(sketch, "E1373", {"start": v(-9.93, 56.96) * mm, "end": v(-9.93, 56.96) * mm});
            skLineSegment(sketch, "E1374", {"start": v(-9.93, 56.96) * mm, "end": v(-9.93, 56.97) * mm});
            skLineSegment(sketch, "E1375", {"start": v(-9.93, 56.97) * mm, "end": v(-9.96, 57.03) * mm});
            skLineSegment(sketch, "E1376", {"start": v(-9.96, 57.03) * mm, "end": v(-10, 57.11) * mm});
            skLineSegment(sketch, "E1377", {"start": v(-10, 57.11) * mm, "end": v(-10.03, 57.2) * mm});
            skLineSegment(sketch, "E1378", {"start": v(-10.03, 57.2) * mm, "end": v(-10.06, 57.27) * mm});
            skLineSegment(sketch, "E1379", {"start": v(-10.06, 57.27) * mm, "end": v(-10.08, 57.36) * mm});
            skLineSegment(sketch, "E1380", {"start": v(-10.08, 57.36) * mm, "end": v(-10.1, 57.4) * mm});
            skLineSegment(sketch, "E1381", {"start": v(-10.1, 57.4) * mm, "end": v(-10.1, 57.66) * mm});
            skLineSegment(sketch, "E1382", {"start": v(-10.1, 57.66) * mm, "end": v(-10.32, 57.9) * mm});
            skLineSegment(sketch, "E1383", {"start": v(-10.32, 57.9) * mm, "end": v(-10.92, 57.3) * mm});
            skLineSegment(sketch, "E1384", {"start": v(-10.92, 57.3) * mm, "end": v(-9.95, 56.32) * mm});
            skLineSegment(sketch, "E1385", {"start": v(-9.95, 56.32) * mm, "end": v(-9.93, 56.31) * mm});
            skLineSegment(sketch, "E1386", {"start": v(-9.93, 56.31) * mm, "end": v(-9.89, 56.3) * mm});
            skLineSegment(sketch, "E1387", {"start": v(4.41, 56.36) * mm, "end": v(4.41, 56.36) * mm});
            skLineSegment(sketch, "E1388", {"start": v(4.41, 56.36) * mm, "end": v(4.4, 56.36) * mm});
            skLineSegment(sketch, "E1389", {"start": v(4.4, 56.36) * mm, "end": v(4.41, 56.36) * mm});
            skLineSegment(sketch, "E1390", {"start": v(2.85, 52.07) * mm, "end": v(2.92, 52.06) * mm});
            skLineSegment(sketch, "E1391", {"start": v(2.92, 52.06) * mm, "end": v(2.95, 52.06) * mm});
            skLineSegment(sketch, "E1392", {"start": v(2.95, 52.06) * mm, "end": v(2.98, 52.06) * mm});
            skLineSegment(sketch, "E1393", {"start": v(2.98, 52.06) * mm, "end": v(3.05, 52.09) * mm});
            skLineSegment(sketch, "E1394", {"start": v(3.05, 52.09) * mm, "end": v(3.12, 52.13) * mm});
            skLineSegment(sketch, "E1395", {"start": v(3.12, 52.13) * mm, "end": v(3.2, 52.18) * mm});
            skLineSegment(sketch, "E1396", {"start": v(3.2, 52.18) * mm, "end": v(3.24, 52.2) * mm});
            skLineSegment(sketch, "E1397", {"start": v(3.24, 52.2) * mm, "end": v(4.37, 53.34) * mm});
            skLineSegment(sketch, "E1398", {"start": v(4.37, 53.34) * mm, "end": v(4.4, 53.38) * mm});
            skLineSegment(sketch, "E1399", {"start": v(4.4, 53.38) * mm, "end": v(4.46, 53.47) * mm});
            skLineSegment(sketch, "E1400", {"start": v(4.46, 53.47) * mm, "end": v(4.48, 53.51) * mm});
            skLineSegment(sketch, "E1401", {"start": v(4.48, 53.51) * mm, "end": v(4.5, 53.55) * mm});
            skLineSegment(sketch, "E1402", {"start": v(4.5, 53.55) * mm, "end": v(4.51, 53.6) * mm});
            skLineSegment(sketch, "E1403", {"start": v(4.51, 53.6) * mm, "end": v(4.52, 53.63) * mm});
            skLineSegment(sketch, "E1404", {"start": v(4.52, 53.63) * mm, "end": v(4.52, 53.67) * mm});
            skLineSegment(sketch, "E1405", {"start": v(4.52, 53.67) * mm, "end": v(4.52, 53.7) * mm});
            skLineSegment(sketch, "E1406", {"start": v(4.52, 53.7) * mm, "end": v(4.5, 53.74) * mm});
            skLineSegment(sketch, "E1407", {"start": v(4.5, 53.74) * mm, "end": v(4.49, 53.77) * mm});
            skLineSegment(sketch, "E1408", {"start": v(4.49, 53.77) * mm, "end": v(4.47, 53.8) * mm});
            skLineSegment(sketch, "E1409", {"start": v(4.47, 53.8) * mm, "end": v(4.44, 53.84) * mm});
            skLineSegment(sketch, "E1410", {"start": v(4.44, 53.84) * mm, "end": v(4.41, 53.87) * mm});
            skLineSegment(sketch, "E1411", {"start": v(4.41, 53.87) * mm, "end": v(4.38, 53.9) * mm});
            skLineSegment(sketch, "E1412", {"start": v(4.38, 53.9) * mm, "end": v(4.35, 53.92) * mm});
            skLineSegment(sketch, "E1413", {"start": v(4.35, 53.92) * mm, "end": v(4.31, 53.93) * mm});
            skLineSegment(sketch, "E1414", {"start": v(4.31, 53.93) * mm, "end": v(4.28, 53.94) * mm});
            skLineSegment(sketch, "E1415", {"start": v(4.28, 53.94) * mm, "end": v(4.25, 53.94) * mm});
            skLineSegment(sketch, "E1416", {"start": v(4.25, 53.94) * mm, "end": v(4.22, 53.94) * mm});
            skLineSegment(sketch, "E1417", {"start": v(4.22, 53.94) * mm, "end": v(4.18, 53.93) * mm});
            skLineSegment(sketch, "E1418", {"start": v(4.18, 53.93) * mm, "end": v(4.13, 53.92) * mm});
            skLineSegment(sketch, "E1419", {"start": v(4.13, 53.92) * mm, "end": v(4.05, 53.9) * mm});
            skLineSegment(sketch, "E1420", {"start": v(4.05, 53.9) * mm, "end": v(3.9, 53.85) * mm});
            skLineSegment(sketch, "E1421", {"start": v(3.9, 53.85) * mm, "end": v(3.84, 53.84) * mm});
            skLineSegment(sketch, "E1422", {"start": v(3.84, 53.84) * mm, "end": v(3.78, 53.83) * mm});
            skLineSegment(sketch, "E1423", {"start": v(3.78, 53.83) * mm, "end": v(3.72, 53.83) * mm});
            skLineSegment(sketch, "E1424", {"start": v(3.72, 53.83) * mm, "end": v(3.66, 53.83) * mm});
            skLineSegment(sketch, "E1425", {"start": v(3.66, 53.83) * mm, "end": v(3.6, 53.84) * mm});
            skLineSegment(sketch, "E1426", {"start": v(3.6, 53.84) * mm, "end": v(3.54, 53.85) * mm});
            skLineSegment(sketch, "E1427", {"start": v(3.54, 53.85) * mm, "end": v(3.46, 53.87) * mm});
            skLineSegment(sketch, "E1428", {"start": v(3.46, 53.87) * mm, "end": v(3.38, 53.9) * mm});
            skLineSegment(sketch, "E1429", {"start": v(3.38, 53.9) * mm, "end": v(3.3, 53.93) * mm});
            skLineSegment(sketch, "E1430", {"start": v(3.3, 53.93) * mm, "end": v(3.2, 53.97) * mm});
            skLineSegment(sketch, "E1431", {"start": v(3.2, 53.97) * mm, "end": v(3.12, 54.02) * mm});
            skLineSegment(sketch, "E1432", {"start": v(3.12, 54.02) * mm, "end": v(3.03, 54.07) * mm});
            skLineSegment(sketch, "E1433", {"start": v(3.03, 54.07) * mm, "end": v(2.94, 54.13) * mm});
            skLineSegment(sketch, "E1434", {"start": v(2.94, 54.13) * mm, "end": v(2.85, 54.2) * mm});
            skLineSegment(sketch, "E1435", {"start": v(2.85, 54.2) * mm, "end": v(2.8, 54.23) * mm});
            skLineSegment(sketch, "E1436", {"start": v(2.8, 54.23) * mm, "end": v(1.43, 55.6) * mm});
            skLineSegment(sketch, "E1437", {"start": v(1.43, 55.6) * mm, "end": v(0.84, 55.89) * mm});
            skLineSegment(sketch, "E1438", {"start": v(0.84, 55.89) * mm, "end": v(0.44, 56.08) * mm});
            skLineSegment(sketch, "E1439", {"start": v(0.44, 56.08) * mm, "end": v(-0.08, 56.35) * mm});
            skLineSegment(sketch, "E1440", {"start": v(-0.08, 56.35) * mm, "end": v(-0.3, 56.46) * mm});
            skLineSegment(sketch, "E1441", {"start": v(-0.3, 56.46) * mm, "end": v(-0.31, 56.44) * mm});
            skLineSegment(sketch, "E1442", {"start": v(-0.31, 56.44) * mm, "end": v(2.34, 53.78) * mm});
            skLineSegment(sketch, "E1443", {"start": v(2.34, 53.78) * mm, "end": v(2.38, 53.73) * mm});
            skLineSegment(sketch, "E1444", {"start": v(2.38, 53.73) * mm, "end": v(2.46, 53.62) * mm});
            skLineSegment(sketch, "E1445", {"start": v(2.46, 53.62) * mm, "end": v(2.5, 53.56) * mm});
            skLineSegment(sketch, "E1446", {"start": v(2.5, 53.56) * mm, "end": v(2.5, 53.56) * mm});
            skLineSegment(sketch, "E1447", {"start": v(2.5, 53.56) * mm, "end": v(2.51, 53.53) * mm});
            skLineSegment(sketch, "E1448", {"start": v(2.51, 53.53) * mm, "end": v(2.53, 53.51) * mm});
            skLineSegment(sketch, "E1449", {"start": v(2.53, 53.51) * mm, "end": v(2.57, 53.44) * mm});
            skLineSegment(sketch, "E1450", {"start": v(2.57, 53.44) * mm, "end": v(2.64, 53.3) * mm});
            skLineSegment(sketch, "E1451", {"start": v(2.64, 53.3) * mm, "end": v(2.67, 53.23) * mm});
            skLineSegment(sketch, "E1452", {"start": v(2.67, 53.23) * mm, "end": v(2.7, 53.16) * mm});
            skLineSegment(sketch, "E1453", {"start": v(2.7, 53.16) * mm, "end": v(2.71, 53.1) * mm});
            skLineSegment(sketch, "E1454", {"start": v(2.71, 53.1) * mm, "end": v(2.73, 53.03) * mm});
            skLineSegment(sketch, "E1455", {"start": v(2.73, 53.03) * mm, "end": v(2.74, 52.97) * mm});
            skLineSegment(sketch, "E1456", {"start": v(2.74, 52.97) * mm, "end": v(2.75, 52.9) * mm});
            skLineSegment(sketch, "E1457", {"start": v(2.75, 52.9) * mm, "end": v(2.75, 52.82) * mm});
            skLineSegment(sketch, "E1458", {"start": v(2.75, 52.82) * mm, "end": v(2.74, 52.73) * mm});
            skLineSegment(sketch, "E1459", {"start": v(2.74, 52.73) * mm, "end": v(2.71, 52.63) * mm});
            skLineSegment(sketch, "E1460", {"start": v(2.71, 52.63) * mm, "end": v(2.68, 52.52) * mm});
            skLineSegment(sketch, "E1461", {"start": v(2.68, 52.52) * mm, "end": v(2.65, 52.42) * mm});
            skLineSegment(sketch, "E1462", {"start": v(2.65, 52.42) * mm, "end": v(2.64, 52.4) * mm});
            skLineSegment(sketch, "E1463", {"start": v(2.64, 52.4) * mm, "end": v(2.64, 52.35) * mm});
            skLineSegment(sketch, "E1464", {"start": v(2.64, 52.35) * mm, "end": v(2.64, 52.31) * mm});
            skLineSegment(sketch, "E1465", {"start": v(2.64, 52.31) * mm, "end": v(2.64, 52.27) * mm});
            skLineSegment(sketch, "E1466", {"start": v(2.64, 52.27) * mm, "end": v(2.66, 52.23) * mm});
            skLineSegment(sketch, "E1467", {"start": v(2.66, 52.23) * mm, "end": v(2.69, 52.19) * mm});
            skLineSegment(sketch, "E1468", {"start": v(2.69, 52.19) * mm, "end": v(2.72, 52.15) * mm});
            skLineSegment(sketch, "E1469", {"start": v(2.72, 52.15) * mm, "end": v(2.76, 52.12) * mm});
            skLineSegment(sketch, "E1470", {"start": v(2.76, 52.12) * mm, "end": v(2.79, 52.1) * mm});
            skLineSegment(sketch, "E1471", {"start": v(2.79, 52.1) * mm, "end": v(2.82, 52.08) * mm});
            skLineSegment(sketch, "E1472", {"start": v(2.82, 52.08) * mm, "end": v(2.85, 52.07) * mm});
            skLineSegment(sketch, "E1473", {"start": v(11.78, 57.1) * mm, "end": v(11.82, 57.09) * mm});
            skLineSegment(sketch, "E1474", {"start": v(11.82, 57.09) * mm, "end": v(11.86, 57.09) * mm});
            skLineSegment(sketch, "E1475", {"start": v(11.86, 57.09) * mm, "end": v(11.89, 57.1) * mm});
            skLineSegment(sketch, "E1476", {"start": v(11.89, 57.1) * mm, "end": v(11.92, 57.1) * mm});
            skLineSegment(sketch, "E1477", {"start": v(11.92, 57.1) * mm, "end": v(11.95, 57.12) * mm});
            skLineSegment(sketch, "E1478", {"start": v(11.95, 57.12) * mm, "end": v(11.97, 57.14) * mm});
            skLineSegment(sketch, "E1479", {"start": v(11.97, 57.14) * mm, "end": v(12, 57.17) * mm});
            skLineSegment(sketch, "E1480", {"start": v(12, 57.17) * mm, "end": v(12.02, 57.2) * mm});
            skLineSegment(sketch, "E1481", {"start": v(12.02, 57.2) * mm, "end": v(12.03, 57.22) * mm});
            skLineSegment(sketch, "E1482", {"start": v(12.03, 57.22) * mm, "end": v(12.04, 57.25) * mm});
            skLineSegment(sketch, "E1483", {"start": v(12.04, 57.25) * mm, "end": v(12.05, 57.28) * mm});
            skLineSegment(sketch, "E1484", {"start": v(12.05, 57.28) * mm, "end": v(12.05, 57.31) * mm});
            skLineSegment(sketch, "E1485", {"start": v(12.05, 57.31) * mm, "end": v(12.04, 57.34) * mm});
            skLineSegment(sketch, "E1486", {"start": v(12.04, 57.34) * mm, "end": v(12.03, 57.37) * mm});
            skLineSegment(sketch, "E1487", {"start": v(12.03, 57.37) * mm, "end": v(12.01, 57.4) * mm});
            skLineSegment(sketch, "E1488", {"start": v(12.01, 57.4) * mm, "end": v(10.97, 58.45) * mm});
            skLineSegment(sketch, "E1489", {"start": v(10.97, 58.45) * mm, "end": v(10.33, 57.81) * mm});
            skLineSegment(sketch, "E1490", {"start": v(10.33, 57.81) * mm, "end": v(10.59, 57.56) * mm});
            skLineSegment(sketch, "E1491", {"start": v(10.59, 57.56) * mm, "end": v(10.66, 57.56) * mm});
            skLineSegment(sketch, "E1492", {"start": v(10.66, 57.56) * mm, "end": v(10.76, 57.57) * mm});
            skLineSegment(sketch, "E1493", {"start": v(10.76, 57.57) * mm, "end": v(10.87, 57.56) * mm});
            skLineSegment(sketch, "E1494", {"start": v(10.87, 57.56) * mm, "end": v(10.98, 57.53) * mm});
            skLineSegment(sketch, "E1495", {"start": v(10.98, 57.53) * mm, "end": v(11.1, 57.5) * mm});
            skLineSegment(sketch, "E1496", {"start": v(11.1, 57.5) * mm, "end": v(11.13, 57.48) * mm});
            skLineSegment(sketch, "E1497", {"start": v(11.13, 57.48) * mm, "end": v(11.2, 57.45) * mm});
            skLineSegment(sketch, "E1498", {"start": v(11.2, 57.45) * mm, "end": v(11.32, 57.38) * mm});
            skLineSegment(sketch, "E1499", {"start": v(11.32, 57.38) * mm, "end": v(11.37, 57.36) * mm});
            skLineSegment(sketch, "E1500", {"start": v(11.37, 57.36) * mm, "end": v(11.37, 57.36) * mm});
            skLineSegment(sketch, "E1501", {"start": v(11.37, 57.36) * mm, "end": v(11.38, 57.36) * mm});
            skLineSegment(sketch, "E1502", {"start": v(11.38, 57.36) * mm, "end": v(11.38, 57.36) * mm});
            skLineSegment(sketch, "E1503", {"start": v(11.38, 57.36) * mm, "end": v(11.38, 57.35) * mm});
            skLineSegment(sketch, "E1504", {"start": v(11.38, 57.35) * mm, "end": v(11.38, 57.35) * mm});
            skLineSegment(sketch, "E1505", {"start": v(11.38, 57.35) * mm, "end": v(11.39, 57.35) * mm});
            skLineSegment(sketch, "E1506", {"start": v(11.39, 57.35) * mm, "end": v(11.45, 57.3) * mm});
            skLineSegment(sketch, "E1507", {"start": v(11.45, 57.3) * mm, "end": v(11.6, 57.2) * mm});
            skLineSegment(sketch, "E1508", {"start": v(11.6, 57.2) * mm, "end": v(11.69, 57.14) * mm});
            skLineSegment(sketch, "E1509", {"start": v(11.69, 57.14) * mm, "end": v(11.72, 57.13) * mm});
            skLineSegment(sketch, "E1510", {"start": v(11.72, 57.13) * mm, "end": v(11.78, 57.1) * mm});
            skLineSegment(sketch, "E1511", {"start": v(-7.3, 54.82) * mm, "end": v(-7.27, 54.82) * mm});
            skLineSegment(sketch, "E1512", {"start": v(-7.27, 54.82) * mm, "end": v(-7.25, 54.82) * mm});
            skLineSegment(sketch, "E1513", {"start": v(-7.25, 54.82) * mm, "end": v(-7.22, 54.83) * mm});
            skLineSegment(sketch, "E1514", {"start": v(-7.22, 54.83) * mm, "end": v(-7.19, 54.84) * mm});
            skLineSegment(sketch, "E1515", {"start": v(-7.19, 54.84) * mm, "end": v(-7.16, 54.86) * mm});
            skLineSegment(sketch, "E1516", {"start": v(-7.16, 54.86) * mm, "end": v(-7.12, 54.88) * mm});
            skLineSegment(sketch, "E1517", {"start": v(-7.12, 54.88) * mm, "end": v(-5.92, 56.09) * mm});
            skLineSegment(sketch, "E1518", {"start": v(-5.92, 56.09) * mm, "end": v(-5.9, 56.1) * mm});
            skLineSegment(sketch, "E1519", {"start": v(-5.9, 56.1) * mm, "end": v(-5.88, 56.15) * mm});
            skLineSegment(sketch, "E1520", {"start": v(-5.88, 56.15) * mm, "end": v(-5.86, 56.2) * mm});
            skLineSegment(sketch, "E1521", {"start": v(-5.86, 56.2) * mm, "end": v(-5.86, 56.24) * mm});
            skLineSegment(sketch, "E1522", {"start": v(-5.86, 56.24) * mm, "end": v(-5.86, 56.27) * mm});
            skLineSegment(sketch, "E1523", {"start": v(-5.86, 56.27) * mm, "end": v(-5.87, 56.3) * mm});
            skLineSegment(sketch, "E1524", {"start": v(-5.87, 56.3) * mm, "end": v(-5.88, 56.33) * mm});
            skLineSegment(sketch, "E1525", {"start": v(-5.88, 56.33) * mm, "end": v(-5.9, 56.35) * mm});
            skLineSegment(sketch, "E1526", {"start": v(-5.9, 56.35) * mm, "end": v(-5.93, 56.37) * mm});
            skLineSegment(sketch, "E1527", {"start": v(-5.93, 56.37) * mm, "end": v(-5.95, 56.39) * mm});
            skLineSegment(sketch, "E1528", {"start": v(-5.95, 56.39) * mm, "end": v(-5.97, 56.4) * mm});
            skLineSegment(sketch, "E1529", {"start": v(-5.97, 56.4) * mm, "end": v(-6, 56.4) * mm});
            skLineSegment(sketch, "E1530", {"start": v(-6, 56.4) * mm, "end": v(-6.02, 56.4) * mm});
            skLineSegment(sketch, "E1531", {"start": v(-6.02, 56.4) * mm, "end": v(-6.05, 56.4) * mm});
            skLineSegment(sketch, "E1532", {"start": v(-6.05, 56.4) * mm, "end": v(-6.08, 56.38) * mm});
            skLineSegment(sketch, "E1533", {"start": v(-6.08, 56.38) * mm, "end": v(-6.12, 56.37) * mm});
            skLineSegment(sketch, "E1534", {"start": v(-6.12, 56.37) * mm, "end": v(-6.19, 56.34) * mm});
            skLineSegment(sketch, "E1535", {"start": v(-6.19, 56.34) * mm, "end": v(-6.24, 56.32) * mm});
            skLineSegment(sketch, "E1536", {"start": v(-6.24, 56.32) * mm, "end": v(-6.27, 56.32) * mm});
            skLineSegment(sketch, "E1537", {"start": v(-6.27, 56.32) * mm, "end": v(-6.3, 56.32) * mm});
            skLineSegment(sketch, "E1538", {"start": v(-6.3, 56.32) * mm, "end": v(-6.33, 56.33) * mm});
            skLineSegment(sketch, "E1539", {"start": v(-6.33, 56.33) * mm, "end": v(-6.36, 56.35) * mm});
            skLineSegment(sketch, "E1540", {"start": v(-6.36, 56.35) * mm, "end": v(-9.12, 59.1) * mm});
            skLineSegment(sketch, "E1541", {"start": v(-9.12, 59.1) * mm, "end": v(-10.14, 58.09) * mm});
            skLineSegment(sketch, "E1542", {"start": v(-10.14, 58.09) * mm, "end": v(-7.38, 55.33) * mm});
            skLineSegment(sketch, "E1543", {"start": v(-7.38, 55.33) * mm, "end": v(-7.37, 55.3) * mm});
            skLineSegment(sketch, "E1544", {"start": v(-7.37, 55.3) * mm, "end": v(-7.35, 55.27) * mm});
            skLineSegment(sketch, "E1545", {"start": v(-7.35, 55.27) * mm, "end": v(-7.35, 55.24) * mm});
            skLineSegment(sketch, "E1546", {"start": v(-7.35, 55.24) * mm, "end": v(-7.35, 55.22) * mm});
            skLineSegment(sketch, "E1547", {"start": v(-7.35, 55.22) * mm, "end": v(-7.36, 55.19) * mm});
            skLineSegment(sketch, "E1548", {"start": v(-7.36, 55.19) * mm, "end": v(-7.37, 55.16) * mm});
            skLineSegment(sketch, "E1549", {"start": v(-7.37, 55.16) * mm, "end": v(-7.4, 55.1) * mm});
            skLineSegment(sketch, "E1550", {"start": v(-7.4, 55.1) * mm, "end": v(-7.42, 55.03) * mm});
            skLineSegment(sketch, "E1551", {"start": v(-7.42, 55.03) * mm, "end": v(-7.43, 54.98) * mm});
            skLineSegment(sketch, "E1552", {"start": v(-7.43, 54.98) * mm, "end": v(-7.43, 54.94) * mm});
            skLineSegment(sketch, "E1553", {"start": v(-7.43, 54.94) * mm, "end": v(-7.41, 54.9) * mm});
            skLineSegment(sketch, "E1554", {"start": v(-7.41, 54.9) * mm, "end": v(-7.4, 54.88) * mm});
            skLineSegment(sketch, "E1555", {"start": v(-7.4, 54.88) * mm, "end": v(-7.37, 54.85) * mm});
            skLineSegment(sketch, "E1556", {"start": v(-7.37, 54.85) * mm, "end": v(-7.34, 54.84) * mm});
            skLineSegment(sketch, "E1557", {"start": v(-7.34, 54.84) * mm, "end": v(-7.3, 54.82) * mm});
            skLineSegment(sketch, "E1558", {"start": v(-3.6, 58.57) * mm, "end": v(-3.57, 58.56) * mm});
            skLineSegment(sketch, "E1559", {"start": v(-3.57, 58.56) * mm, "end": v(-3.53, 58.56) * mm});
            skLineSegment(sketch, "E1560", {"start": v(-3.53, 58.56) * mm, "end": v(-3.48, 58.56) * mm});
            skLineSegment(sketch, "E1561", {"start": v(-3.48, 58.56) * mm, "end": v(-3.44, 58.58) * mm});
            skLineSegment(sketch, "E1562", {"start": v(-3.44, 58.58) * mm, "end": v(-3.4, 58.6) * mm});
            skLineSegment(sketch, "E1563", {"start": v(-3.4, 58.6) * mm, "end": v(-2.16, 59.84) * mm});
            skLineSegment(sketch, "E1564", {"start": v(-2.16, 59.84) * mm, "end": v(-2.14, 59.88) * mm});
            skLineSegment(sketch, "E1565", {"start": v(-2.14, 59.88) * mm, "end": v(-2.13, 59.92) * mm});
            skLineSegment(sketch, "E1566", {"start": v(-2.13, 59.92) * mm, "end": v(-2.12, 59.96) * mm});
            skLineSegment(sketch, "E1567", {"start": v(-2.12, 59.96) * mm, "end": v(-2.12, 60) * mm});
            skLineSegment(sketch, "E1568", {"start": v(-2.12, 60) * mm, "end": v(-2.13, 60.04) * mm});
            skLineSegment(sketch, "E1569", {"start": v(-2.13, 60.04) * mm, "end": v(-2.15, 60.06) * mm});
            skLineSegment(sketch, "E1570", {"start": v(-2.15, 60.06) * mm, "end": v(-2.17, 60.1) * mm});
            skLineSegment(sketch, "E1571", {"start": v(-2.17, 60.1) * mm, "end": v(-2.2, 60.11) * mm});
            skLineSegment(sketch, "E1572", {"start": v(-2.2, 60.11) * mm, "end": v(-2.23, 60.13) * mm});
            skLineSegment(sketch, "E1573", {"start": v(-2.23, 60.13) * mm, "end": v(-2.26, 60.14) * mm});
            skLineSegment(sketch, "E1574", {"start": v(-2.26, 60.14) * mm, "end": v(-2.3, 60.13) * mm});
            skLineSegment(sketch, "E1575", {"start": v(-2.3, 60.13) * mm, "end": v(-2.34, 60.12) * mm});
            skLineSegment(sketch, "E1576", {"start": v(-2.34, 60.12) * mm, "end": v(-2.39, 60.1) * mm});
            skLineSegment(sketch, "E1577", {"start": v(-2.39, 60.1) * mm, "end": v(-2.46, 60.07) * mm});
            skLineSegment(sketch, "E1578", {"start": v(-2.46, 60.07) * mm, "end": v(-2.51, 60.05) * mm});
            skLineSegment(sketch, "E1579", {"start": v(-2.51, 60.05) * mm, "end": v(-2.53, 60.05) * mm});
            skLineSegment(sketch, "E1580", {"start": v(-2.53, 60.05) * mm, "end": v(-2.56, 60.06) * mm});
            skLineSegment(sketch, "E1581", {"start": v(-2.56, 60.06) * mm, "end": v(-2.6, 60.07) * mm});
            skLineSegment(sketch, "E1582", {"start": v(-2.6, 60.07) * mm, "end": v(-2.63, 60.09) * mm});
            skLineSegment(sketch, "E1583", {"start": v(-2.63, 60.09) * mm, "end": v(-5.02, 62.48) * mm});
            skLineSegment(sketch, "E1584", {"start": v(-5.02, 62.48) * mm, "end": v(-5.04, 62.51) * mm});
            skLineSegment(sketch, "E1585", {"start": v(-5.04, 62.51) * mm, "end": v(-5.05, 62.54) * mm});
            skLineSegment(sketch, "E1586", {"start": v(-5.05, 62.54) * mm, "end": v(-5.06, 62.57) * mm});
            skLineSegment(sketch, "E1587", {"start": v(-5.06, 62.57) * mm, "end": v(-5.06, 62.6) * mm});
            skLineSegment(sketch, "E1588", {"start": v(-5.06, 62.6) * mm, "end": v(-5.05, 62.62) * mm});
            skLineSegment(sketch, "E1589", {"start": v(-5.05, 62.62) * mm, "end": v(-5.04, 62.65) * mm});
            skLineSegment(sketch, "E1590", {"start": v(-5.04, 62.65) * mm, "end": v(-5.01, 62.72) * mm});
            skLineSegment(sketch, "E1591", {"start": v(-5.01, 62.72) * mm, "end": v(-4.99, 62.78) * mm});
            skLineSegment(sketch, "E1592", {"start": v(-4.99, 62.78) * mm, "end": v(-4.98, 62.82) * mm});
            skLineSegment(sketch, "E1593", {"start": v(-4.98, 62.82) * mm, "end": v(-4.98, 62.87) * mm});
            skLineSegment(sketch, "E1594", {"start": v(-4.98, 62.87) * mm, "end": v(-5, 62.9) * mm});
            skLineSegment(sketch, "E1595", {"start": v(-5, 62.9) * mm, "end": v(-5.02, 62.95) * mm});
            skLineSegment(sketch, "E1596", {"start": v(-5.02, 62.95) * mm, "end": v(-5.06, 62.98) * mm});
            skLineSegment(sketch, "E1597", {"start": v(-5.06, 62.98) * mm, "end": v(-5.1, 62.99) * mm});
            skLineSegment(sketch, "E1598", {"start": v(-5.1, 62.99) * mm, "end": v(-5.14, 63) * mm});
            skLineSegment(sketch, "E1599", {"start": v(-5.14, 63) * mm, "end": v(-5.18, 62.99) * mm});
            skLineSegment(sketch, "E1600", {"start": v(-5.18, 62.99) * mm, "end": v(-5.23, 62.97) * mm});
            skLineSegment(sketch, "E1601", {"start": v(-5.23, 62.97) * mm, "end": v(-5.27, 62.95) * mm});
            skLineSegment(sketch, "E1602", {"start": v(-5.27, 62.95) * mm, "end": v(-6.5, 61.71) * mm});
            skLineSegment(sketch, "E1603", {"start": v(-6.5, 61.71) * mm, "end": v(-6.53, 61.67) * mm});
            skLineSegment(sketch, "E1604", {"start": v(-6.53, 61.67) * mm, "end": v(-6.54, 61.63) * mm});
            skLineSegment(sketch, "E1605", {"start": v(-6.54, 61.63) * mm, "end": v(-6.55, 61.6) * mm});
            skLineSegment(sketch, "E1606", {"start": v(-6.55, 61.6) * mm, "end": v(-6.55, 61.57) * mm});
            skLineSegment(sketch, "E1607", {"start": v(-6.55, 61.57) * mm, "end": v(-6.55, 61.54) * mm});
            skLineSegment(sketch, "E1608", {"start": v(-6.55, 61.54) * mm, "end": v(-6.54, 61.51) * mm});
            skLineSegment(sketch, "E1609", {"start": v(-6.54, 61.51) * mm, "end": v(-6.52, 61.48) * mm});
            skLineSegment(sketch, "E1610", {"start": v(-6.52, 61.48) * mm, "end": v(-6.5, 61.46) * mm});
            skLineSegment(sketch, "E1611", {"start": v(-6.5, 61.46) * mm, "end": v(-6.47, 61.44) * mm});
            skLineSegment(sketch, "E1612", {"start": v(-6.47, 61.44) * mm, "end": v(-6.44, 61.42) * mm});
            skLineSegment(sketch, "E1613", {"start": v(-6.44, 61.42) * mm, "end": v(-6.4, 61.42) * mm});
            skLineSegment(sketch, "E1614", {"start": v(-6.4, 61.42) * mm, "end": v(-6.37, 61.42) * mm});
            skLineSegment(sketch, "E1615", {"start": v(-6.37, 61.42) * mm, "end": v(-6.35, 61.42) * mm});
            skLineSegment(sketch, "E1616", {"start": v(-6.35, 61.42) * mm, "end": v(-6.3, 61.45) * mm});
            skLineSegment(sketch, "E1617", {"start": v(-6.3, 61.45) * mm, "end": v(-6.2, 61.48) * mm});
            skLineSegment(sketch, "E1618", {"start": v(-6.2, 61.48) * mm, "end": v(-6.17, 61.5) * mm});
            skLineSegment(sketch, "E1619", {"start": v(-6.17, 61.5) * mm, "end": v(-6.14, 61.5) * mm});
            skLineSegment(sketch, "E1620", {"start": v(-6.14, 61.5) * mm, "end": v(-6.12, 61.5) * mm});
            skLineSegment(sketch, "E1621", {"start": v(-6.12, 61.5) * mm, "end": v(-6.1, 61.5) * mm});
            skLineSegment(sketch, "E1622", {"start": v(-6.1, 61.5) * mm, "end": v(-6.07, 61.48) * mm});
            skLineSegment(sketch, "E1623", {"start": v(-6.07, 61.48) * mm, "end": v(-6.05, 61.46) * mm});
            skLineSegment(sketch, "E1624", {"start": v(-6.05, 61.46) * mm, "end": v(-6.02, 61.44) * mm});
            skLineSegment(sketch, "E1625", {"start": v(-6.02, 61.44) * mm, "end": v(-5.01, 60.43) * mm});
            skLineSegment(sketch, "E1626", {"start": v(-5.01, 60.43) * mm, "end": v(-5, 60.4) * mm});
            skLineSegment(sketch, "E1627", {"start": v(-5, 60.4) * mm, "end": v(-5.35, 60.04) * mm});
            skLineSegment(sketch, "E1628", {"start": v(-5.35, 60.04) * mm, "end": v(-5.11, 59.8) * mm});
            skLineSegment(sketch, "E1629", {"start": v(-5.11, 59.8) * mm, "end": v(-4.75, 60.17) * mm});
            skLineSegment(sketch, "E1630", {"start": v(-4.75, 60.17) * mm, "end": v(-3.67, 59.09) * mm});
            skLineSegment(sketch, "E1631", {"start": v(-3.67, 59.09) * mm, "end": v(-3.65, 59.06) * mm});
            skLineSegment(sketch, "E1632", {"start": v(-3.65, 59.06) * mm, "end": v(-3.62, 59.01) * mm});
            skLineSegment(sketch, "E1633", {"start": v(-3.62, 59.01) * mm, "end": v(-3.62, 58.98) * mm});
            skLineSegment(sketch, "E1634", {"start": v(-3.62, 58.98) * mm, "end": v(-3.62, 58.93) * mm});
            skLineSegment(sketch, "E1635", {"start": v(-3.62, 58.93) * mm, "end": v(-3.64, 58.88) * mm});
            skLineSegment(sketch, "E1636", {"start": v(-3.64, 58.88) * mm, "end": v(-3.66, 58.82) * mm});
            skLineSegment(sketch, "E1637", {"start": v(-3.66, 58.82) * mm, "end": v(-3.68, 58.78) * mm});
            skLineSegment(sketch, "E1638", {"start": v(-3.68, 58.78) * mm, "end": v(-3.7, 58.75) * mm});
            skLineSegment(sketch, "E1639", {"start": v(-3.7, 58.75) * mm, "end": v(-3.7, 58.72) * mm});
            skLineSegment(sketch, "E1640", {"start": v(-3.7, 58.72) * mm, "end": v(-3.7, 58.7) * mm});
            skLineSegment(sketch, "E1641", {"start": v(-3.7, 58.7) * mm, "end": v(-3.69, 58.66) * mm});
            skLineSegment(sketch, "E1642", {"start": v(-3.69, 58.66) * mm, "end": v(-3.67, 58.63) * mm});
            skLineSegment(sketch, "E1643", {"start": v(-3.67, 58.63) * mm, "end": v(-3.64, 58.6) * mm});
            skLineSegment(sketch, "E1644", {"start": v(-3.64, 58.6) * mm, "end": v(-3.6, 58.57) * mm});
            skLineSegment(sketch, "E1645", {"start": v(-7.56, 58.62) * mm, "end": v(-7.53, 58.61) * mm});
            skLineSegment(sketch, "E1646", {"start": v(-7.53, 58.61) * mm, "end": v(-7.5, 58.61) * mm});
            skLineSegment(sketch, "E1647", {"start": v(-7.5, 58.61) * mm, "end": v(-7.47, 58.62) * mm});
            skLineSegment(sketch, "E1648", {"start": v(-7.47, 58.62) * mm, "end": v(-7.44, 58.63) * mm});
            skLineSegment(sketch, "E1649", {"start": v(-7.44, 58.63) * mm, "end": v(-7.4, 58.64) * mm});
            skLineSegment(sketch, "E1650", {"start": v(-7.4, 58.64) * mm, "end": v(-7.38, 58.67) * mm});
            skLineSegment(sketch, "E1651", {"start": v(-7.38, 58.67) * mm, "end": v(-7.35, 58.7) * mm});
            skLineSegment(sketch, "E1652", {"start": v(-7.35, 58.7) * mm, "end": v(-7.33, 58.73) * mm});
            skLineSegment(sketch, "E1653", {"start": v(-7.33, 58.73) * mm, "end": v(-7.32, 58.77) * mm});
            skLineSegment(sketch, "E1654", {"start": v(-7.32, 58.77) * mm, "end": v(-7.32, 58.8) * mm});
            skLineSegment(sketch, "E1655", {"start": v(-7.32, 58.8) * mm, "end": v(-7.32, 58.84) * mm});
            skLineSegment(sketch, "E1656", {"start": v(-7.32, 58.84) * mm, "end": v(-7.34, 58.88) * mm});
            skLineSegment(sketch, "E1657", {"start": v(-7.34, 58.88) * mm, "end": v(-7.35, 58.91) * mm});
            skLineSegment(sketch, "E1658", {"start": v(-7.35, 58.91) * mm, "end": v(-8.33, 59.89) * mm});
            skLineSegment(sketch, "E1659", {"start": v(-8.33, 59.89) * mm, "end": v(-8.93, 59.3) * mm});
            skLineSegment(sketch, "E1660", {"start": v(-8.93, 59.3) * mm, "end": v(-8.7, 59.05) * mm});
            skLineSegment(sketch, "E1661", {"start": v(-8.7, 59.05) * mm, "end": v(-8.62, 59.06) * mm});
            skLineSegment(sketch, "E1662", {"start": v(-8.62, 59.06) * mm, "end": v(-8.57, 59.06) * mm});
            skLineSegment(sketch, "E1663", {"start": v(-8.57, 59.06) * mm, "end": v(-8.51, 59.06) * mm});
            skLineSegment(sketch, "E1664", {"start": v(-8.51, 59.06) * mm, "end": v(-8.45, 59.06) * mm});
            skLineSegment(sketch, "E1665", {"start": v(-8.45, 59.06) * mm, "end": v(-8.4, 59.05) * mm});
            skLineSegment(sketch, "E1666", {"start": v(-8.4, 59.05) * mm, "end": v(-8.33, 59.03) * mm});
            skLineSegment(sketch, "E1667", {"start": v(-8.33, 59.03) * mm, "end": v(-8.27, 59.01) * mm});
            skLineSegment(sketch, "E1668", {"start": v(-8.27, 59.01) * mm, "end": v(-8.2, 59) * mm});
            skLineSegment(sketch, "E1669", {"start": v(-8.2, 59) * mm, "end": v(-8.14, 58.97) * mm});
            skLineSegment(sketch, "E1670", {"start": v(-8.14, 58.97) * mm, "end": v(-8.05, 58.92) * mm});
            skLineSegment(sketch, "E1671", {"start": v(-8.05, 58.92) * mm, "end": v(-7.96, 58.87) * mm});
            skLineSegment(sketch, "E1672", {"start": v(-7.96, 58.87) * mm, "end": v(-7.85, 58.8) * mm});
            skLineSegment(sketch, "E1673", {"start": v(-7.85, 58.8) * mm, "end": v(-7.72, 58.71) * mm});
            skLineSegment(sketch, "E1674", {"start": v(-7.72, 58.71) * mm, "end": v(-7.65, 58.66) * mm});
            skLineSegment(sketch, "E1675", {"start": v(-7.65, 58.66) * mm, "end": v(-7.61, 58.64) * mm});
            skLineSegment(sketch, "E1676", {"start": v(-7.61, 58.64) * mm, "end": v(-7.56, 58.62) * mm});
            skLineSegment(sketch, "E1677", {"start": v(9.29, 59.5) * mm, "end": v(9.29, 59.5) * mm});
            skLineSegment(sketch, "E1678", {"start": v(9.29, 59.5) * mm, "end": v(9.28, 59.5) * mm});
            skLineSegment(sketch, "E1679", {"start": v(9.28, 59.5) * mm, "end": v(9.29, 59.5) * mm});
            skLineSegment(sketch, "E1680", {"start": v(9.18, 59.64) * mm, "end": v(9.17, 59.64) * mm});
            skLineSegment(sketch, "E1681", {"start": v(9.17, 59.64) * mm, "end": v(9.17, 59.64) * mm});
            skLineSegment(sketch, "E1682", {"start": v(9.17, 59.64) * mm, "end": v(9.18, 59.64) * mm});
            skLineSegment(sketch, "E1683", {"start": v(-5.17, 57) * mm, "end": v(-5.14, 56.99) * mm});
            skLineSegment(sketch, "E1684", {"start": v(-5.14, 56.99) * mm, "end": v(-5.1, 56.99) * mm});
            skLineSegment(sketch, "E1685", {"start": v(-5.1, 56.99) * mm, "end": v(-5.06, 57) * mm});
            skLineSegment(sketch, "E1686", {"start": v(-5.06, 57) * mm, "end": v(-5.02, 57) * mm});
            skLineSegment(sketch, "E1687", {"start": v(-5.02, 57) * mm, "end": v(-4.98, 57.03) * mm});
            skLineSegment(sketch, "E1688", {"start": v(-4.98, 57.03) * mm, "end": v(-3.73, 58.27) * mm});
            skLineSegment(sketch, "E1689", {"start": v(-3.73, 58.27) * mm, "end": v(-3.71, 58.31) * mm});
            skLineSegment(sketch, "E1690", {"start": v(-3.71, 58.31) * mm, "end": v(-3.7, 58.35) * mm});
            skLineSegment(sketch, "E1691", {"start": v(-3.7, 58.35) * mm, "end": v(-3.7, 58.4) * mm});
            skLineSegment(sketch, "E1692", {"start": v(-3.7, 58.4) * mm, "end": v(-3.7, 58.43) * mm});
            skLineSegment(sketch, "E1693", {"start": v(-3.7, 58.43) * mm, "end": v(-3.7, 58.47) * mm});
            skLineSegment(sketch, "E1694", {"start": v(-3.7, 58.47) * mm, "end": v(-3.72, 58.5) * mm});
            skLineSegment(sketch, "E1695", {"start": v(-3.72, 58.5) * mm, "end": v(-3.74, 58.51) * mm});
            skLineSegment(sketch, "E1696", {"start": v(-3.74, 58.51) * mm, "end": v(-3.76, 58.53) * mm});
            skLineSegment(sketch, "E1697", {"start": v(-3.76, 58.53) * mm, "end": v(-3.78, 58.55) * mm});
            skLineSegment(sketch, "E1698", {"start": v(-3.78, 58.55) * mm, "end": v(-3.8, 58.56) * mm});
            skLineSegment(sketch, "E1699", {"start": v(-3.8, 58.56) * mm, "end": v(-3.83, 58.56) * mm});
            skLineSegment(sketch, "E1700", {"start": v(-3.83, 58.56) * mm, "end": v(-3.86, 58.56) * mm});
            skLineSegment(sketch, "E1701", {"start": v(-3.86, 58.56) * mm, "end": v(-3.88, 58.56) * mm});
            skLineSegment(sketch, "E1702", {"start": v(-3.88, 58.56) * mm, "end": v(-3.9, 58.55) * mm});
            skLineSegment(sketch, "E1703", {"start": v(-3.9, 58.55) * mm, "end": v(-3.98, 58.52) * mm});
            skLineSegment(sketch, "E1704", {"start": v(-3.98, 58.52) * mm, "end": v(-4.05, 58.5) * mm});
            skLineSegment(sketch, "E1705", {"start": v(-4.05, 58.5) * mm, "end": v(-4.1, 58.48) * mm});
            skLineSegment(sketch, "E1706", {"start": v(-4.1, 58.48) * mm, "end": v(-4.13, 58.48) * mm});
            skLineSegment(sketch, "E1707", {"start": v(-4.13, 58.48) * mm, "end": v(-4.16, 58.5) * mm});
            skLineSegment(sketch, "E1708", {"start": v(-4.16, 58.5) * mm, "end": v(-4.19, 58.5) * mm});
            skLineSegment(sketch, "E1709", {"start": v(-4.19, 58.5) * mm, "end": v(-6.6, 60.91) * mm});
            skLineSegment(sketch, "E1710", {"start": v(-6.6, 60.91) * mm, "end": v(-6.61, 60.94) * mm});
            skLineSegment(sketch, "E1711", {"start": v(-6.61, 60.94) * mm, "end": v(-6.63, 61) * mm});
            skLineSegment(sketch, "E1712", {"start": v(-6.63, 61) * mm, "end": v(-6.63, 61.02) * mm});
            skLineSegment(sketch, "E1713", {"start": v(-6.63, 61.02) * mm, "end": v(-6.63, 61.03) * mm});
            skLineSegment(sketch, "E1714", {"start": v(-6.63, 61.03) * mm, "end": v(-6.62, 61.06) * mm});
            skLineSegment(sketch, "E1715", {"start": v(-6.62, 61.06) * mm, "end": v(-6.61, 61.08) * mm});
            skLineSegment(sketch, "E1716", {"start": v(-6.61, 61.08) * mm, "end": v(-6.58, 61.15) * mm});
            skLineSegment(sketch, "E1717", {"start": v(-6.58, 61.15) * mm, "end": v(-6.56, 61.21) * mm});
            skLineSegment(sketch, "E1718", {"start": v(-6.56, 61.21) * mm, "end": v(-6.55, 61.26) * mm});
            skLineSegment(sketch, "E1719", {"start": v(-6.55, 61.26) * mm, "end": v(-6.55, 61.3) * mm});
            skLineSegment(sketch, "E1720", {"start": v(-6.55, 61.3) * mm, "end": v(-6.57, 61.33) * mm});
            skLineSegment(sketch, "E1721", {"start": v(-6.57, 61.33) * mm, "end": v(-6.59, 61.36) * mm});
            skLineSegment(sketch, "E1722", {"start": v(-6.59, 61.36) * mm, "end": v(-6.62, 61.39) * mm});
            skLineSegment(sketch, "E1723", {"start": v(-6.62, 61.39) * mm, "end": v(-6.65, 61.4) * mm});
            skLineSegment(sketch, "E1724", {"start": v(-6.65, 61.4) * mm, "end": v(-6.68, 61.42) * mm});
            skLineSegment(sketch, "E1725", {"start": v(-6.68, 61.42) * mm, "end": v(-6.72, 61.42) * mm});
            skLineSegment(sketch, "E1726", {"start": v(-6.72, 61.42) * mm, "end": v(-6.75, 61.41) * mm});
            skLineSegment(sketch, "E1727", {"start": v(-6.75, 61.41) * mm, "end": v(-6.8, 61.4) * mm});
            skLineSegment(sketch, "E1728", {"start": v(-6.8, 61.4) * mm, "end": v(-6.83, 61.38) * mm});
            skLineSegment(sketch, "E1729", {"start": v(-6.83, 61.38) * mm, "end": v(-6.87, 61.35) * mm});
            skLineSegment(sketch, "E1730", {"start": v(-6.87, 61.35) * mm, "end": v(-8.08, 60.14) * mm});
            skLineSegment(sketch, "E1731", {"start": v(-8.08, 60.14) * mm, "end": v(-8.1, 60.1) * mm});
            skLineSegment(sketch, "E1732", {"start": v(-8.1, 60.1) * mm, "end": v(-8.12, 60.05) * mm});
            skLineSegment(sketch, "E1733", {"start": v(-8.12, 60.05) * mm, "end": v(-8.12, 60) * mm});
            skLineSegment(sketch, "E1734", {"start": v(-8.12, 60) * mm, "end": v(-8.12, 59.97) * mm});
            skLineSegment(sketch, "E1735", {"start": v(-8.12, 59.97) * mm, "end": v(-8.11, 59.94) * mm});
            skLineSegment(sketch, "E1736", {"start": v(-8.11, 59.94) * mm, "end": v(-8.1, 59.92) * mm});
            skLineSegment(sketch, "E1737", {"start": v(-8.1, 59.92) * mm, "end": v(-8.08, 59.9) * mm});
            skLineSegment(sketch, "E1738", {"start": v(-8.08, 59.9) * mm, "end": v(-8.05, 59.87) * mm});
            skLineSegment(sketch, "E1739", {"start": v(-8.05, 59.87) * mm, "end": v(-8.03, 59.85) * mm});
            skLineSegment(sketch, "E1740", {"start": v(-8.03, 59.85) * mm, "end": v(-8, 59.85) * mm});
            skLineSegment(sketch, "E1741", {"start": v(-8, 59.85) * mm, "end": v(-7.97, 59.85) * mm});
            skLineSegment(sketch, "E1742", {"start": v(-7.97, 59.85) * mm, "end": v(-7.94, 59.85) * mm});
            skLineSegment(sketch, "E1743", {"start": v(-7.94, 59.85) * mm, "end": v(-7.92, 59.85) * mm});
            skLineSegment(sketch, "E1744", {"start": v(-7.92, 59.85) * mm, "end": v(-7.86, 59.88) * mm});
            skLineSegment(sketch, "E1745", {"start": v(-7.86, 59.88) * mm, "end": v(-7.8, 59.9) * mm});
            skLineSegment(sketch, "E1746", {"start": v(-7.8, 59.9) * mm, "end": v(-7.76, 59.92) * mm});
            skLineSegment(sketch, "E1747", {"start": v(-7.76, 59.92) * mm, "end": v(-7.73, 59.92) * mm});
            skLineSegment(sketch, "E1748", {"start": v(-7.73, 59.92) * mm, "end": v(-7.7, 59.92) * mm});
            skLineSegment(sketch, "E1749", {"start": v(-7.7, 59.92) * mm, "end": v(-7.67, 59.92) * mm});
            skLineSegment(sketch, "E1750", {"start": v(-7.67, 59.92) * mm, "end": v(-7.64, 59.9) * mm});
            skLineSegment(sketch, "E1751", {"start": v(-7.64, 59.9) * mm, "end": v(-7.61, 59.88) * mm});
            skLineSegment(sketch, "E1752", {"start": v(-7.61, 59.88) * mm, "end": v(-5.22, 57.49) * mm});
            skLineSegment(sketch, "E1753", {"start": v(-5.22, 57.49) * mm, "end": v(-5.2, 57.46) * mm});
            skLineSegment(sketch, "E1754", {"start": v(-5.2, 57.46) * mm, "end": v(-5.19, 57.42) * mm});
            skLineSegment(sketch, "E1755", {"start": v(-5.19, 57.42) * mm, "end": v(-5.19, 57.4) * mm});
            skLineSegment(sketch, "E1756", {"start": v(-5.19, 57.4) * mm, "end": v(-5.19, 57.38) * mm});
            skLineSegment(sketch, "E1757", {"start": v(-5.19, 57.38) * mm, "end": v(-5.2, 57.32) * mm});
            skLineSegment(sketch, "E1758", {"start": v(-5.2, 57.32) * mm, "end": v(-5.24, 57.24) * mm});
            skLineSegment(sketch, "E1759", {"start": v(-5.24, 57.24) * mm, "end": v(-5.26, 57.19) * mm});
            skLineSegment(sketch, "E1760", {"start": v(-5.26, 57.19) * mm, "end": v(-5.27, 57.14) * mm});
            skLineSegment(sketch, "E1761", {"start": v(-5.27, 57.14) * mm, "end": v(-5.26, 57.1) * mm});
            skLineSegment(sketch, "E1762", {"start": v(-5.26, 57.1) * mm, "end": v(-5.25, 57.07) * mm});
            skLineSegment(sketch, "E1763", {"start": v(-5.25, 57.07) * mm, "end": v(-5.23, 57.04) * mm});
            skLineSegment(sketch, "E1764", {"start": v(-5.23, 57.04) * mm, "end": v(-5.21, 57.03) * mm});
            skLineSegment(sketch, "E1765", {"start": v(-5.21, 57.03) * mm, "end": v(-5.2, 57.01) * mm});
            skLineSegment(sketch, "E1766", {"start": v(-5.2, 57.01) * mm, "end": v(-5.17, 57) * mm});
            skLineSegment(sketch, "E1767", {"start": v(-0.75, 61.73) * mm, "end": v(-0.52, 61.49) * mm});
            skLineSegment(sketch, "E1768", {"start": v(-0.52, 61.49) * mm, "end": v(0.44, 62.44) * mm});
            skLineSegment(sketch, "E1769", {"start": v(0.44, 62.44) * mm, "end": v(-0.44, 63.32) * mm});
            skLineSegment(sketch, "E1770", {"start": v(-0.44, 63.32) * mm, "end": v(-0.47, 63.34) * mm});
            skLineSegment(sketch, "E1771", {"start": v(-0.47, 63.34) * mm, "end": v(-0.5, 63.34) * mm});
            skLineSegment(sketch, "E1772", {"start": v(-0.5, 63.34) * mm, "end": v(-0.52, 63.35) * mm});
            skLineSegment(sketch, "E1773", {"start": v(-0.52, 63.35) * mm, "end": v(-0.54, 63.35) * mm});
            skLineSegment(sketch, "E1774", {"start": v(-0.54, 63.35) * mm, "end": v(-0.57, 63.35) * mm});
            skLineSegment(sketch, "E1775", {"start": v(-0.57, 63.35) * mm, "end": v(-0.59, 63.34) * mm});
            skLineSegment(sketch, "E1776", {"start": v(-0.59, 63.34) * mm, "end": v(-0.6, 63.33) * mm});
            skLineSegment(sketch, "E1777", {"start": v(-0.6, 63.33) * mm, "end": v(-0.63, 63.31) * mm});
            skLineSegment(sketch, "E1778", {"start": v(-0.63, 63.31) * mm, "end": v(-0.65, 63.3) * mm});
            skLineSegment(sketch, "E1779", {"start": v(-0.65, 63.3) * mm, "end": v(-0.68, 63.26) * mm});
            skLineSegment(sketch, "E1780", {"start": v(-0.68, 63.26) * mm, "end": v(-0.69, 63.22) * mm});
            skLineSegment(sketch, "E1781", {"start": v(-0.69, 63.22) * mm, "end": v(-0.69, 63.17) * mm});
            skLineSegment(sketch, "E1782", {"start": v(-0.69, 63.17) * mm, "end": v(-0.68, 63.12) * mm});
            skLineSegment(sketch, "E1783", {"start": v(-0.68, 63.12) * mm, "end": v(-0.65, 63.03) * mm});
            skLineSegment(sketch, "E1784", {"start": v(-0.65, 63.03) * mm, "end": v(-0.6, 62.9) * mm});
            skLineSegment(sketch, "E1785", {"start": v(-0.6, 62.9) * mm, "end": v(-0.55, 62.77) * mm});
            skLineSegment(sketch, "E1786", {"start": v(-0.55, 62.77) * mm, "end": v(-0.52, 62.65) * mm});
            skLineSegment(sketch, "E1787", {"start": v(-0.52, 62.65) * mm, "end": v(-0.5, 62.52) * mm});
            skLineSegment(sketch, "E1788", {"start": v(-0.5, 62.52) * mm, "end": v(-0.5, 62.45) * mm});
            skLineSegment(sketch, "E1789", {"start": v(-0.5, 62.45) * mm, "end": v(-0.5, 62.37) * mm});
            skLineSegment(sketch, "E1790", {"start": v(-0.5, 62.37) * mm, "end": v(-0.52, 62.3) * mm});
            skLineSegment(sketch, "E1791", {"start": v(-0.52, 62.3) * mm, "end": v(-0.53, 62.22) * mm});
            skLineSegment(sketch, "E1792", {"start": v(-0.53, 62.22) * mm, "end": v(-0.55, 62.14) * mm});
            skLineSegment(sketch, "E1793", {"start": v(-0.55, 62.14) * mm, "end": v(-0.57, 62.07) * mm});
            skLineSegment(sketch, "E1794", {"start": v(-0.57, 62.07) * mm, "end": v(-0.6, 62) * mm});
            skLineSegment(sketch, "E1795", {"start": v(-0.6, 62) * mm, "end": v(-0.63, 61.92) * mm});
            skLineSegment(sketch, "E1796", {"start": v(-0.63, 61.92) * mm, "end": v(-0.65, 61.88) * mm});
            skLineSegment(sketch, "E1797", {"start": v(-0.65, 61.88) * mm, "end": v(-0.65, 61.87) * mm});
            skLineSegment(sketch, "E1798", {"start": v(-0.65, 61.87) * mm, "end": v(-0.66, 61.87) * mm});
            skLineSegment(sketch, "E1799", {"start": v(-0.66, 61.87) * mm, "end": v(-0.68, 61.83) * mm});
            skLineSegment(sketch, "E1800", {"start": v(-0.68, 61.83) * mm, "end": v(-0.73, 61.76) * mm});
            skLineSegment(sketch, "E1801", {"start": v(-0.73, 61.76) * mm, "end": v(-0.75, 61.73) * mm});
            skLineSegment(sketch, "E1802", {"start": v(-1.21, 62.83) * mm, "end": v(-1.17, 62.82) * mm});
            skLineSegment(sketch, "E1803", {"start": v(-1.17, 62.82) * mm, "end": v(-1.13, 62.83) * mm});
            skLineSegment(sketch, "E1804", {"start": v(-1.13, 62.83) * mm, "end": v(-1.09, 62.84) * mm});
            skLineSegment(sketch, "E1805", {"start": v(-1.09, 62.84) * mm, "end": v(-1.05, 62.87) * mm});
            skLineSegment(sketch, "E1806", {"start": v(-1.05, 62.87) * mm, "end": v(-1.03, 62.9) * mm});
            skLineSegment(sketch, "E1807", {"start": v(-1.03, 62.9) * mm, "end": v(-1.01, 62.94) * mm});
            skLineSegment(sketch, "E1808", {"start": v(-1.01, 62.94) * mm, "end": v(-1, 62.97) * mm});
            skLineSegment(sketch, "E1809", {"start": v(-1, 62.97) * mm, "end": v(-1, 63) * mm});
            skLineSegment(sketch, "E1810", {"start": v(-1, 63) * mm, "end": v(-1.02, 63.04) * mm});
            skLineSegment(sketch, "E1811", {"start": v(-1.02, 63.04) * mm, "end": v(-1.04, 63.08) * mm});
            skLineSegment(sketch, "E1812", {"start": v(-1.04, 63.08) * mm, "end": v(-2.1, 64.14) * mm});
            skLineSegment(sketch, "E1813", {"start": v(-2.1, 64.14) * mm, "end": v(-2.13, 64.16) * mm});
            skLineSegment(sketch, "E1814", {"start": v(-2.13, 64.16) * mm, "end": v(-2.17, 64.17) * mm});
            skLineSegment(sketch, "E1815", {"start": v(-2.17, 64.17) * mm, "end": v(-2.18, 64.18) * mm});
            skLineSegment(sketch, "E1816", {"start": v(-2.18, 64.18) * mm, "end": v(-2.2, 64.18) * mm});
            skLineSegment(sketch, "E1817", {"start": v(-2.2, 64.18) * mm, "end": v(-2.21, 64.18) * mm});
            skLineSegment(sketch, "E1818", {"start": v(-2.21, 64.18) * mm, "end": v(-2.26, 64.17) * mm});
            skLineSegment(sketch, "E1819", {"start": v(-2.26, 64.17) * mm, "end": v(-2.28, 64.16) * mm});
            skLineSegment(sketch, "E1820", {"start": v(-2.28, 64.16) * mm, "end": v(-2.3, 64.14) * mm});
            skLineSegment(sketch, "E1821", {"start": v(-2.3, 64.14) * mm, "end": v(-2.33, 64.11) * mm});
            skLineSegment(sketch, "E1822", {"start": v(-2.33, 64.11) * mm, "end": v(-2.35, 64.08) * mm});
            skLineSegment(sketch, "E1823", {"start": v(-2.35, 64.08) * mm, "end": v(-2.36, 64.05) * mm});
            skLineSegment(sketch, "E1824", {"start": v(-2.36, 64.05) * mm, "end": v(-2.36, 64) * mm});
            skLineSegment(sketch, "E1825", {"start": v(-2.36, 64) * mm, "end": v(-2.35, 63.97) * mm});
            skLineSegment(sketch, "E1826", {"start": v(-2.35, 63.97) * mm, "end": v(-2.34, 63.92) * mm});
            skLineSegment(sketch, "E1827", {"start": v(-2.34, 63.92) * mm, "end": v(-2.32, 63.9) * mm});
            skLineSegment(sketch, "E1828", {"start": v(-2.32, 63.9) * mm, "end": v(-2.28, 63.81) * mm});
            skLineSegment(sketch, "E1829", {"start": v(-2.28, 63.81) * mm, "end": v(-2.23, 63.71) * mm});
            skLineSegment(sketch, "E1830", {"start": v(-2.23, 63.71) * mm, "end": v(-2.2, 63.62) * mm});
            skLineSegment(sketch, "E1831", {"start": v(-2.2, 63.62) * mm, "end": v(-2.18, 63.54) * mm});
            skLineSegment(sketch, "E1832", {"start": v(-2.18, 63.54) * mm, "end": v(-2.17, 63.45) * mm});
            skLineSegment(sketch, "E1833", {"start": v(-2.17, 63.45) * mm, "end": v(-2.17, 63.4) * mm});
            skLineSegment(sketch, "E1834", {"start": v(-2.17, 63.4) * mm, "end": v(-2.18, 63.34) * mm});
            skLineSegment(sketch, "E1835", {"start": v(-2.18, 63.34) * mm, "end": v(-2.2, 63.3) * mm});
            skLineSegment(sketch, "E1836", {"start": v(-2.2, 63.3) * mm, "end": v(-2.21, 63.25) * mm});
            skLineSegment(sketch, "E1837", {"start": v(-2.21, 63.25) * mm, "end": v(-2.23, 63.2) * mm});
            skLineSegment(sketch, "E1838", {"start": v(-2.23, 63.2) * mm, "end": v(-1.98, 62.95) * mm});
            skLineSegment(sketch, "E1839", {"start": v(-1.98, 62.95) * mm, "end": v(-1.97, 62.96) * mm});
            skLineSegment(sketch, "E1840", {"start": v(-1.97, 62.96) * mm, "end": v(-1.92, 62.98) * mm});
            skLineSegment(sketch, "E1841", {"start": v(-1.92, 62.98) * mm, "end": v(-1.88, 63) * mm});
            skLineSegment(sketch, "E1842", {"start": v(-1.88, 63) * mm, "end": v(-1.84, 63) * mm});
            skLineSegment(sketch, "E1843", {"start": v(-1.84, 63) * mm, "end": v(-1.8, 63.01) * mm});
            skLineSegment(sketch, "E1844", {"start": v(-1.8, 63.01) * mm, "end": v(-1.74, 63.02) * mm});
            skLineSegment(sketch, "E1845", {"start": v(-1.74, 63.02) * mm, "end": v(-1.7, 63.01) * mm});
            skLineSegment(sketch, "E1846", {"start": v(-1.7, 63.01) * mm, "end": v(-1.64, 63) * mm});
            skLineSegment(sketch, "E1847", {"start": v(-1.64, 63) * mm, "end": v(-1.6, 63) * mm});
            skLineSegment(sketch, "E1848", {"start": v(-1.6, 63) * mm, "end": v(-1.54, 62.98) * mm});
            skLineSegment(sketch, "E1849", {"start": v(-1.54, 62.98) * mm, "end": v(-1.44, 62.94) * mm});
            skLineSegment(sketch, "E1850", {"start": v(-1.44, 62.94) * mm, "end": v(-1.3, 62.87) * mm});
            skLineSegment(sketch, "E1851", {"start": v(-1.3, 62.87) * mm, "end": v(-1.25, 62.84) * mm});
            skLineSegment(sketch, "E1852", {"start": v(-1.25, 62.84) * mm, "end": v(-1.21, 62.83) * mm});
            skLineSegment(sketch, "E1853", {"start": v(-1.98, 62.97) * mm, "end": v(-1.98, 62.97) * mm});
            skLineSegment(sketch, "E1854", {"start": v(10.87, 63.7) * mm, "end": v(10.91, 63.7) * mm});
            skLineSegment(sketch, "E1855", {"start": v(10.91, 63.7) * mm, "end": v(10.96, 63.69) * mm});
            skLineSegment(sketch, "E1856", {"start": v(10.96, 63.69) * mm, "end": v(11, 63.69) * mm});
            skLineSegment(sketch, "E1857", {"start": v(11, 63.69) * mm, "end": v(11.05, 63.7) * mm});
            skLineSegment(sketch, "E1858", {"start": v(11.05, 63.7) * mm, "end": v(11.08, 63.71) * mm});
            skLineSegment(sketch, "E1859", {"start": v(11.08, 63.71) * mm, "end": v(11.12, 63.73) * mm});
            skLineSegment(sketch, "E1860", {"start": v(11.12, 63.73) * mm, "end": v(11.15, 63.76) * mm});
            skLineSegment(sketch, "E1861", {"start": v(11.15, 63.76) * mm, "end": v(11.18, 63.79) * mm});
            skLineSegment(sketch, "E1862", {"start": v(11.18, 63.79) * mm, "end": v(11.2, 63.82) * mm});
            skLineSegment(sketch, "E1863", {"start": v(11.2, 63.82) * mm, "end": v(11.23, 63.85) * mm});
            skLineSegment(sketch, "E1864", {"start": v(11.23, 63.85) * mm, "end": v(11.25, 63.88) * mm});
            skLineSegment(sketch, "E1865", {"start": v(11.25, 63.88) * mm, "end": v(11.26, 63.92) * mm});
            skLineSegment(sketch, "E1866", {"start": v(11.26, 63.92) * mm, "end": v(11.26, 63.95) * mm});
            skLineSegment(sketch, "E1867", {"start": v(11.26, 63.95) * mm, "end": v(11.26, 63.99) * mm});
            skLineSegment(sketch, "E1868", {"start": v(11.26, 63.99) * mm, "end": v(11.25, 64.06) * mm});
            skLineSegment(sketch, "E1869", {"start": v(11.25, 64.06) * mm, "end": v(11.24, 64.08) * mm});
            skLineSegment(sketch, "E1870", {"start": v(11.24, 64.08) * mm, "end": v(11.23, 64.1) * mm});
            skLineSegment(sketch, "E1871", {"start": v(11.23, 64.1) * mm, "end": v(11.23, 64.1) * mm});
            skLineSegment(sketch, "E1872", {"start": v(11.23, 64.1) * mm, "end": v(11.18, 64.18) * mm});
            skLineSegment(sketch, "E1873", {"start": v(11.18, 64.18) * mm, "end": v(9.2, 66.16) * mm});
            skLineSegment(sketch, "E1874", {"start": v(9.2, 66.16) * mm, "end": v(9.18, 66.17) * mm});
            skLineSegment(sketch, "E1875", {"start": v(9.18, 66.17) * mm, "end": v(9.16, 66.2) * mm});
            skLineSegment(sketch, "E1876", {"start": v(9.16, 66.2) * mm, "end": v(9.15, 66.2) * mm});
            skLineSegment(sketch, "E1877", {"start": v(9.15, 66.2) * mm, "end": v(9.15, 66.2) * mm});
            skLineSegment(sketch, "E1878", {"start": v(9.15, 66.2) * mm, "end": v(9.1, 66.23) * mm});
            skLineSegment(sketch, "E1879", {"start": v(9.1, 66.23) * mm, "end": v(9.07, 66.24) * mm});
            skLineSegment(sketch, "E1880", {"start": v(9.07, 66.24) * mm, "end": v(9.03, 66.25) * mm});
            skLineSegment(sketch, "E1881", {"start": v(9.03, 66.25) * mm, "end": v(9, 66.26) * mm});
            skLineSegment(sketch, "E1882", {"start": v(9, 66.26) * mm, "end": v(8.97, 66.26) * mm});
            skLineSegment(sketch, "E1883", {"start": v(8.97, 66.26) * mm, "end": v(8.94, 66.26) * mm});
            skLineSegment(sketch, "E1884", {"start": v(8.94, 66.26) * mm, "end": v(8.9, 66.25) * mm});
            skLineSegment(sketch, "E1885", {"start": v(8.9, 66.25) * mm, "end": v(8.88, 66.24) * mm});
            skLineSegment(sketch, "E1886", {"start": v(8.88, 66.24) * mm, "end": v(8.85, 66.22) * mm});
            skLineSegment(sketch, "E1887", {"start": v(8.85, 66.22) * mm, "end": v(8.8, 66.2) * mm});
            skLineSegment(sketch, "E1888", {"start": v(8.8, 66.2) * mm, "end": v(8.77, 66.16) * mm});
            skLineSegment(sketch, "E1889", {"start": v(8.77, 66.16) * mm, "end": v(8.74, 66.12) * mm});
            skLineSegment(sketch, "E1890", {"start": v(8.74, 66.12) * mm, "end": v(8.72, 66.08) * mm});
            skLineSegment(sketch, "E1891", {"start": v(8.72, 66.08) * mm, "end": v(8.7, 66.05) * mm});
            skLineSegment(sketch, "E1892", {"start": v(8.7, 66.05) * mm, "end": v(8.7, 66.03) * mm});
            skLineSegment(sketch, "E1893", {"start": v(8.7, 66.03) * mm, "end": v(8.7, 65.96) * mm});
            skLineSegment(sketch, "E1894", {"start": v(8.7, 65.96) * mm, "end": v(8.7, 65.9) * mm});
            skLineSegment(sketch, "E1895", {"start": v(8.7, 65.9) * mm, "end": v(8.7, 65.85) * mm});
            skLineSegment(sketch, "E1896", {"start": v(8.7, 65.85) * mm, "end": v(8.75, 65.74) * mm});
            skLineSegment(sketch, "E1897", {"start": v(8.75, 65.74) * mm, "end": v(8.8, 65.64) * mm});
            skLineSegment(sketch, "E1898", {"start": v(8.8, 65.64) * mm, "end": v(8.83, 65.61) * mm});
            skLineSegment(sketch, "E1899", {"start": v(8.83, 65.61) * mm, "end": v(8.86, 65.54) * mm});
            skLineSegment(sketch, "E1900", {"start": v(8.86, 65.54) * mm, "end": v(8.9, 65.45) * mm});
            skLineSegment(sketch, "E1901", {"start": v(8.9, 65.45) * mm, "end": v(8.95, 65.37) * mm});
            skLineSegment(sketch, "E1902", {"start": v(8.95, 65.37) * mm, "end": v(8.98, 65.28) * mm});
            skLineSegment(sketch, "E1903", {"start": v(8.98, 65.28) * mm, "end": v(9, 65.2) * mm});
            skLineSegment(sketch, "E1904", {"start": v(9, 65.2) * mm, "end": v(9.03, 65.11) * mm});
            skLineSegment(sketch, "E1905", {"start": v(9.03, 65.11) * mm, "end": v(9.05, 65.03) * mm});
            skLineSegment(sketch, "E1906", {"start": v(9.05, 65.03) * mm, "end": v(9.06, 64.95) * mm});
            skLineSegment(sketch, "E1907", {"start": v(9.06, 64.95) * mm, "end": v(9.06, 64.87) * mm});
            skLineSegment(sketch, "E1908", {"start": v(9.06, 64.87) * mm, "end": v(9.06, 64.8) * mm});
            skLineSegment(sketch, "E1909", {"start": v(9.06, 64.8) * mm, "end": v(9.05, 64.71) * mm});
            skLineSegment(sketch, "E1910", {"start": v(9.05, 64.71) * mm, "end": v(9.03, 64.63) * mm});
            skLineSegment(sketch, "E1911", {"start": v(9.03, 64.63) * mm, "end": v(9, 64.56) * mm});
            skLineSegment(sketch, "E1912", {"start": v(9, 64.56) * mm, "end": v(8.99, 64.51) * mm});
            skLineSegment(sketch, "E1913", {"start": v(8.99, 64.51) * mm, "end": v(9, 64.5) * mm});
            skLineSegment(sketch, "E1914", {"start": v(9, 64.5) * mm, "end": v(9, 64.5) * mm});
            skLineSegment(sketch, "E1915", {"start": v(9, 64.5) * mm, "end": v(8.99, 64.5) * mm});
            skLineSegment(sketch, "E1916", {"start": v(8.99, 64.5) * mm, "end": v(8.98, 64.5) * mm});
            skLineSegment(sketch, "E1917", {"start": v(8.98, 64.5) * mm, "end": v(8.94, 64.42) * mm});
            skLineSegment(sketch, "E1918", {"start": v(8.94, 64.42) * mm, "end": v(9.42, 63.93) * mm});
            skLineSegment(sketch, "E1919", {"start": v(9.42, 63.93) * mm, "end": v(9.47, 63.96) * mm});
            skLineSegment(sketch, "E1920", {"start": v(9.47, 63.96) * mm, "end": v(9.53, 63.98) * mm});
            skLineSegment(sketch, "E1921", {"start": v(9.53, 63.98) * mm, "end": v(9.58, 64) * mm});
            skLineSegment(sketch, "E1922", {"start": v(9.58, 64) * mm, "end": v(9.64, 64.02) * mm});
            skLineSegment(sketch, "E1923", {"start": v(9.64, 64.02) * mm, "end": v(9.7, 64.04) * mm});
            skLineSegment(sketch, "E1924", {"start": v(9.7, 64.04) * mm, "end": v(9.77, 64.05) * mm});
            skLineSegment(sketch, "E1925", {"start": v(9.77, 64.05) * mm, "end": v(9.88, 64.05) * mm});
            skLineSegment(sketch, "E1926", {"start": v(9.88, 64.05) * mm, "end": v(9.99, 64.05) * mm});
            skLineSegment(sketch, "E1927", {"start": v(9.99, 64.05) * mm, "end": v(10.04, 64.04) * mm});
            skLineSegment(sketch, "E1928", {"start": v(10.04, 64.04) * mm, "end": v(10.12, 64.02) * mm});
            skLineSegment(sketch, "E1929", {"start": v(10.12, 64.02) * mm, "end": v(10.2, 64) * mm});
            skLineSegment(sketch, "E1930", {"start": v(10.2, 64) * mm, "end": v(10.28, 63.98) * mm});
            skLineSegment(sketch, "E1931", {"start": v(10.28, 63.98) * mm, "end": v(10.35, 63.95) * mm});
            skLineSegment(sketch, "E1932", {"start": v(10.35, 63.95) * mm, "end": v(10.5, 63.88) * mm});
            skLineSegment(sketch, "E1933", {"start": v(10.5, 63.88) * mm, "end": v(10.58, 63.84) * mm});
            skLineSegment(sketch, "E1934", {"start": v(10.58, 63.84) * mm, "end": v(10.63, 63.8) * mm});
            skLineSegment(sketch, "E1935", {"start": v(10.63, 63.8) * mm, "end": v(10.65, 63.8) * mm});
            skLineSegment(sketch, "E1936", {"start": v(10.65, 63.8) * mm, "end": v(10.7, 63.77) * mm});
            skLineSegment(sketch, "E1937", {"start": v(10.7, 63.77) * mm, "end": v(10.79, 63.73) * mm});
            skLineSegment(sketch, "E1938", {"start": v(10.79, 63.73) * mm, "end": v(10.87, 63.7) * mm});
            skLineSegment(sketch, "E1939", {"start": v(-3.62, 64.6) * mm, "end": v(-3.39, 64.36) * mm});
            skLineSegment(sketch, "E1940", {"start": v(-3.39, 64.36) * mm, "end": v(-3.38, 64.36) * mm});
            skLineSegment(sketch, "E1941", {"start": v(-3.38, 64.36) * mm, "end": v(-3.32, 64.4) * mm});
            skLineSegment(sketch, "E1942", {"start": v(-3.32, 64.4) * mm, "end": v(-3.25, 64.44) * mm});
            skLineSegment(sketch, "E1943", {"start": v(-3.25, 64.44) * mm, "end": v(-3.17, 64.49) * mm});
            skLineSegment(sketch, "E1944", {"start": v(-3.17, 64.49) * mm, "end": v(-3.08, 64.53) * mm});
            skLineSegment(sketch, "E1945", {"start": v(-3.08, 64.53) * mm, "end": v(-3.04, 64.55) * mm});
            skLineSegment(sketch, "E1946", {"start": v(-3.04, 64.55) * mm, "end": v(-2.93, 64.58) * mm});
            skLineSegment(sketch, "E1947", {"start": v(-2.93, 64.58) * mm, "end": v(-2.82, 64.6) * mm});
            skLineSegment(sketch, "E1948", {"start": v(-2.82, 64.6) * mm, "end": v(-2.7, 64.6) * mm});
            skLineSegment(sketch, "E1949", {"start": v(-2.7, 64.6) * mm, "end": v(-2.6, 64.6) * mm});
            skLineSegment(sketch, "E1950", {"start": v(-2.6, 64.6) * mm, "end": v(-2.49, 64.58) * mm});
            skLineSegment(sketch, "E1951", {"start": v(-2.49, 64.58) * mm, "end": v(-2.38, 64.56) * mm});
            skLineSegment(sketch, "E1952", {"start": v(-2.38, 64.56) * mm, "end": v(-2.26, 64.52) * mm});
            skLineSegment(sketch, "E1953", {"start": v(-2.26, 64.52) * mm, "end": v(-2.14, 64.46) * mm});
            skLineSegment(sketch, "E1954", {"start": v(-2.14, 64.46) * mm, "end": v(-2.03, 64.42) * mm});
            skLineSegment(sketch, "E1955", {"start": v(-2.03, 64.42) * mm, "end": v(-2, 64.41) * mm});
            skLineSegment(sketch, "E1956", {"start": v(-2, 64.41) * mm, "end": v(-1.97, 64.4) * mm});
            skLineSegment(sketch, "E1957", {"start": v(-1.97, 64.4) * mm, "end": v(-1.94, 64.42) * mm});
            skLineSegment(sketch, "E1958", {"start": v(-1.94, 64.42) * mm, "end": v(-1.9, 64.43) * mm});
            skLineSegment(sketch, "E1959", {"start": v(-1.9, 64.43) * mm, "end": v(-1.87, 64.47) * mm});
            skLineSegment(sketch, "E1960", {"start": v(-1.87, 64.47) * mm, "end": v(-1.84, 64.5) * mm});
            skLineSegment(sketch, "E1961", {"start": v(-1.84, 64.5) * mm, "end": v(-1.82, 64.55) * mm});
            skLineSegment(sketch, "E1962", {"start": v(-1.82, 64.55) * mm, "end": v(-1.81, 64.6) * mm});
            skLineSegment(sketch, "E1963", {"start": v(-1.81, 64.6) * mm, "end": v(-1.82, 64.63) * mm});
            skLineSegment(sketch, "E1964", {"start": v(-1.82, 64.63) * mm, "end": v(-1.83, 64.66) * mm});
            skLineSegment(sketch, "E1965", {"start": v(-1.83, 64.66) * mm, "end": v(-2.7, 65.52) * mm});
            skLineSegment(sketch, "E1966", {"start": v(-2.7, 65.52) * mm, "end": v(-3.62, 64.6) * mm});
            skLineSegment(sketch, "E1967", {"start": v(-2.02, 60.14) * mm, "end": v(-2, 60.13) * mm});
            skLineSegment(sketch, "E1968", {"start": v(-2, 60.13) * mm, "end": v(-1.97, 60.13) * mm});
            skLineSegment(sketch, "E1969", {"start": v(-1.97, 60.13) * mm, "end": v(-1.93, 60.13) * mm});
            skLineSegment(sketch, "E1970", {"start": v(-1.93, 60.13) * mm, "end": v(-1.9, 60.14) * mm});
            skLineSegment(sketch, "E1971", {"start": v(-1.9, 60.14) * mm, "end": v(-1.85, 60.16) * mm});
            skLineSegment(sketch, "E1972", {"start": v(-1.85, 60.16) * mm, "end": v(-1.81, 60.19) * mm});
            skLineSegment(sketch, "E1973", {"start": v(-1.81, 60.19) * mm, "end": v(-1.79, 60.21) * mm});
            skLineSegment(sketch, "E1974", {"start": v(-1.79, 60.21) * mm, "end": v(-0.71, 61.3) * mm});
            skLineSegment(sketch, "E1975", {"start": v(-0.71, 61.3) * mm, "end": v(-0.7, 61.3) * mm});
            skLineSegment(sketch, "E1976", {"start": v(-0.7, 61.3) * mm, "end": v(-3.8, 64.4) * mm});
            skLineSegment(sketch, "E1977", {"start": v(-3.8, 64.4) * mm, "end": v(-3.82, 64.4) * mm});
            skLineSegment(sketch, "E1978", {"start": v(-3.82, 64.4) * mm, "end": v(-4.94, 63.28) * mm});
            skLineSegment(sketch, "E1979", {"start": v(-4.94, 63.28) * mm, "end": v(-4.96, 63.24) * mm});
            skLineSegment(sketch, "E1980", {"start": v(-4.96, 63.24) * mm, "end": v(-4.98, 63.19) * mm});
            skLineSegment(sketch, "E1981", {"start": v(-4.98, 63.19) * mm, "end": v(-4.99, 63.14) * mm});
            skLineSegment(sketch, "E1982", {"start": v(-4.99, 63.14) * mm, "end": v(-4.98, 63.12) * mm});
            skLineSegment(sketch, "E1983", {"start": v(-4.98, 63.12) * mm, "end": v(-4.98, 63.1) * mm});
            skLineSegment(sketch, "E1984", {"start": v(-4.98, 63.1) * mm, "end": v(-4.95, 63.05) * mm});
            skLineSegment(sketch, "E1985", {"start": v(-4.95, 63.05) * mm, "end": v(-4.92, 63.02) * mm});
            skLineSegment(sketch, "E1986", {"start": v(-4.92, 63.02) * mm, "end": v(-4.88, 63) * mm});
            skLineSegment(sketch, "E1987", {"start": v(-4.88, 63) * mm, "end": v(-4.84, 62.99) * mm});
            skLineSegment(sketch, "E1988", {"start": v(-4.84, 62.99) * mm, "end": v(-4.8, 62.99) * mm});
            skLineSegment(sketch, "E1989", {"start": v(-4.8, 62.99) * mm, "end": v(-4.76, 63) * mm});
            skLineSegment(sketch, "E1990", {"start": v(-4.76, 63) * mm, "end": v(-4.71, 63.02) * mm});
            skLineSegment(sketch, "E1991", {"start": v(-4.71, 63.02) * mm, "end": v(-4.63, 63.06) * mm});
            skLineSegment(sketch, "E1992", {"start": v(-4.63, 63.06) * mm, "end": v(-4.6, 63.06) * mm});
            skLineSegment(sketch, "E1993", {"start": v(-4.6, 63.06) * mm, "end": v(-4.57, 63.07) * mm});
            skLineSegment(sketch, "E1994", {"start": v(-4.57, 63.07) * mm, "end": v(-4.54, 63.06) * mm});
            skLineSegment(sketch, "E1995", {"start": v(-4.54, 63.06) * mm, "end": v(-4.51, 63.05) * mm});
            skLineSegment(sketch, "E1996", {"start": v(-4.51, 63.05) * mm, "end": v(-4.49, 63.04) * mm});
            skLineSegment(sketch, "E1997", {"start": v(-4.49, 63.04) * mm, "end": v(-4.46, 63.02) * mm});
            skLineSegment(sketch, "E1998", {"start": v(-4.46, 63.02) * mm, "end": v(-4.44, 63) * mm});
            skLineSegment(sketch, "E1999", {"start": v(-4.44, 63) * mm, "end": v(-2.08, 60.64) * mm});
            skLineSegment(sketch, "E2000", {"start": v(-2.08, 60.64) * mm, "end": v(-2.07, 60.62) * mm});
            skLineSegment(sketch, "E2001", {"start": v(-2.07, 60.62) * mm, "end": v(-2.06, 60.6) * mm});
            skLineSegment(sketch, "E2002", {"start": v(-2.06, 60.6) * mm, "end": v(-2.05, 60.57) * mm});
            skLineSegment(sketch, "E2003", {"start": v(-2.05, 60.57) * mm, "end": v(-2.04, 60.54) * mm});
            skLineSegment(sketch, "E2004", {"start": v(-2.04, 60.54) * mm, "end": v(-2.05, 60.5) * mm});
            skLineSegment(sketch, "E2005", {"start": v(-2.05, 60.5) * mm, "end": v(-2.07, 60.46) * mm});
            skLineSegment(sketch, "E2006", {"start": v(-2.07, 60.46) * mm, "end": v(-2.1, 60.4) * mm});
            skLineSegment(sketch, "E2007", {"start": v(-2.1, 60.4) * mm, "end": v(-2.12, 60.34) * mm});
            skLineSegment(sketch, "E2008", {"start": v(-2.12, 60.34) * mm, "end": v(-2.12, 60.28) * mm});
            skLineSegment(sketch, "E2009", {"start": v(-2.12, 60.28) * mm, "end": v(-2.12, 60.24) * mm});
            skLineSegment(sketch, "E2010", {"start": v(-2.12, 60.24) * mm, "end": v(-2.1, 60.2) * mm});
            skLineSegment(sketch, "E2011", {"start": v(-2.1, 60.2) * mm, "end": v(-2.09, 60.18) * mm});
            skLineSegment(sketch, "E2012", {"start": v(-2.09, 60.18) * mm, "end": v(-2.07, 60.16) * mm});
            skLineSegment(sketch, "E2013", {"start": v(-2.07, 60.16) * mm, "end": v(-2.05, 60.15) * mm});
            skLineSegment(sketch, "E2014", {"start": v(-2.05, 60.15) * mm, "end": v(-2.02, 60.14) * mm});
            skLineSegment(sketch, "E2015", {"start": v(4.9, 54.38) * mm, "end": v(5.23, 54.21) * mm});
            skLineSegment(sketch, "E2016", {"start": v(5.23, 54.21) * mm, "end": v(5.25, 54.21) * mm});
            skLineSegment(sketch, "E2017", {"start": v(5.25, 54.21) * mm, "end": v(5.47, 54.44) * mm});
            skLineSegment(sketch, "E2018", {"start": v(5.47, 54.44) * mm, "end": v(5.39, 54.58) * mm});
            skLineSegment(sketch, "E2019", {"start": v(5.39, 54.58) * mm, "end": v(5.22, 54.89) * mm});
            skLineSegment(sketch, "E2020", {"start": v(5.22, 54.89) * mm, "end": v(5.2, 54.93) * mm});
            skLineSegment(sketch, "E2021", {"start": v(5.2, 54.93) * mm, "end": v(5.16, 55) * mm});
            skLineSegment(sketch, "E2022", {"start": v(5.16, 55) * mm, "end": v(5.15, 55.02) * mm});
            skLineSegment(sketch, "E2023", {"start": v(5.15, 55.02) * mm, "end": v(5.14, 55.03) * mm});
            skLineSegment(sketch, "E2024", {"start": v(5.14, 55.03) * mm, "end": v(5.14, 55.03) * mm});
            skLineSegment(sketch, "E2025", {"start": v(5.14, 55.03) * mm, "end": v(5.14, 55.04) * mm});
            skLineSegment(sketch, "E2026", {"start": v(5.14, 55.04) * mm, "end": v(5.14, 55.04) * mm});
            skLineSegment(sketch, "E2027", {"start": v(5.14, 55.04) * mm, "end": v(5.14, 55.05) * mm});
            skLineSegment(sketch, "E2028", {"start": v(5.14, 55.05) * mm, "end": v(5.13, 55.06) * mm});
            skLineSegment(sketch, "E2029", {"start": v(5.13, 55.06) * mm, "end": v(5.07, 55.17) * mm});
            skLineSegment(sketch, "E2030", {"start": v(5.07, 55.17) * mm, "end": v(5.07, 55.18) * mm});
            skLineSegment(sketch, "E2031", {"start": v(5.07, 55.18) * mm, "end": v(5, 55.3) * mm});
            skLineSegment(sketch, "E2032", {"start": v(5, 55.3) * mm, "end": v(5, 55.31) * mm});
            skLineSegment(sketch, "E2033", {"start": v(5, 55.31) * mm, "end": v(4.97, 55.36) * mm});
            skLineSegment(sketch, "E2034", {"start": v(4.97, 55.36) * mm, "end": v(4.92, 55.46) * mm});
            skLineSegment(sketch, "E2035", {"start": v(4.92, 55.46) * mm, "end": v(4.9, 55.5) * mm});
            skLineSegment(sketch, "E2036", {"start": v(4.9, 55.5) * mm, "end": v(4.89, 55.5) * mm});
            skLineSegment(sketch, "E2037", {"start": v(4.89, 55.5) * mm, "end": v(4.88, 55.52) * mm});
            skLineSegment(sketch, "E2038", {"start": v(4.88, 55.52) * mm, "end": v(4.87, 55.54) * mm});
            skLineSegment(sketch, "E2039", {"start": v(4.87, 55.54) * mm, "end": v(4.86, 55.56) * mm});
            skLineSegment(sketch, "E2040", {"start": v(4.86, 55.56) * mm, "end": v(4.68, 55.89) * mm});
            skLineSegment(sketch, "E2041", {"start": v(4.68, 55.89) * mm, "end": v(4.65, 55.95) * mm});
            skLineSegment(sketch, "E2042", {"start": v(4.65, 55.95) * mm, "end": v(4.54, 56.16) * mm});
            skLineSegment(sketch, "E2043", {"start": v(4.54, 56.16) * mm, "end": v(4.5, 56.22) * mm});
            skLineSegment(sketch, "E2044", {"start": v(4.5, 56.22) * mm, "end": v(4.4, 56.42) * mm});
            skLineSegment(sketch, "E2045", {"start": v(4.4, 56.42) * mm, "end": v(4.35, 56.5) * mm});
            skLineSegment(sketch, "E2046", {"start": v(4.35, 56.5) * mm, "end": v(4.17, 56.84) * mm});
            skLineSegment(sketch, "E2047", {"start": v(4.17, 56.84) * mm, "end": v(4.13, 56.9) * mm});
            skLineSegment(sketch, "E2048", {"start": v(4.13, 56.9) * mm, "end": v(4.05, 57.06) * mm});
            skLineSegment(sketch, "E2049", {"start": v(4.05, 57.06) * mm, "end": v(4, 57.16) * mm});
            skLineSegment(sketch, "E2050", {"start": v(4, 57.16) * mm, "end": v(3.76, 57.59) * mm});
            skLineSegment(sketch, "E2051", {"start": v(3.76, 57.59) * mm, "end": v(3.73, 57.65) * mm});
            skLineSegment(sketch, "E2052", {"start": v(3.73, 57.65) * mm, "end": v(3.64, 57.8) * mm});
            skLineSegment(sketch, "E2053", {"start": v(3.64, 57.8) * mm, "end": v(3.6, 57.9) * mm});
            skLineSegment(sketch, "E2054", {"start": v(3.6, 57.9) * mm, "end": v(3.57, 57.94) * mm});
            skLineSegment(sketch, "E2055", {"start": v(3.57, 57.94) * mm, "end": v(3.52, 58.03) * mm});
            skLineSegment(sketch, "E2056", {"start": v(3.52, 58.03) * mm, "end": v(3.47, 58.13) * mm});
            skLineSegment(sketch, "E2057", {"start": v(3.47, 58.13) * mm, "end": v(3.37, 58.31) * mm});
            skLineSegment(sketch, "E2058", {"start": v(3.37, 58.31) * mm, "end": v(3.35, 58.36) * mm});
            skLineSegment(sketch, "E2059", {"start": v(3.35, 58.36) * mm, "end": v(3.35, 58.35) * mm});
            skLineSegment(sketch, "E2060", {"start": v(3.35, 58.35) * mm, "end": v(3.35, 58.35) * mm});
            skLineSegment(sketch, "E2061", {"start": v(3.35, 58.35) * mm, "end": v(3.35, 58.36) * mm});
            skLineSegment(sketch, "E2062", {"start": v(3.35, 58.36) * mm, "end": v(3.33, 58.4) * mm});
            skLineSegment(sketch, "E2063", {"start": v(3.33, 58.4) * mm, "end": v(3.27, 58.5) * mm});
            skLineSegment(sketch, "E2064", {"start": v(3.27, 58.5) * mm, "end": v(3.24, 58.56) * mm});
            skLineSegment(sketch, "E2065", {"start": v(3.24, 58.56) * mm, "end": v(3.23, 58.57) * mm});
            skLineSegment(sketch, "E2066", {"start": v(3.23, 58.57) * mm, "end": v(3.2, 58.63) * mm});
            skLineSegment(sketch, "E2067", {"start": v(3.2, 58.63) * mm, "end": v(3.15, 58.73) * mm});
            skLineSegment(sketch, "E2068", {"start": v(3.15, 58.73) * mm, "end": v(3.13, 58.77) * mm});
            skLineSegment(sketch, "E2069", {"start": v(3.13, 58.77) * mm, "end": v(3.13, 58.76) * mm});
            skLineSegment(sketch, "E2070", {"start": v(3.13, 58.76) * mm, "end": v(3.12, 58.77) * mm});
            skLineSegment(sketch, "E2071", {"start": v(3.12, 58.77) * mm, "end": v(3.1, 58.82) * mm});
            skLineSegment(sketch, "E2072", {"start": v(3.1, 58.82) * mm, "end": v(3.07, 58.86) * mm});
            skLineSegment(sketch, "E2073", {"start": v(3.07, 58.86) * mm, "end": v(2.96, 59.08) * mm});
            skLineSegment(sketch, "E2074", {"start": v(2.96, 59.08) * mm, "end": v(2.93, 59.13) * mm});
            skLineSegment(sketch, "E2075", {"start": v(2.93, 59.13) * mm, "end": v(2.82, 59.33) * mm});
            skLineSegment(sketch, "E2076", {"start": v(2.82, 59.33) * mm, "end": v(2.63, 59.68) * mm});
            skLineSegment(sketch, "E2077", {"start": v(2.63, 59.68) * mm, "end": v(2.6, 59.75) * mm});
            skLineSegment(sketch, "E2078", {"start": v(2.6, 59.75) * mm, "end": v(2.5, 59.94) * mm});
            skLineSegment(sketch, "E2079", {"start": v(2.5, 59.94) * mm, "end": v(2.45, 60) * mm});
            skLineSegment(sketch, "E2080", {"start": v(2.45, 60) * mm, "end": v(2.3, 60.29) * mm});
            skLineSegment(sketch, "E2081", {"start": v(2.3, 60.29) * mm, "end": v(2.3, 60.3) * mm});
            skLineSegment(sketch, "E2082", {"start": v(2.3, 60.3) * mm, "end": v(2.3, 60.3) * mm});
            skLineSegment(sketch, "E2083", {"start": v(2.3, 60.3) * mm, "end": v(2.3, 60.31) * mm});
            skLineSegment(sketch, "E2084", {"start": v(2.3, 60.31) * mm, "end": v(6.1, 56.5) * mm});
            skLineSegment(sketch, "E2085", {"start": v(6.1, 56.5) * mm, "end": v(6.12, 56.48) * mm});
            skLineSegment(sketch, "E2086", {"start": v(6.12, 56.48) * mm, "end": v(6.14, 56.46) * mm});
            skLineSegment(sketch, "E2087", {"start": v(6.14, 56.46) * mm, "end": v(6.15, 56.45) * mm});
            skLineSegment(sketch, "E2088", {"start": v(6.15, 56.45) * mm, "end": v(6.17, 56.42) * mm});
            skLineSegment(sketch, "E2089", {"start": v(6.17, 56.42) * mm, "end": v(6.19, 56.39) * mm});
            skLineSegment(sketch, "E2090", {"start": v(6.19, 56.39) * mm, "end": v(6.2, 56.36) * mm});
            skLineSegment(sketch, "E2091", {"start": v(6.2, 56.36) * mm, "end": v(6.2, 56.33) * mm});
            skLineSegment(sketch, "E2092", {"start": v(6.2, 56.33) * mm, "end": v(6.2, 56.3) * mm});
            skLineSegment(sketch, "E2093", {"start": v(6.2, 56.3) * mm, "end": v(6.2, 56.25) * mm});
            skLineSegment(sketch, "E2094", {"start": v(6.2, 56.25) * mm, "end": v(6.2, 56.21) * mm});
            skLineSegment(sketch, "E2095", {"start": v(6.2, 56.21) * mm, "end": v(6.19, 56.17) * mm});
            skLineSegment(sketch, "E2096", {"start": v(6.19, 56.17) * mm, "end": v(6.17, 56.13) * mm});
            skLineSegment(sketch, "E2097", {"start": v(6.17, 56.13) * mm, "end": v(6.16, 56.1) * mm});
            skLineSegment(sketch, "E2098", {"start": v(6.16, 56.1) * mm, "end": v(6.07, 55.92) * mm});
            skLineSegment(sketch, "E2099", {"start": v(6.07, 55.92) * mm, "end": v(6.06, 55.88) * mm});
            skLineSegment(sketch, "E2100", {"start": v(6.06, 55.88) * mm, "end": v(6.06, 55.84) * mm});
            skLineSegment(sketch, "E2101", {"start": v(6.06, 55.84) * mm, "end": v(6.05, 55.8) * mm});
            skLineSegment(sketch, "E2102", {"start": v(6.05, 55.8) * mm, "end": v(6.05, 55.76) * mm});
            skLineSegment(sketch, "E2103", {"start": v(6.05, 55.76) * mm, "end": v(6.06, 55.72) * mm});
            skLineSegment(sketch, "E2104", {"start": v(6.06, 55.72) * mm, "end": v(6.07, 55.69) * mm});
            skLineSegment(sketch, "E2105", {"start": v(6.07, 55.69) * mm, "end": v(6.09, 55.66) * mm});
            skLineSegment(sketch, "E2106", {"start": v(6.09, 55.66) * mm, "end": v(6.1, 55.63) * mm});
            skLineSegment(sketch, "E2107", {"start": v(6.1, 55.63) * mm, "end": v(6.13, 55.6) * mm});
            skLineSegment(sketch, "E2108", {"start": v(6.13, 55.6) * mm, "end": v(6.16, 55.57) * mm});
            skLineSegment(sketch, "E2109", {"start": v(6.16, 55.57) * mm, "end": v(6.19, 55.55) * mm});
            skLineSegment(sketch, "E2110", {"start": v(6.19, 55.55) * mm, "end": v(6.22, 55.53) * mm});
            skLineSegment(sketch, "E2111", {"start": v(6.22, 55.53) * mm, "end": v(6.26, 55.51) * mm});
            skLineSegment(sketch, "E2112", {"start": v(6.26, 55.51) * mm, "end": v(6.3, 55.5) * mm});
            skLineSegment(sketch, "E2113", {"start": v(6.3, 55.5) * mm, "end": v(6.36, 55.5) * mm});
            skLineSegment(sketch, "E2114", {"start": v(6.36, 55.5) * mm, "end": v(6.42, 55.5) * mm});
            skLineSegment(sketch, "E2115", {"start": v(6.42, 55.5) * mm, "end": v(6.46, 55.51) * mm});
            skLineSegment(sketch, "E2116", {"start": v(6.46, 55.51) * mm, "end": v(6.51, 55.53) * mm});
            skLineSegment(sketch, "E2117", {"start": v(6.51, 55.53) * mm, "end": v(6.56, 55.56) * mm});
            skLineSegment(sketch, "E2118", {"start": v(6.56, 55.56) * mm, "end": v(6.61, 55.6) * mm});
            skLineSegment(sketch, "E2119", {"start": v(6.61, 55.6) * mm, "end": v(6.65, 55.62) * mm});
            skLineSegment(sketch, "E2120", {"start": v(6.65, 55.62) * mm, "end": v(6.67, 55.64) * mm});
            skLineSegment(sketch, "E2121", {"start": v(6.67, 55.64) * mm, "end": v(8.91, 57.88) * mm});
            skLineSegment(sketch, "E2122", {"start": v(8.91, 57.88) * mm, "end": v(8.93, 57.9) * mm});
            skLineSegment(sketch, "E2123", {"start": v(8.93, 57.9) * mm, "end": v(8.96, 57.95) * mm});
            skLineSegment(sketch, "E2124", {"start": v(8.96, 57.95) * mm, "end": v(8.98, 57.98) * mm});
            skLineSegment(sketch, "E2125", {"start": v(8.98, 57.98) * mm, "end": v(8.98, 57.98) * mm});
            skLineSegment(sketch, "E2126", {"start": v(8.98, 57.98) * mm, "end": v(8.99, 58) * mm});
            skLineSegment(sketch, "E2127", {"start": v(8.99, 58) * mm, "end": v(9.01, 58.04) * mm});
            skLineSegment(sketch, "E2128", {"start": v(9.01, 58.04) * mm, "end": v(9.03, 58.11) * mm});
            skLineSegment(sketch, "E2129", {"start": v(9.03, 58.11) * mm, "end": v(9.04, 58.15) * mm});
            skLineSegment(sketch, "E2130", {"start": v(9.04, 58.15) * mm, "end": v(9.04, 58.18) * mm});
            skLineSegment(sketch, "E2131", {"start": v(9.04, 58.18) * mm, "end": v(9.04, 58.21) * mm});
            skLineSegment(sketch, "E2132", {"start": v(9.04, 58.21) * mm, "end": v(9.03, 58.24) * mm});
            skLineSegment(sketch, "E2133", {"start": v(9.03, 58.24) * mm, "end": v(9.02, 58.27) * mm});
            skLineSegment(sketch, "E2134", {"start": v(9.02, 58.27) * mm, "end": v(9, 58.3) * mm});
            skLineSegment(sketch, "E2135", {"start": v(9, 58.3) * mm, "end": v(9, 58.33) * mm});
            skLineSegment(sketch, "E2136", {"start": v(9, 58.33) * mm, "end": v(8.97, 58.36) * mm});
            skLineSegment(sketch, "E2137", {"start": v(8.97, 58.36) * mm, "end": v(8.92, 58.41) * mm});
            skLineSegment(sketch, "E2138", {"start": v(8.92, 58.41) * mm, "end": v(8.87, 58.45) * mm});
            skLineSegment(sketch, "E2139", {"start": v(8.87, 58.45) * mm, "end": v(8.84, 58.46) * mm});
            skLineSegment(sketch, "E2140", {"start": v(8.84, 58.46) * mm, "end": v(8.8, 58.47) * mm});
            skLineSegment(sketch, "E2141", {"start": v(8.8, 58.47) * mm, "end": v(8.78, 58.48) * mm});
            skLineSegment(sketch, "E2142", {"start": v(8.78, 58.48) * mm, "end": v(8.74, 58.48) * mm});
            skLineSegment(sketch, "E2143", {"start": v(8.74, 58.48) * mm, "end": v(8.7, 58.48) * mm});
            skLineSegment(sketch, "E2144", {"start": v(8.7, 58.48) * mm, "end": v(8.66, 58.47) * mm});
            skLineSegment(sketch, "E2145", {"start": v(8.66, 58.47) * mm, "end": v(8.62, 58.46) * mm});
            skLineSegment(sketch, "E2146", {"start": v(8.62, 58.46) * mm, "end": v(8.42, 58.36) * mm});
            skLineSegment(sketch, "E2147", {"start": v(8.42, 58.36) * mm, "end": v(8.37, 58.35) * mm});
            skLineSegment(sketch, "E2148", {"start": v(8.37, 58.35) * mm, "end": v(8.32, 58.33) * mm});
            skLineSegment(sketch, "E2149", {"start": v(8.32, 58.33) * mm, "end": v(8.27, 58.33) * mm});
            skLineSegment(sketch, "E2150", {"start": v(8.27, 58.33) * mm, "end": v(8.23, 58.33) * mm});
            skLineSegment(sketch, "E2151", {"start": v(8.23, 58.33) * mm, "end": v(8.2, 58.33) * mm});
            skLineSegment(sketch, "E2152", {"start": v(8.2, 58.33) * mm, "end": v(8.17, 58.34) * mm});
            skLineSegment(sketch, "E2153", {"start": v(8.17, 58.34) * mm, "end": v(8.14, 58.35) * mm});
            skLineSegment(sketch, "E2154", {"start": v(8.14, 58.35) * mm, "end": v(8.1, 58.37) * mm});
            skLineSegment(sketch, "E2155", {"start": v(8.1, 58.37) * mm, "end": v(8.1, 58.37) * mm});
            skLineSegment(sketch, "E2156", {"start": v(8.1, 58.37) * mm, "end": v(8.04, 58.42) * mm});
            skLineSegment(sketch, "E2157", {"start": v(8.04, 58.42) * mm, "end": v(8.04, 58.41) * mm});
            skLineSegment(sketch, "E2158", {"start": v(8.04, 58.41) * mm, "end": v(3.57, 62.88) * mm});
            skLineSegment(sketch, "E2159", {"start": v(3.57, 62.88) * mm, "end": v(3.54, 62.93) * mm});
            skLineSegment(sketch, "E2160", {"start": v(3.54, 62.93) * mm, "end": v(3.51, 62.97) * mm});
            skLineSegment(sketch, "E2161", {"start": v(3.51, 62.97) * mm, "end": v(3.5, 63) * mm});
            skLineSegment(sketch, "E2162", {"start": v(3.5, 63) * mm, "end": v(3.48, 63.05) * mm});
            skLineSegment(sketch, "E2163", {"start": v(3.48, 63.05) * mm, "end": v(3.47, 63.1) * mm});
            skLineSegment(sketch, "E2164", {"start": v(3.47, 63.1) * mm, "end": v(3.48, 63.16) * mm});
            skLineSegment(sketch, "E2165", {"start": v(3.48, 63.16) * mm, "end": v(3.5, 63.22) * mm});
            skLineSegment(sketch, "E2166", {"start": v(3.5, 63.22) * mm, "end": v(3.51, 63.28) * mm});
            skLineSegment(sketch, "E2167", {"start": v(3.51, 63.28) * mm, "end": v(3.6, 63.47) * mm});
            skLineSegment(sketch, "E2168", {"start": v(3.6, 63.47) * mm, "end": v(3.62, 63.5) * mm});
            skLineSegment(sketch, "E2169", {"start": v(3.62, 63.5) * mm, "end": v(3.63, 63.55) * mm});
            skLineSegment(sketch, "E2170", {"start": v(3.63, 63.55) * mm, "end": v(3.63, 63.6) * mm});
            skLineSegment(sketch, "E2171", {"start": v(3.63, 63.6) * mm, "end": v(3.62, 63.64) * mm});
            skLineSegment(sketch, "E2172", {"start": v(3.62, 63.64) * mm, "end": v(3.61, 63.68) * mm});
            skLineSegment(sketch, "E2173", {"start": v(3.61, 63.68) * mm, "end": v(3.6, 63.71) * mm});
            skLineSegment(sketch, "E2174", {"start": v(3.6, 63.71) * mm, "end": v(3.58, 63.74) * mm});
            skLineSegment(sketch, "E2175", {"start": v(3.58, 63.74) * mm, "end": v(3.56, 63.77) * mm});
            skLineSegment(sketch, "E2176", {"start": v(3.56, 63.77) * mm, "end": v(3.53, 63.8) * mm});
            skLineSegment(sketch, "E2177", {"start": v(3.53, 63.8) * mm, "end": v(3.5, 63.82) * mm});
            skLineSegment(sketch, "E2178", {"start": v(3.5, 63.82) * mm, "end": v(3.48, 63.85) * mm});
            skLineSegment(sketch, "E2179", {"start": v(3.48, 63.85) * mm, "end": v(3.44, 63.86) * mm});
            skLineSegment(sketch, "E2180", {"start": v(3.44, 63.86) * mm, "end": v(3.41, 63.88) * mm});
            skLineSegment(sketch, "E2181", {"start": v(3.41, 63.88) * mm, "end": v(3.37, 63.89) * mm});
            skLineSegment(sketch, "E2182", {"start": v(3.37, 63.89) * mm, "end": v(3.33, 63.89) * mm});
            skLineSegment(sketch, "E2183", {"start": v(3.33, 63.89) * mm, "end": v(3.28, 63.89) * mm});
            skLineSegment(sketch, "E2184", {"start": v(3.28, 63.89) * mm, "end": v(3.24, 63.88) * mm});
            skLineSegment(sketch, "E2185", {"start": v(3.24, 63.88) * mm, "end": v(3.2, 63.86) * mm});
            skLineSegment(sketch, "E2186", {"start": v(3.2, 63.86) * mm, "end": v(3.15, 63.84) * mm});
            skLineSegment(sketch, "E2187", {"start": v(3.15, 63.84) * mm, "end": v(3.1, 63.82) * mm});
            skLineSegment(sketch, "E2188", {"start": v(3.1, 63.82) * mm, "end": v(3.06, 63.8) * mm});
            skLineSegment(sketch, "E2189", {"start": v(3.06, 63.8) * mm, "end": v(3.02, 63.76) * mm});
            skLineSegment(sketch, "E2190", {"start": v(3.02, 63.76) * mm, "end": v(0.94, 61.68) * mm});
            skLineSegment(sketch, "E2191", {"start": v(0.94, 61.68) * mm, "end": v(0.95, 61.65) * mm});
            skLineSegment(sketch, "E2192", {"start": v(0.95, 61.65) * mm, "end": v(0.96, 61.63) * mm});
            skLineSegment(sketch, "E2193", {"start": v(0.96, 61.63) * mm, "end": v(0.97, 61.63) * mm});
            skLineSegment(sketch, "E2194", {"start": v(0.97, 61.63) * mm, "end": v(0.97, 61.63) * mm});
            skLineSegment(sketch, "E2195", {"start": v(0.97, 61.63) * mm, "end": v(0.96, 61.62) * mm});
            skLineSegment(sketch, "E2196", {"start": v(0.96, 61.62) * mm, "end": v(1, 61.55) * mm});
            skLineSegment(sketch, "E2197", {"start": v(1, 61.55) * mm, "end": v(1.08, 61.4) * mm});
            skLineSegment(sketch, "E2198", {"start": v(1.08, 61.4) * mm, "end": v(1.12, 61.34) * mm});
            skLineSegment(sketch, "E2199", {"start": v(1.12, 61.34) * mm, "end": v(1.12, 61.33) * mm});
            skLineSegment(sketch, "E2200", {"start": v(1.12, 61.33) * mm, "end": v(1.13, 61.32) * mm});
            skLineSegment(sketch, "E2201", {"start": v(1.13, 61.32) * mm, "end": v(1.13, 61.31) * mm});
            skLineSegment(sketch, "E2202", {"start": v(1.13, 61.31) * mm, "end": v(1.25, 61.1) * mm});
            skLineSegment(sketch, "E2203", {"start": v(1.25, 61.1) * mm, "end": v(1.27, 61.05) * mm});
            skLineSegment(sketch, "E2204", {"start": v(1.27, 61.05) * mm, "end": v(1.34, 60.93) * mm});
            skLineSegment(sketch, "E2205", {"start": v(1.34, 60.93) * mm, "end": v(1.35, 60.92) * mm});
            skLineSegment(sketch, "E2206", {"start": v(1.35, 60.92) * mm, "end": v(1.38, 60.86) * mm});
            skLineSegment(sketch, "E2207", {"start": v(1.38, 60.86) * mm, "end": v(1.42, 60.77) * mm});
            skLineSegment(sketch, "E2208", {"start": v(1.42, 60.77) * mm, "end": v(1.44, 60.74) * mm});
            skLineSegment(sketch, "E2209", {"start": v(1.44, 60.74) * mm, "end": v(1.48, 60.67) * mm});
            skLineSegment(sketch, "E2210", {"start": v(1.48, 60.67) * mm, "end": v(1.6, 60.45) * mm});
            skLineSegment(sketch, "E2211", {"start": v(1.6, 60.45) * mm, "end": v(1.63, 60.4) * mm});
            skLineSegment(sketch, "E2212", {"start": v(1.63, 60.4) * mm, "end": v(1.63, 60.4) * mm});
            skLineSegment(sketch, "E2213", {"start": v(1.63, 60.4) * mm, "end": v(1.64, 60.4) * mm});
            skLineSegment(sketch, "E2214", {"start": v(1.64, 60.4) * mm, "end": v(1.63, 60.4) * mm});
            skLineSegment(sketch, "E2215", {"start": v(1.63, 60.4) * mm, "end": v(1.63, 60.39) * mm});
            skLineSegment(sketch, "E2216", {"start": v(1.63, 60.39) * mm, "end": v(1.8, 60.08) * mm});
            skLineSegment(sketch, "E2217", {"start": v(1.8, 60.08) * mm, "end": v(1.8, 60.08) * mm});
            skLineSegment(sketch, "E2218", {"start": v(1.8, 60.08) * mm, "end": v(1.8, 60.07) * mm});
            skLineSegment(sketch, "E2219", {"start": v(1.8, 60.07) * mm, "end": v(1.8, 60.06) * mm});
            skLineSegment(sketch, "E2220", {"start": v(1.8, 60.06) * mm, "end": v(1.87, 59.95) * mm});
            skLineSegment(sketch, "E2221", {"start": v(1.87, 59.95) * mm, "end": v(1.87, 59.94) * mm});
            skLineSegment(sketch, "E2222", {"start": v(1.87, 59.94) * mm, "end": v(1.9, 59.88) * mm});
            skLineSegment(sketch, "E2223", {"start": v(1.9, 59.88) * mm, "end": v(1.97, 59.76) * mm});
            skLineSegment(sketch, "E2224", {"start": v(1.97, 59.76) * mm, "end": v(2.01, 59.68) * mm});
            skLineSegment(sketch, "E2225", {"start": v(2.01, 59.68) * mm, "end": v(2.04, 59.63) * mm});
            skLineSegment(sketch, "E2226", {"start": v(2.04, 59.63) * mm, "end": v(2.1, 59.52) * mm});
            skLineSegment(sketch, "E2227", {"start": v(2.1, 59.52) * mm, "end": v(2.22, 59.3) * mm});
            skLineSegment(sketch, "E2228", {"start": v(2.22, 59.3) * mm, "end": v(2.27, 59.2) * mm});
            skLineSegment(sketch, "E2229", {"start": v(2.27, 59.2) * mm, "end": v(2.29, 59.17) * mm});
            skLineSegment(sketch, "E2230", {"start": v(2.29, 59.17) * mm, "end": v(2.33, 59.08) * mm});
            skLineSegment(sketch, "E2231", {"start": v(2.33, 59.08) * mm, "end": v(2.36, 59.03) * mm});
            skLineSegment(sketch, "E2232", {"start": v(2.36, 59.03) * mm, "end": v(2.37, 59.03) * mm});
            skLineSegment(sketch, "E2233", {"start": v(2.37, 59.03) * mm, "end": v(2.37, 59.02) * mm});
            skLineSegment(sketch, "E2234", {"start": v(2.37, 59.02) * mm, "end": v(2.38, 59) * mm});
            skLineSegment(sketch, "E2235", {"start": v(2.38, 59) * mm, "end": v(2.4, 58.97) * mm});
            skLineSegment(sketch, "E2236", {"start": v(2.4, 58.97) * mm, "end": v(2.57, 58.65) * mm});
            skLineSegment(sketch, "E2237", {"start": v(2.57, 58.65) * mm, "end": v(2.63, 58.54) * mm});
            skLineSegment(sketch, "E2238", {"start": v(2.63, 58.54) * mm, "end": v(2.62, 58.53) * mm});
            skLineSegment(sketch, "E2239", {"start": v(2.62, 58.53) * mm, "end": v(2.61, 58.52) * mm});
            skLineSegment(sketch, "E2240", {"start": v(2.61, 58.52) * mm, "end": v(2.61, 58.52) * mm});
            skLineSegment(sketch, "E2241", {"start": v(2.61, 58.52) * mm, "end": v(2.36, 58.64) * mm});
            skLineSegment(sketch, "E2242", {"start": v(2.36, 58.64) * mm, "end": v(2.3, 58.67) * mm});
            skLineSegment(sketch, "E2243", {"start": v(2.3, 58.67) * mm, "end": v(2.16, 58.74) * mm});
            skLineSegment(sketch, "E2244", {"start": v(2.16, 58.74) * mm, "end": v(2.1, 58.77) * mm});
            skLineSegment(sketch, "E2245", {"start": v(2.1, 58.77) * mm, "end": v(1.8, 58.9) * mm});
            skLineSegment(sketch, "E2246", {"start": v(1.8, 58.9) * mm, "end": v(1.8, 58.9) * mm});
            skLineSegment(sketch, "E2247", {"start": v(1.8, 58.9) * mm, "end": v(1.46, 59.08) * mm});
            skLineSegment(sketch, "E2248", {"start": v(1.46, 59.08) * mm, "end": v(1.46, 59.08) * mm});
            skLineSegment(sketch, "E2249", {"start": v(1.46, 59.08) * mm, "end": v(1.13, 59.24) * mm});
            skLineSegment(sketch, "E2250", {"start": v(1.13, 59.24) * mm, "end": v(1.06, 59.27) * mm});
            skLineSegment(sketch, "E2251", {"start": v(1.06, 59.27) * mm, "end": v(0.77, 59.4) * mm});
            skLineSegment(sketch, "E2252", {"start": v(0.77, 59.4) * mm, "end": v(0.77, 59.4) * mm});
            skLineSegment(sketch, "E2253", {"start": v(0.77, 59.4) * mm, "end": v(0.43, 59.58) * mm});
            skLineSegment(sketch, "E2254", {"start": v(0.43, 59.58) * mm, "end": v(0.43, 59.58) * mm});
            skLineSegment(sketch, "E2255", {"start": v(0.43, 59.58) * mm, "end": v(0.25, 59.66) * mm});
            skLineSegment(sketch, "E2256", {"start": v(0.25, 59.66) * mm, "end": v(0.24, 59.66) * mm});
            skLineSegment(sketch, "E2257", {"start": v(0.24, 59.66) * mm, "end": v(0.24, 59.66) * mm});
            skLineSegment(sketch, "E2258", {"start": v(0.24, 59.66) * mm, "end": v(0.24, 59.67) * mm});
            skLineSegment(sketch, "E2259", {"start": v(0.24, 59.67) * mm, "end": v(0.07, 59.75) * mm});
            skLineSegment(sketch, "E2260", {"start": v(0.07, 59.75) * mm, "end": v(-0.25, 59.9) * mm});
            skLineSegment(sketch, "E2261", {"start": v(-0.25, 59.9) * mm, "end": v(-0.32, 59.94) * mm});
            skLineSegment(sketch, "E2262", {"start": v(-0.32, 59.94) * mm, "end": v(-0.55, 60.05) * mm});
            skLineSegment(sketch, "E2263", {"start": v(-0.55, 60.05) * mm, "end": v(-0.64, 60.1) * mm});
            skLineSegment(sketch, "E2264", {"start": v(-0.64, 60.1) * mm, "end": v(-2.7, 58.04) * mm});
            skLineSegment(sketch, "E2265", {"start": v(-2.7, 58.04) * mm, "end": v(-2.74, 57.99) * mm});
            skLineSegment(sketch, "E2266", {"start": v(-2.74, 57.99) * mm, "end": v(-2.78, 57.92) * mm});
            skLineSegment(sketch, "E2267", {"start": v(-2.78, 57.92) * mm, "end": v(-2.8, 57.86) * mm});
            skLineSegment(sketch, "E2268", {"start": v(-2.8, 57.86) * mm, "end": v(-2.83, 57.8) * mm});
            skLineSegment(sketch, "E2269", {"start": v(-2.83, 57.8) * mm, "end": v(-2.83, 57.75) * mm});
            skLineSegment(sketch, "E2270", {"start": v(-2.83, 57.75) * mm, "end": v(-2.82, 57.69) * mm});
            skLineSegment(sketch, "E2271", {"start": v(-2.82, 57.69) * mm, "end": v(-2.8, 57.63) * mm});
            skLineSegment(sketch, "E2272", {"start": v(-2.8, 57.63) * mm, "end": v(-2.77, 57.58) * mm});
            skLineSegment(sketch, "E2273", {"start": v(-2.77, 57.58) * mm, "end": v(-2.72, 57.53) * mm});
            skLineSegment(sketch, "E2274", {"start": v(-2.72, 57.53) * mm, "end": v(-2.7, 57.5) * mm});
            skLineSegment(sketch, "E2275", {"start": v(-2.7, 57.5) * mm, "end": v(-2.66, 57.48) * mm});
            skLineSegment(sketch, "E2276", {"start": v(-2.66, 57.48) * mm, "end": v(-2.63, 57.47) * mm});
            skLineSegment(sketch, "E2277", {"start": v(-2.63, 57.47) * mm, "end": v(-2.6, 57.46) * mm});
            skLineSegment(sketch, "E2278", {"start": v(-2.6, 57.46) * mm, "end": v(-2.56, 57.45) * mm});
            skLineSegment(sketch, "E2279", {"start": v(-2.56, 57.45) * mm, "end": v(-2.52, 57.45) * mm});
            skLineSegment(sketch, "E2280", {"start": v(-2.52, 57.45) * mm, "end": v(-2.49, 57.46) * mm});
            skLineSegment(sketch, "E2281", {"start": v(-2.49, 57.46) * mm, "end": v(-2.45, 57.47) * mm});
            skLineSegment(sketch, "E2282", {"start": v(-2.45, 57.47) * mm, "end": v(-2.38, 57.5) * mm});
            skLineSegment(sketch, "E2283", {"start": v(-2.38, 57.5) * mm, "end": v(-2.36, 57.51) * mm});
            skLineSegment(sketch, "E2284", {"start": v(-2.36, 57.51) * mm, "end": v(-2.35, 57.52) * mm});
            skLineSegment(sketch, "E2285", {"start": v(-2.35, 57.52) * mm, "end": v(-2.35, 57.52) * mm});
            skLineSegment(sketch, "E2286", {"start": v(-2.35, 57.52) * mm, "end": v(-2.34, 57.52) * mm});
            skLineSegment(sketch, "E2287", {"start": v(-2.34, 57.52) * mm, "end": v(-2.3, 57.55) * mm});
            skLineSegment(sketch, "E2288", {"start": v(-2.3, 57.55) * mm, "end": v(-2.22, 57.61) * mm});
            skLineSegment(sketch, "E2289", {"start": v(-2.22, 57.61) * mm, "end": v(-2.18, 57.64) * mm});
            skLineSegment(sketch, "E2290", {"start": v(-2.18, 57.64) * mm, "end": v(-2.15, 57.66) * mm});
            skLineSegment(sketch, "E2291", {"start": v(-2.15, 57.66) * mm, "end": v(-2.11, 57.68) * mm});
            skLineSegment(sketch, "E2292", {"start": v(-2.11, 57.68) * mm, "end": v(-2.08, 57.7) * mm});
            skLineSegment(sketch, "E2293", {"start": v(-2.08, 57.7) * mm, "end": v(-2.04, 57.7) * mm});
            skLineSegment(sketch, "E2294", {"start": v(-2.04, 57.7) * mm, "end": v(-2, 57.7) * mm});
            skLineSegment(sketch, "E2295", {"start": v(-2, 57.7) * mm, "end": v(-1.95, 57.69) * mm});
            skLineSegment(sketch, "E2296", {"start": v(-1.95, 57.69) * mm, "end": v(-1.9, 57.68) * mm});
            skLineSegment(sketch, "E2297", {"start": v(-1.9, 57.68) * mm, "end": v(-1.76, 57.64) * mm});
            skLineSegment(sketch, "E2298", {"start": v(-1.76, 57.64) * mm, "end": v(-1.66, 57.61) * mm});
            skLineSegment(sketch, "E2299", {"start": v(-1.66, 57.61) * mm, "end": v(-1.57, 57.58) * mm});
            skLineSegment(sketch, "E2300", {"start": v(-1.57, 57.58) * mm, "end": v(-1.48, 57.54) * mm});
            skLineSegment(sketch, "E2301", {"start": v(-1.48, 57.54) * mm, "end": v(-1.44, 57.52) * mm});
            skLineSegment(sketch, "E2302", {"start": v(-1.44, 57.52) * mm, "end": v(-1, 57.3) * mm});
            skLineSegment(sketch, "E2303", {"start": v(-1, 57.3) * mm, "end": v(0.08, 56.77) * mm});
            skLineSegment(sketch, "E2304", {"start": v(0.08, 56.77) * mm, "end": v(0.09, 56.77) * mm});
            skLineSegment(sketch, "E2305", {"start": v(0.09, 56.77) * mm, "end": v(0.11, 56.76) * mm});
            skLineSegment(sketch, "E2306", {"start": v(0.11, 56.76) * mm, "end": v(0.13, 56.75) * mm});
            skLineSegment(sketch, "E2307", {"start": v(0.13, 56.75) * mm, "end": v(0.67, 56.48) * mm});
            skLineSegment(sketch, "E2308", {"start": v(0.67, 56.48) * mm, "end": v(1.06, 56.29) * mm});
            skLineSegment(sketch, "E2309", {"start": v(1.06, 56.29) * mm, "end": v(1.93, 55.85) * mm});
            skLineSegment(sketch, "E2310", {"start": v(1.93, 55.85) * mm, "end": v(2.43, 55.6) * mm});
            skLineSegment(sketch, "E2311", {"start": v(2.43, 55.6) * mm, "end": v(3.3, 55.17) * mm});
            skLineSegment(sketch, "E2312", {"start": v(3.3, 55.17) * mm, "end": v(3.83, 54.9) * mm});
            skLineSegment(sketch, "E2313", {"start": v(3.83, 54.9) * mm, "end": v(4.2, 54.73) * mm});
            skLineSegment(sketch, "E2314", {"start": v(4.2, 54.73) * mm, "end": v(4.9, 54.38) * mm});
            skLineSegment(sketch, "E2315", {"start": v(9.38, 58.6) * mm, "end": v(9.4, 58.6) * mm});
            skLineSegment(sketch, "E2316", {"start": v(9.4, 58.6) * mm, "end": v(9.45, 58.6) * mm});
            skLineSegment(sketch, "E2317", {"start": v(9.45, 58.6) * mm, "end": v(9.5, 58.6) * mm});
            skLineSegment(sketch, "E2318", {"start": v(9.5, 58.6) * mm, "end": v(9.54, 58.6) * mm});
            skLineSegment(sketch, "E2319", {"start": v(9.54, 58.6) * mm, "end": v(9.58, 58.62) * mm});
            skLineSegment(sketch, "E2320", {"start": v(9.58, 58.62) * mm, "end": v(9.63, 58.64) * mm});
            skLineSegment(sketch, "E2321", {"start": v(9.63, 58.64) * mm, "end": v(9.67, 58.66) * mm});
            skLineSegment(sketch, "E2322", {"start": v(9.67, 58.66) * mm, "end": v(9.7, 58.68) * mm});
            skLineSegment(sketch, "E2323", {"start": v(9.7, 58.68) * mm, "end": v(9.74, 58.7) * mm});
            skLineSegment(sketch, "E2324", {"start": v(9.74, 58.7) * mm, "end": v(11.84, 60.8) * mm});
            skLineSegment(sketch, "E2325", {"start": v(11.84, 60.8) * mm, "end": v(5.95, 66.7) * mm});
            skLineSegment(sketch, "E2326", {"start": v(5.95, 66.7) * mm, "end": v(3.85, 64.59) * mm});
            skLineSegment(sketch, "E2327", {"start": v(3.85, 64.59) * mm, "end": v(3.83, 64.55) * mm});
            skLineSegment(sketch, "E2328", {"start": v(3.83, 64.55) * mm, "end": v(3.8, 64.5) * mm});
            skLineSegment(sketch, "E2329", {"start": v(3.8, 64.5) * mm, "end": v(3.77, 64.45) * mm});
            skLineSegment(sketch, "E2330", {"start": v(3.77, 64.45) * mm, "end": v(3.75, 64.4) * mm});
            skLineSegment(sketch, "E2331", {"start": v(3.75, 64.4) * mm, "end": v(3.74, 64.35) * mm});
            skLineSegment(sketch, "E2332", {"start": v(3.74, 64.35) * mm, "end": v(3.74, 64.3) * mm});
            skLineSegment(sketch, "E2333", {"start": v(3.74, 64.3) * mm, "end": v(3.74, 64.26) * mm});
            skLineSegment(sketch, "E2334", {"start": v(3.74, 64.26) * mm, "end": v(3.75, 64.21) * mm});
            skLineSegment(sketch, "E2335", {"start": v(3.75, 64.21) * mm, "end": v(3.77, 64.17) * mm});
            skLineSegment(sketch, "E2336", {"start": v(3.77, 64.17) * mm, "end": v(3.81, 64.1) * mm});
            skLineSegment(sketch, "E2337", {"start": v(3.81, 64.1) * mm, "end": v(3.83, 64.1) * mm});
            skLineSegment(sketch, "E2338", {"start": v(3.83, 64.1) * mm, "end": v(3.84, 64.08) * mm});
            skLineSegment(sketch, "E2339", {"start": v(3.84, 64.08) * mm, "end": v(3.85, 64.09) * mm});
            skLineSegment(sketch, "E2340", {"start": v(3.85, 64.09) * mm, "end": v(3.85, 64.08) * mm});
            skLineSegment(sketch, "E2341", {"start": v(3.85, 64.08) * mm, "end": v(3.85, 64.07) * mm});
            skLineSegment(sketch, "E2342", {"start": v(3.85, 64.07) * mm, "end": v(3.86, 64.06) * mm});
            skLineSegment(sketch, "E2343", {"start": v(3.86, 64.06) * mm, "end": v(3.91, 64.03) * mm});
            skLineSegment(sketch, "E2344", {"start": v(3.91, 64.03) * mm, "end": v(3.96, 64) * mm});
            skLineSegment(sketch, "E2345", {"start": v(3.96, 64) * mm, "end": v(4.01, 64) * mm});
            skLineSegment(sketch, "E2346", {"start": v(4.01, 64) * mm, "end": v(4.06, 64) * mm});
            skLineSegment(sketch, "E2347", {"start": v(4.06, 64) * mm, "end": v(4.12, 64) * mm});
            skLineSegment(sketch, "E2348", {"start": v(4.12, 64) * mm, "end": v(4.16, 64.02) * mm});
            skLineSegment(sketch, "E2349", {"start": v(4.16, 64.02) * mm, "end": v(4.37, 64.12) * mm});
            skLineSegment(sketch, "E2350", {"start": v(4.37, 64.12) * mm, "end": v(4.41, 64.14) * mm});
            skLineSegment(sketch, "E2351", {"start": v(4.41, 64.14) * mm, "end": v(4.46, 64.15) * mm});
            skLineSegment(sketch, "E2352", {"start": v(4.46, 64.15) * mm, "end": v(4.52, 64.15) * mm});
            skLineSegment(sketch, "E2353", {"start": v(4.52, 64.15) * mm, "end": v(4.59, 64.15) * mm});
            skLineSegment(sketch, "E2354", {"start": v(4.59, 64.15) * mm, "end": v(4.63, 64.13) * mm});
            skLineSegment(sketch, "E2355", {"start": v(4.63, 64.13) * mm, "end": v(4.69, 64.1) * mm});
            skLineSegment(sketch, "E2356", {"start": v(4.69, 64.1) * mm, "end": v(4.75, 64.05) * mm});
            skLineSegment(sketch, "E2357", {"start": v(4.75, 64.05) * mm, "end": v(4.76, 64.04) * mm});
            skLineSegment(sketch, "E2358", {"start": v(4.76, 64.04) * mm, "end": v(4.77, 64.03) * mm});
            skLineSegment(sketch, "E2359", {"start": v(4.77, 64.03) * mm, "end": v(4.77, 64.03) * mm});
            skLineSegment(sketch, "E2360", {"start": v(4.77, 64.03) * mm, "end": v(9.21, 59.58) * mm});
            skLineSegment(sketch, "E2361", {"start": v(9.21, 59.58) * mm, "end": v(9.24, 59.54) * mm});
            skLineSegment(sketch, "E2362", {"start": v(9.24, 59.54) * mm, "end": v(9.27, 59.5) * mm});
            skLineSegment(sketch, "E2363", {"start": v(9.27, 59.5) * mm, "end": v(9.29, 59.47) * mm});
            skLineSegment(sketch, "E2364", {"start": v(9.29, 59.47) * mm, "end": v(9.3, 59.43) * mm});
            skLineSegment(sketch, "E2365", {"start": v(9.3, 59.43) * mm, "end": v(9.3, 59.38) * mm});
            skLineSegment(sketch, "E2366", {"start": v(9.3, 59.38) * mm, "end": v(9.3, 59.34) * mm});
            skLineSegment(sketch, "E2367", {"start": v(9.3, 59.34) * mm, "end": v(9.3, 59.3) * mm});
            skLineSegment(sketch, "E2368", {"start": v(9.3, 59.3) * mm, "end": v(9.28, 59.27) * mm});
            skLineSegment(sketch, "E2369", {"start": v(9.28, 59.27) * mm, "end": v(9.27, 59.22) * mm});
            skLineSegment(sketch, "E2370", {"start": v(9.27, 59.22) * mm, "end": v(9.25, 59.19) * mm});
            skLineSegment(sketch, "E2371", {"start": v(9.25, 59.19) * mm, "end": v(9.16, 59) * mm});
            skLineSegment(sketch, "E2372", {"start": v(9.16, 59) * mm, "end": v(9.15, 58.96) * mm});
            skLineSegment(sketch, "E2373", {"start": v(9.15, 58.96) * mm, "end": v(9.15, 58.92) * mm});
            skLineSegment(sketch, "E2374", {"start": v(9.15, 58.92) * mm, "end": v(9.15, 58.89) * mm});
            skLineSegment(sketch, "E2375", {"start": v(9.15, 58.89) * mm, "end": v(9.15, 58.85) * mm});
            skLineSegment(sketch, "E2376", {"start": v(9.15, 58.85) * mm, "end": v(9.16, 58.82) * mm});
            skLineSegment(sketch, "E2377", {"start": v(9.16, 58.82) * mm, "end": v(9.17, 58.78) * mm});
            skLineSegment(sketch, "E2378", {"start": v(9.17, 58.78) * mm, "end": v(9.19, 58.75) * mm});
            skLineSegment(sketch, "E2379", {"start": v(9.19, 58.75) * mm, "end": v(9.21, 58.71) * mm});
            skLineSegment(sketch, "E2380", {"start": v(9.21, 58.71) * mm, "end": v(9.24, 58.68) * mm});
            skLineSegment(sketch, "E2381", {"start": v(9.24, 58.68) * mm, "end": v(9.27, 58.65) * mm});
            skLineSegment(sketch, "E2382", {"start": v(9.27, 58.65) * mm, "end": v(9.3, 58.63) * mm});
            skLineSegment(sketch, "E2383", {"start": v(9.3, 58.63) * mm, "end": v(9.34, 58.61) * mm});
            skLineSegment(sketch, "E2384", {"start": v(9.34, 58.61) * mm, "end": v(9.38, 58.6) * mm});
            skLineSegment(sketch, "E2385", {"start": v(0.14, 41.51) * mm, "end": v(0.17, 41.57) * mm});
            skLineSegment(sketch, "E2386", {"start": v(0.17, 41.57) * mm, "end": v(0.2, 41.63) * mm});
            skLineSegment(sketch, "E2387", {"start": v(0.2, 41.63) * mm, "end": v(0.2, 41.67) * mm});
            skLineSegment(sketch, "E2388", {"start": v(0.2, 41.67) * mm, "end": v(0.2, 41.7) * mm});
            skLineSegment(sketch, "E2389", {"start": v(0.2, 41.7) * mm, "end": v(0.18, 41.75) * mm});
            skLineSegment(sketch, "E2390", {"start": v(0.18, 41.75) * mm, "end": v(0.16, 41.8) * mm});
            skLineSegment(sketch, "E2391", {"start": v(0.16, 41.8) * mm, "end": v(-2.35, 44.3) * mm});
            skLineSegment(sketch, "E2392", {"start": v(-2.35, 44.3) * mm, "end": v(-2.39, 44.33) * mm});
            skLineSegment(sketch, "E2393", {"start": v(-2.39, 44.33) * mm, "end": v(-2.42, 44.35) * mm});
            skLineSegment(sketch, "E2394", {"start": v(-2.42, 44.35) * mm, "end": v(-2.45, 44.36) * mm});
            skLineSegment(sketch, "E2395", {"start": v(-2.45, 44.36) * mm, "end": v(-2.49, 44.37) * mm});
            skLineSegment(sketch, "E2396", {"start": v(-2.49, 44.37) * mm, "end": v(-2.52, 44.37) * mm});
            skLineSegment(sketch, "E2397", {"start": v(-2.52, 44.37) * mm, "end": v(-2.55, 44.36) * mm});
            skLineSegment(sketch, "E2398", {"start": v(-2.55, 44.36) * mm, "end": v(-2.6, 44.34) * mm});
            skLineSegment(sketch, "E2399", {"start": v(-2.6, 44.34) * mm, "end": v(-2.68, 44.3) * mm});
            skLineSegment(sketch, "E2400", {"start": v(-2.68, 44.3) * mm, "end": v(-2.73, 44.29) * mm});
            skLineSegment(sketch, "E2401", {"start": v(-2.73, 44.29) * mm, "end": v(-2.76, 44.28) * mm});
            skLineSegment(sketch, "E2402", {"start": v(-2.76, 44.28) * mm, "end": v(-2.78, 44.28) * mm});
            skLineSegment(sketch, "E2403", {"start": v(-2.78, 44.28) * mm, "end": v(-2.82, 44.3) * mm});
            skLineSegment(sketch, "E2404", {"start": v(-2.82, 44.3) * mm, "end": v(-2.85, 44.31) * mm});
            skLineSegment(sketch, "E2405", {"start": v(-2.85, 44.31) * mm, "end": v(-2.88, 44.33) * mm});
            skLineSegment(sketch, "E2406", {"start": v(-2.88, 44.33) * mm, "end": v(-2.9, 44.35) * mm});
            skLineSegment(sketch, "E2407", {"start": v(-2.9, 44.35) * mm, "end": v(-2.9, 44.36) * mm});
            skLineSegment(sketch, "E2408", {"start": v(-2.9, 44.36) * mm, "end": v(-2.9, 44.37) * mm});
            skLineSegment(sketch, "E2409", {"start": v(-2.9, 44.37) * mm, "end": v(-2.9, 44.36) * mm});
            skLineSegment(sketch, "E2410", {"start": v(-2.9, 44.36) * mm, "end": v(-2.91, 44.37) * mm});
            skLineSegment(sketch, "E2411", {"start": v(-2.91, 44.37) * mm, "end": v(-2.92, 44.4) * mm});
            skLineSegment(sketch, "E2412", {"start": v(-2.92, 44.4) * mm, "end": v(-2.93, 44.41) * mm});
            skLineSegment(sketch, "E2413", {"start": v(-2.93, 44.41) * mm, "end": v(-2.94, 44.43) * mm});
            skLineSegment(sketch, "E2414", {"start": v(-2.94, 44.43) * mm, "end": v(-2.94, 44.46) * mm});
            skLineSegment(sketch, "E2415", {"start": v(-2.94, 44.46) * mm, "end": v(-2.93, 44.48) * mm});
            skLineSegment(sketch, "E2416", {"start": v(-2.93, 44.48) * mm, "end": v(-2.92, 44.53) * mm});
            skLineSegment(sketch, "E2417", {"start": v(-2.92, 44.53) * mm, "end": v(-2.89, 44.58) * mm});
            skLineSegment(sketch, "E2418", {"start": v(-2.89, 44.58) * mm, "end": v(-2.86, 44.62) * mm});
            skLineSegment(sketch, "E2419", {"start": v(-2.86, 44.62) * mm, "end": v(-2.86, 44.62) * mm});
            skLineSegment(sketch, "E2420", {"start": v(-2.86, 44.62) * mm, "end": v(-1.68, 45.8) * mm});
            skLineSegment(sketch, "E2421", {"start": v(-1.68, 45.8) * mm, "end": v(1.62, 42.5) * mm});
            skLineSegment(sketch, "E2422", {"start": v(1.62, 42.5) * mm, "end": v(1.62, 42.49) * mm});
            skLineSegment(sketch, "E2423", {"start": v(1.62, 42.49) * mm, "end": v(0.65, 41.52) * mm});
            skLineSegment(sketch, "E2424", {"start": v(0.65, 41.52) * mm, "end": v(0.65, 41.51) * mm});
            skLineSegment(sketch, "E2425", {"start": v(0.65, 41.51) * mm, "end": v(13.34, 41.51) * mm});
            skLineSegment(sketch, "E2426", {"start": v(13.34, 41.51) * mm, "end": v(13.34, 54.2) * mm});
            skLineSegment(sketch, "E2427", {"start": v(13.34, 54.2) * mm, "end": v(12.25, 53.12) * mm});
            skLineSegment(sketch, "E2428", {"start": v(12.25, 53.12) * mm, "end": v(12.22, 53.1) * mm});
            skLineSegment(sketch, "E2429", {"start": v(12.22, 53.1) * mm, "end": v(12.19, 53.08) * mm});
            skLineSegment(sketch, "E2430", {"start": v(12.19, 53.08) * mm, "end": v(12.15, 53.06) * mm});
            skLineSegment(sketch, "E2431", {"start": v(12.15, 53.06) * mm, "end": v(12.12, 53.06) * mm});
            skLineSegment(sketch, "E2432", {"start": v(12.12, 53.06) * mm, "end": v(12.09, 53.06) * mm});
            skLineSegment(sketch, "E2433", {"start": v(12.09, 53.06) * mm, "end": v(12.05, 53.06) * mm});
            skLineSegment(sketch, "E2434", {"start": v(12.05, 53.06) * mm, "end": v(12.02, 53.07) * mm});
            skLineSegment(sketch, "E2435", {"start": v(12.02, 53.07) * mm, "end": v(12, 53.09) * mm});
            skLineSegment(sketch, "E2436", {"start": v(12, 53.09) * mm, "end": v(11.97, 53.11) * mm});
            skLineSegment(sketch, "E2437", {"start": v(11.97, 53.11) * mm, "end": v(11.95, 53.13) * mm});
            skLineSegment(sketch, "E2438", {"start": v(11.95, 53.13) * mm, "end": v(11.94, 53.16) * mm});
            skLineSegment(sketch, "E2439", {"start": v(11.94, 53.16) * mm, "end": v(11.93, 53.18) * mm});
            skLineSegment(sketch, "E2440", {"start": v(11.93, 53.18) * mm, "end": v(11.92, 53.2) * mm});
            skLineSegment(sketch, "E2441", {"start": v(11.92, 53.2) * mm, "end": v(11.92, 53.23) * mm});
            skLineSegment(sketch, "E2442", {"start": v(11.92, 53.23) * mm, "end": v(11.93, 53.26) * mm});
            skLineSegment(sketch, "E2443", {"start": v(11.93, 53.26) * mm, "end": v(11.94, 53.3) * mm});
            skLineSegment(sketch, "E2444", {"start": v(11.94, 53.3) * mm, "end": v(11.96, 53.34) * mm});
            skLineSegment(sketch, "E2445", {"start": v(11.96, 53.34) * mm, "end": v(12, 53.43) * mm});
            skLineSegment(sketch, "E2446", {"start": v(12, 53.43) * mm, "end": v(12, 53.47) * mm});
            skLineSegment(sketch, "E2447", {"start": v(12, 53.47) * mm, "end": v(12.01, 53.5) * mm});
            skLineSegment(sketch, "E2448", {"start": v(12.01, 53.5) * mm, "end": v(12, 53.52) * mm});
            skLineSegment(sketch, "E2449", {"start": v(12, 53.52) * mm, "end": v(12, 53.55) * mm});
            skLineSegment(sketch, "E2450", {"start": v(12, 53.55) * mm, "end": v(12, 53.57) * mm});
            skLineSegment(sketch, "E2451", {"start": v(12, 53.57) * mm, "end": v(11.97, 53.6) * mm});
            skLineSegment(sketch, "E2452", {"start": v(11.97, 53.6) * mm, "end": v(11.95, 53.63) * mm});
            skLineSegment(sketch, "E2453", {"start": v(11.95, 53.63) * mm, "end": v(9.05, 56.53) * mm});
            skLineSegment(sketch, "E2454", {"start": v(9.05, 56.53) * mm, "end": v(10.13, 57.6) * mm});
            skLineSegment(sketch, "E2455", {"start": v(10.13, 57.6) * mm, "end": v(13.06, 54.68) * mm});
            skLineSegment(sketch, "E2456", {"start": v(13.06, 54.68) * mm, "end": v(13.1, 54.66) * mm});
            skLineSegment(sketch, "E2457", {"start": v(13.1, 54.66) * mm, "end": v(13.14, 54.65) * mm});
            skLineSegment(sketch, "E2458", {"start": v(13.14, 54.65) * mm, "end": v(13.18, 54.65) * mm});
            skLineSegment(sketch, "E2459", {"start": v(13.18, 54.65) * mm, "end": v(13.23, 54.66) * mm});
            skLineSegment(sketch, "E2460", {"start": v(13.23, 54.66) * mm, "end": v(13.3, 54.69) * mm});
            skLineSegment(sketch, "E2461", {"start": v(13.3, 54.69) * mm, "end": v(13.34, 54.7) * mm});
            skLineSegment(sketch, "E2462", {"start": v(13.34, 54.7) * mm, "end": v(13.34, 62.3) * mm});
            skLineSegment(sketch, "E2463", {"start": v(13.34, 62.3) * mm, "end": v(13.33, 62.3) * mm});
            skLineSegment(sketch, "E2464", {"start": v(13.33, 62.3) * mm, "end": v(12.2, 61.16) * mm});
            skLineSegment(sketch, "E2465", {"start": v(12.2, 61.16) * mm, "end": v(11.74, 61.61) * mm});
            skLineSegment(sketch, "E2466", {"start": v(11.74, 61.61) * mm, "end": v(11.78, 61.66) * mm});
            skLineSegment(sketch, "E2467", {"start": v(11.78, 61.66) * mm, "end": v(11.82, 61.73) * mm});
            skLineSegment(sketch, "E2468", {"start": v(11.82, 61.73) * mm, "end": v(11.88, 61.82) * mm});
            skLineSegment(sketch, "E2469", {"start": v(11.88, 61.82) * mm, "end": v(11.94, 61.92) * mm});
            skLineSegment(sketch, "E2470", {"start": v(11.94, 61.92) * mm, "end": v(12, 62.02) * mm});
            skLineSegment(sketch, "E2471", {"start": v(12, 62.02) * mm, "end": v(12.04, 62.12) * mm});
            skLineSegment(sketch, "E2472", {"start": v(12.04, 62.12) * mm, "end": v(12.08, 62.22) * mm});
            skLineSegment(sketch, "E2473", {"start": v(12.08, 62.22) * mm, "end": v(12.11, 62.32) * mm});
            skLineSegment(sketch, "E2474", {"start": v(12.11, 62.32) * mm, "end": v(12.14, 62.43) * mm});
            skLineSegment(sketch, "E2475", {"start": v(12.14, 62.43) * mm, "end": v(12.17, 62.54) * mm});
            skLineSegment(sketch, "E2476", {"start": v(12.17, 62.54) * mm, "end": v(12.18, 62.63) * mm});
            skLineSegment(sketch, "E2477", {"start": v(12.18, 62.63) * mm, "end": v(12.2, 62.72) * mm});
            skLineSegment(sketch, "E2478", {"start": v(12.2, 62.72) * mm, "end": v(12.2, 62.81) * mm});
            skLineSegment(sketch, "E2479", {"start": v(12.2, 62.81) * mm, "end": v(12.2, 62.9) * mm});
            skLineSegment(sketch, "E2480", {"start": v(12.2, 62.9) * mm, "end": v(12.2, 63) * mm});
            skLineSegment(sketch, "E2481", {"start": v(12.2, 63) * mm, "end": v(12.2, 63.09) * mm});
            skLineSegment(sketch, "E2482", {"start": v(12.2, 63.09) * mm, "end": v(12.2, 63.18) * mm});
            skLineSegment(sketch, "E2483", {"start": v(12.2, 63.18) * mm, "end": v(12.19, 63.28) * mm});
            skLineSegment(sketch, "E2484", {"start": v(12.19, 63.28) * mm, "end": v(12.17, 63.37) * mm});
            skLineSegment(sketch, "E2485", {"start": v(12.17, 63.37) * mm, "end": v(12.16, 63.46) * mm});
            skLineSegment(sketch, "E2486", {"start": v(12.16, 63.46) * mm, "end": v(12.13, 63.56) * mm});
            skLineSegment(sketch, "E2487", {"start": v(12.13, 63.56) * mm, "end": v(12.1, 63.65) * mm});
            skLineSegment(sketch, "E2488", {"start": v(12.1, 63.65) * mm, "end": v(12.08, 63.74) * mm});
            skLineSegment(sketch, "E2489", {"start": v(12.08, 63.74) * mm, "end": v(12.04, 63.84) * mm});
            skLineSegment(sketch, "E2490", {"start": v(12.04, 63.84) * mm, "end": v(12, 63.93) * mm});
            skLineSegment(sketch, "E2491", {"start": v(12, 63.93) * mm, "end": v(11.97, 64.02) * mm});
            skLineSegment(sketch, "E2492", {"start": v(11.97, 64.02) * mm, "end": v(11.93, 64.1) * mm});
            skLineSegment(sketch, "E2493", {"start": v(11.93, 64.1) * mm, "end": v(11.9, 64.18) * mm});
            skLineSegment(sketch, "E2494", {"start": v(11.9, 64.18) * mm, "end": v(11.88, 64.25) * mm});
            skLineSegment(sketch, "E2495", {"start": v(11.88, 64.25) * mm, "end": v(11.86, 64.31) * mm});
            skLineSegment(sketch, "E2496", {"start": v(11.86, 64.31) * mm, "end": v(11.86, 64.35) * mm});
            skLineSegment(sketch, "E2497", {"start": v(11.86, 64.35) * mm, "end": v(11.86, 64.4) * mm});
            skLineSegment(sketch, "E2498", {"start": v(11.86, 64.4) * mm, "end": v(11.86, 64.43) * mm});
            skLineSegment(sketch, "E2499", {"start": v(11.86, 64.43) * mm, "end": v(11.86, 64.46) * mm});
            skLineSegment(sketch, "E2500", {"start": v(11.86, 64.46) * mm, "end": v(11.88, 64.5) * mm});
            skLineSegment(sketch, "E2501", {"start": v(11.88, 64.5) * mm, "end": v(11.9, 64.52) * mm});
            skLineSegment(sketch, "E2502", {"start": v(11.9, 64.52) * mm, "end": v(11.91, 64.55) * mm});
            skLineSegment(sketch, "E2503", {"start": v(11.91, 64.55) * mm, "end": v(11.93, 64.58) * mm});
            skLineSegment(sketch, "E2504", {"start": v(11.93, 64.58) * mm, "end": v(11.98, 64.62) * mm});
            skLineSegment(sketch, "E2505", {"start": v(11.98, 64.62) * mm, "end": v(12.03, 64.65) * mm});
            skLineSegment(sketch, "E2506", {"start": v(12.03, 64.65) * mm, "end": v(12.08, 64.67) * mm});
            skLineSegment(sketch, "E2507", {"start": v(12.08, 64.67) * mm, "end": v(12.12, 64.68) * mm});
            skLineSegment(sketch, "E2508", {"start": v(12.12, 64.68) * mm, "end": v(12.17, 64.69) * mm});
            skLineSegment(sketch, "E2509", {"start": v(12.17, 64.69) * mm, "end": v(12.22, 64.68) * mm});
            skLineSegment(sketch, "E2510", {"start": v(12.22, 64.68) * mm, "end": v(12.27, 64.66) * mm});
            skLineSegment(sketch, "E2511", {"start": v(12.27, 64.66) * mm, "end": v(12.32, 64.63) * mm});
            skLineSegment(sketch, "E2512", {"start": v(12.32, 64.63) * mm, "end": v(12.35, 64.6) * mm});
            skLineSegment(sketch, "E2513", {"start": v(12.35, 64.6) * mm, "end": v(13.33, 63.63) * mm});
            skLineSegment(sketch, "E2514", {"start": v(13.33, 63.63) * mm, "end": v(13.34, 63.24) * mm});
            skLineSegment(sketch, "E2515", {"start": v(13.34, 63.24) * mm, "end": v(13.34, 68.19) * mm});
            skLineSegment(sketch, "E2516", {"start": v(13.34, 68.19) * mm, "end": v(8.68, 68.19) * mm});
            skLineSegment(sketch, "E2517", {"start": v(8.68, 68.19) * mm, "end": v(8.68, 68.18) * mm});
            skLineSegment(sketch, "E2518", {"start": v(8.68, 68.18) * mm, "end": v(9.69, 67.17) * mm});
            skLineSegment(sketch, "E2519", {"start": v(9.69, 67.17) * mm, "end": v(9.7, 67.14) * mm});
            skLineSegment(sketch, "E2520", {"start": v(9.7, 67.14) * mm, "end": v(9.72, 67.1) * mm});
            skLineSegment(sketch, "E2521", {"start": v(9.72, 67.1) * mm, "end": v(9.73, 67.06) * mm});
            skLineSegment(sketch, "E2522", {"start": v(9.73, 67.06) * mm, "end": v(9.73, 67.02) * mm});
            skLineSegment(sketch, "E2523", {"start": v(9.73, 67.02) * mm, "end": v(9.73, 66.98) * mm});
            skLineSegment(sketch, "E2524", {"start": v(9.73, 66.98) * mm, "end": v(9.72, 66.94) * mm});
            skLineSegment(sketch, "E2525", {"start": v(9.72, 66.94) * mm, "end": v(9.7, 66.9) * mm});
            skLineSegment(sketch, "E2526", {"start": v(9.7, 66.9) * mm, "end": v(9.67, 66.85) * mm});
            skLineSegment(sketch, "E2527", {"start": v(9.67, 66.85) * mm, "end": v(9.63, 66.8) * mm});
            skLineSegment(sketch, "E2528", {"start": v(9.63, 66.8) * mm, "end": v(9.6, 66.77) * mm});
            skLineSegment(sketch, "E2529", {"start": v(9.6, 66.77) * mm, "end": v(9.57, 66.74) * mm});
            skLineSegment(sketch, "E2530", {"start": v(9.57, 66.74) * mm, "end": v(9.54, 66.72) * mm});
            skLineSegment(sketch, "E2531", {"start": v(9.54, 66.72) * mm, "end": v(9.5, 66.7) * mm});
            skLineSegment(sketch, "E2532", {"start": v(9.5, 66.7) * mm, "end": v(9.47, 66.69) * mm});
            skLineSegment(sketch, "E2533", {"start": v(9.47, 66.69) * mm, "end": v(9.42, 66.69) * mm});
            skLineSegment(sketch, "E2534", {"start": v(9.42, 66.69) * mm, "end": v(9.36, 66.69) * mm});
            skLineSegment(sketch, "E2535", {"start": v(9.36, 66.69) * mm, "end": v(9.32, 66.7) * mm});
            skLineSegment(sketch, "E2536", {"start": v(9.32, 66.7) * mm, "end": v(9.27, 66.72) * mm});
            skLineSegment(sketch, "E2537", {"start": v(9.27, 66.72) * mm, "end": v(9.1, 66.8) * mm});
            skLineSegment(sketch, "E2538", {"start": v(9.1, 66.8) * mm, "end": v(9.04, 66.83) * mm});
            skLineSegment(sketch, "E2539", {"start": v(9.04, 66.83) * mm, "end": v(8.94, 66.87) * mm});
            skLineSegment(sketch, "E2540", {"start": v(8.94, 66.87) * mm, "end": v(8.84, 66.91) * mm});
            skLineSegment(sketch, "E2541", {"start": v(8.84, 66.91) * mm, "end": v(8.74, 66.94) * mm});
            skLineSegment(sketch, "E2542", {"start": v(8.74, 66.94) * mm, "end": v(8.65, 66.97) * mm});
            skLineSegment(sketch, "E2543", {"start": v(8.65, 66.97) * mm, "end": v(8.55, 67) * mm});
            skLineSegment(sketch, "E2544", {"start": v(8.55, 67) * mm, "end": v(8.46, 67.02) * mm});
            skLineSegment(sketch, "E2545", {"start": v(8.46, 67.02) * mm, "end": v(8.36, 67.03) * mm});
            skLineSegment(sketch, "E2546", {"start": v(8.36, 67.03) * mm, "end": v(8.27, 67.05) * mm});
            skLineSegment(sketch, "E2547", {"start": v(8.27, 67.05) * mm, "end": v(8.2, 67.05) * mm});
            skLineSegment(sketch, "E2548", {"start": v(8.2, 67.05) * mm, "end": v(7.95, 67.05) * mm});
            skLineSegment(sketch, "E2549", {"start": v(7.95, 67.05) * mm, "end": v(7.9, 67.05) * mm});
            skLineSegment(sketch, "E2550", {"start": v(7.9, 67.05) * mm, "end": v(7.74, 67.03) * mm});
            skLineSegment(sketch, "E2551", {"start": v(7.74, 67.03) * mm, "end": v(7.6, 67) * mm});
            skLineSegment(sketch, "E2552", {"start": v(7.6, 67) * mm, "end": v(7.46, 66.96) * mm});
            skLineSegment(sketch, "E2553", {"start": v(7.46, 66.96) * mm, "end": v(7.3, 66.9) * mm});
            skLineSegment(sketch, "E2554", {"start": v(7.3, 66.9) * mm, "end": v(7.26, 66.88) * mm});
            skLineSegment(sketch, "E2555", {"start": v(7.26, 66.88) * mm, "end": v(7.06, 66.79) * mm});
            skLineSegment(sketch, "E2556", {"start": v(7.06, 66.79) * mm, "end": v(7.06, 66.78) * mm});
            skLineSegment(sketch, "E2557", {"start": v(7.06, 66.78) * mm, "end": v(7.05, 66.78) * mm});
            skLineSegment(sketch, "E2558", {"start": v(7.05, 66.78) * mm, "end": v(7.06, 66.78) * mm});
            skLineSegment(sketch, "E2559", {"start": v(7.06, 66.78) * mm, "end": v(6.98, 66.73) * mm});
            skLineSegment(sketch, "E2560", {"start": v(6.98, 66.73) * mm, "end": v(6.83, 66.64) * mm});
            skLineSegment(sketch, "E2561", {"start": v(6.83, 66.64) * mm, "end": v(6.76, 66.6) * mm});
            skLineSegment(sketch, "E2562", {"start": v(6.76, 66.6) * mm, "end": v(6.32, 67.04) * mm});
            skLineSegment(sketch, "E2563", {"start": v(6.32, 67.04) * mm, "end": v(6.32, 67.05) * mm});
            skLineSegment(sketch, "E2564", {"start": v(6.32, 67.05) * mm, "end": v(6.32, 67.05) * mm});
            skLineSegment(sketch, "E2565", {"start": v(6.32, 67.05) * mm, "end": v(6.31, 67.04) * mm});
            skLineSegment(sketch, "E2566", {"start": v(6.31, 67.04) * mm, "end": v(6.3, 67.05) * mm});
            skLineSegment(sketch, "E2567", {"start": v(6.3, 67.05) * mm, "end": v(6.32, 67.06) * mm});
            skLineSegment(sketch, "E2568", {"start": v(6.32, 67.06) * mm, "end": v(6.33, 67.07) * mm});
            skLineSegment(sketch, "E2569", {"start": v(6.33, 67.07) * mm, "end": v(6.34, 67.07) * mm});
            skLineSegment(sketch, "E2570", {"start": v(6.34, 67.07) * mm, "end": v(6.34, 67.07) * mm});
            skLineSegment(sketch, "E2571", {"start": v(6.34, 67.07) * mm, "end": v(6.34, 67.08) * mm});
            skLineSegment(sketch, "E2572", {"start": v(6.34, 67.08) * mm, "end": v(7.44, 68.18) * mm});
            skLineSegment(sketch, "E2573", {"start": v(7.44, 68.18) * mm, "end": v(7.44, 68.19) * mm});
            skLineSegment(sketch, "E2574", {"start": v(7.44, 68.19) * mm, "end": v(-13.34, 68.19) * mm});
            skLineSegment(sketch, "E2575", {"start": v(-13.34, 68.19) * mm, "end": v(-13.34, 47.4) * mm});
            skLineSegment(sketch, "E2576", {"start": v(-13.34, 47.4) * mm, "end": v(-13.33, 47.4) * mm});
            skLineSegment(sketch, "E2577", {"start": v(-13.33, 47.4) * mm, "end": v(-11.42, 49.31) * mm});
            skLineSegment(sketch, "E2578", {"start": v(-11.42, 49.31) * mm, "end": v(-11.38, 49.35) * mm});
            skLineSegment(sketch, "E2579", {"start": v(-11.38, 49.35) * mm, "end": v(-11.32, 49.39) * mm});
            skLineSegment(sketch, "E2580", {"start": v(-11.32, 49.39) * mm, "end": v(-11.25, 49.42) * mm});
            skLineSegment(sketch, "E2581", {"start": v(-11.25, 49.42) * mm, "end": v(-11.19, 49.44) * mm});
            skLineSegment(sketch, "E2582", {"start": v(-11.19, 49.44) * mm, "end": v(-11.12, 49.44) * mm});
            skLineSegment(sketch, "E2583", {"start": v(-11.12, 49.44) * mm, "end": v(-11.08, 49.44) * mm});
            skLineSegment(sketch, "E2584", {"start": v(-11.08, 49.44) * mm, "end": v(-11.04, 49.43) * mm});
            skLineSegment(sketch, "E2585", {"start": v(-11.04, 49.43) * mm, "end": v(-11, 49.42) * mm});
            skLineSegment(sketch, "E2586", {"start": v(-11, 49.42) * mm, "end": v(-10.97, 49.4) * mm});
            skLineSegment(sketch, "E2587", {"start": v(-10.97, 49.4) * mm, "end": v(-10.93, 49.37) * mm});
            skLineSegment(sketch, "E2588", {"start": v(-10.93, 49.37) * mm, "end": v(-10.89, 49.33) * mm});
            skLineSegment(sketch, "E2589", {"start": v(-10.89, 49.33) * mm, "end": v(-10.86, 49.3) * mm});
            skLineSegment(sketch, "E2590", {"start": v(-10.86, 49.3) * mm, "end": v(-10.84, 49.25) * mm});
            skLineSegment(sketch, "E2591", {"start": v(-10.84, 49.25) * mm, "end": v(-10.83, 49.2) * mm});
            skLineSegment(sketch, "E2592", {"start": v(-10.83, 49.2) * mm, "end": v(-10.82, 49.16) * mm});
            skLineSegment(sketch, "E2593", {"start": v(-10.82, 49.16) * mm, "end": v(-10.82, 49.1) * mm});
            skLineSegment(sketch, "E2594", {"start": v(-10.82, 49.1) * mm, "end": v(-10.83, 49.05) * mm});
            skLineSegment(sketch, "E2595", {"start": v(-10.83, 49.05) * mm, "end": v(-10.84, 49.02) * mm});
            skLineSegment(sketch, "E2596", {"start": v(-10.84, 49.02) * mm, "end": v(-10.93, 48.83) * mm});
            skLineSegment(sketch, "E2597", {"start": v(-10.93, 48.83) * mm, "end": v(-10.95, 48.77) * mm});
            skLineSegment(sketch, "E2598", {"start": v(-10.95, 48.77) * mm, "end": v(-10.97, 48.71) * mm});
            skLineSegment(sketch, "E2599", {"start": v(-10.97, 48.71) * mm, "end": v(-10.97, 48.66) * mm});
            skLineSegment(sketch, "E2600", {"start": v(-10.97, 48.66) * mm, "end": v(-10.97, 48.6) * mm});
            skLineSegment(sketch, "E2601", {"start": v(-10.97, 48.6) * mm, "end": v(-10.96, 48.57) * mm});
            skLineSegment(sketch, "E2602", {"start": v(-10.96, 48.57) * mm, "end": v(-10.93, 48.52) * mm});
            skLineSegment(sketch, "E2603", {"start": v(-10.93, 48.52) * mm, "end": v(-10.9, 48.46) * mm});
            skLineSegment(sketch, "E2604", {"start": v(-10.9, 48.46) * mm, "end": v(-10.87, 48.44) * mm});
            skLineSegment(sketch, "E2605", {"start": v(-10.87, 48.44) * mm, "end": v(-10.87, 48.44) * mm});
            skLineSegment(sketch, "E2606", {"start": v(-10.87, 48.44) * mm, "end": v(-6.4, 43.96) * mm});
            skLineSegment(sketch, "E2607", {"start": v(-6.4, 43.96) * mm, "end": v(-6.36, 43.94) * mm});
            skLineSegment(sketch, "E2608", {"start": v(-6.36, 43.94) * mm, "end": v(-6.29, 43.9) * mm});
            skLineSegment(sketch, "E2609", {"start": v(-6.29, 43.9) * mm, "end": v(-6.25, 43.88) * mm});
            skLineSegment(sketch, "E2610", {"start": v(-6.25, 43.88) * mm, "end": v(-6.2, 43.88) * mm});
            skLineSegment(sketch, "E2611", {"start": v(-6.2, 43.88) * mm, "end": v(-6.14, 43.88) * mm});
            skLineSegment(sketch, "E2612", {"start": v(-6.14, 43.88) * mm, "end": v(-6.08, 43.9) * mm});
            skLineSegment(sketch, "E2613", {"start": v(-6.08, 43.9) * mm, "end": v(-6.03, 43.92) * mm});
            skLineSegment(sketch, "E2614", {"start": v(-6.03, 43.92) * mm, "end": v(-5.85, 44) * mm});
            skLineSegment(sketch, "E2615", {"start": v(-5.85, 44) * mm, "end": v(-5.82, 44.02) * mm});
            skLineSegment(sketch, "E2616", {"start": v(-5.82, 44.02) * mm, "end": v(-5.78, 44.03) * mm});
            skLineSegment(sketch, "E2617", {"start": v(-5.78, 44.03) * mm, "end": v(-5.73, 44.03) * mm});
            skLineSegment(sketch, "E2618", {"start": v(-5.73, 44.03) * mm, "end": v(-5.67, 44.03) * mm});
            skLineSegment(sketch, "E2619", {"start": v(-5.67, 44.03) * mm, "end": v(-5.63, 44.02) * mm});
            skLineSegment(sketch, "E2620", {"start": v(-5.63, 44.02) * mm, "end": v(-5.6, 44) * mm});
            skLineSegment(sketch, "E2621", {"start": v(-5.6, 44) * mm, "end": v(-5.56, 44) * mm});
            skLineSegment(sketch, "E2622", {"start": v(-5.56, 44) * mm, "end": v(-5.53, 43.97) * mm});
            skLineSegment(sketch, "E2623", {"start": v(-5.53, 43.97) * mm, "end": v(-5.5, 43.94) * mm});
            skLineSegment(sketch, "E2624", {"start": v(-5.5, 43.94) * mm, "end": v(-5.47, 43.9) * mm});
            skLineSegment(sketch, "E2625", {"start": v(-5.47, 43.9) * mm, "end": v(-5.45, 43.87) * mm});
            skLineSegment(sketch, "E2626", {"start": v(-5.45, 43.87) * mm, "end": v(-5.43, 43.84) * mm});
            skLineSegment(sketch, "E2627", {"start": v(-5.43, 43.84) * mm, "end": v(-5.42, 43.8) * mm});
            skLineSegment(sketch, "E2628", {"start": v(-5.42, 43.8) * mm, "end": v(-5.41, 43.77) * mm});
            skLineSegment(sketch, "E2629", {"start": v(-5.41, 43.77) * mm, "end": v(-5.4, 43.74) * mm});
            skLineSegment(sketch, "E2630", {"start": v(-5.4, 43.74) * mm, "end": v(-5.41, 43.7) * mm});
            skLineSegment(sketch, "E2631", {"start": v(-5.41, 43.7) * mm, "end": v(-5.42, 43.66) * mm});
            skLineSegment(sketch, "E2632", {"start": v(-5.42, 43.66) * mm, "end": v(-5.43, 43.63) * mm});
            skLineSegment(sketch, "E2633", {"start": v(-5.43, 43.63) * mm, "end": v(-5.44, 43.59) * mm});
            skLineSegment(sketch, "E2634", {"start": v(-5.44, 43.59) * mm, "end": v(-5.48, 43.5) * mm});
            skLineSegment(sketch, "E2635", {"start": v(-5.48, 43.5) * mm, "end": v(-5.5, 43.46) * mm});
            skLineSegment(sketch, "E2636", {"start": v(-5.5, 43.46) * mm, "end": v(-7.45, 41.52) * mm});
            skLineSegment(sketch, "E2637", {"start": v(-7.45, 41.52) * mm, "end": v(-7.45, 41.51) * mm});
            skLineSegment(sketch, "E2638", {"start": v(-7.45, 41.51) * mm, "end": v(0.14, 41.51) * mm});
            skLineSegment(sketch, "E2639", {"start": v(-14, 68.85) * mm, "end": v(-14, 40.85) * mm});
            skLineSegment(sketch, "E2640", {"start": v(-14, 40.85) * mm, "end": v(14, 40.85) * mm});
            skLineSegment(sketch, "E2641", {"start": v(14, 40.85) * mm, "end": v(14, 68.85) * mm});
            skLineSegment(sketch, "E2642", {"start": v(14, 68.85) * mm, "end": v(-14, 68.85) * mm});
            skSolve(sketch);
        }
        {
            var Q0;
            Q0=makeQuery(id+"F10.imprint","IMPRINT",FACE,{"disambiguationData":[TD([[makeQuery(id+"F10.imprint","IMPRINT",EDGE,{"derivedFrom":sQuery(id+"F10.wireOp",EDGE,"E14")}),-1.0]])]});
            var Q1;
            Q1=makeQuery(id+"F10.imprint","IMPRINT",FACE,{"disambiguationData":[TD([[makeQuery(id+"F10.imprint","IMPRINT",EDGE,{"derivedFrom":sQuery(id+"F10.wireOp",EDGE,"E347")}),-1.0]])]});
            var Q2;
            Q2=makeQuery(id+"F10.imprint","IMPRINT",FACE,{"disambiguationData":[TD([[makeQuery(id+"F10.imprint","IMPRINT",EDGE,{"derivedFrom":sQuery(id+"F10.wireOp",EDGE,"E899")}),-1.0]])]});
            var Q3;
            Q3=makeQuery(id+"F10.imprint","IMPRINT",FACE,{"disambiguationData":[TD([[makeQuery(id+"F10.imprint","IMPRINT",EDGE,{"derivedFrom":sQuery(id+"F10.wireOp",EDGE,"E1043")}),1.0]])]});
            var Q4;
            Q4=makeQuery(id+"F10.imprint","IMPRINT",FACE,{"disambiguationData":[TD([[makeQuery(id+"F10.imprint","IMPRINT",EDGE,{"derivedFrom":sQuery(id+"F10.wireOp",EDGE,"E138")}),1.0]])]});
            var Q5;
            Q5=makeQuery(id+"F10.imprint","IMPRINT",FACE,{"disambiguationData":[TD([[makeQuery(id+"F10.imprint","IMPRINT",EDGE,{"derivedFrom":sQuery(id+"F10.wireOp",EDGE,"E348")}),1.0]])]});
            var Q6;
            Q6=makeQuery(id+"F10.imprint","IMPRINT",FACE,{"disambiguationData":[TD([[makeQuery(id+"F10.imprint","IMPRINT",EDGE,{"derivedFrom":sQuery(id+"F10.wireOp",EDGE,"E17")}),1.0]])]});
            var Q7;
            Q7=makeQuery(id+"F10.imprint","IMPRINT",FACE,{"disambiguationData":[TD([[makeQuery(id+"F10.imprint","IMPRINT",EDGE,{"derivedFrom":sQuery(id+"F10.wireOp",EDGE,"E51")}),-1.0]])]});
            var Q8;
            Q8=makeQuery(id+"F10.imprint","IMPRINT",FACE,{"disambiguationData":[TD([[makeQuery(id+"F10.imprint","IMPRINT",EDGE,{"derivedFrom":sQuery(id+"F10.wireOp",EDGE,"E1473")}),1.0]])]});
            var Q9;
            Q9=makeQuery(id+"F10.imprint","IMPRINT",FACE,{"disambiguationData":[TD([[makeQuery(id+"F10.imprint","IMPRINT",EDGE,{"derivedFrom":sQuery(id+"F10.wireOp",EDGE,"E1185")}),1.0]])]});
            var Q10;
            Q10=makeQuery(id+"F10.imprint","IMPRINT",FACE,{"disambiguationData":[TD([[makeQuery(id+"F10.imprint","IMPRINT",EDGE,{"derivedFrom":sQuery(id+"F10.wireOp",EDGE,"E722")}),1.0]])]});
            var Q11;
            Q11=makeQuery(id+"F10.imprint","IMPRINT",FACE,{"disambiguationData":[TD([[makeQuery(id+"F10.imprint","IMPRINT",EDGE,{"derivedFrom":sQuery(id+"F10.wireOp",EDGE,"E545")}),1.0]])]});
            var Q12;
            Q12=makeQuery(id+"F10.imprint","IMPRINT",FACE,{"disambiguationData":[TD([[makeQuery(id+"F10.imprint","IMPRINT",EDGE,{"derivedFrom":sQuery(id+"F10.wireOp",EDGE,"E682")}),1.0]])]});
            var Q13;
            Q13=makeQuery(id+"F10.imprint","IMPRINT",FACE,{"disambiguationData":[TD([[makeQuery(id+"F10.imprint","IMPRINT",EDGE,{"derivedFrom":sQuery(id+"F10.wireOp",EDGE,"E622")}),1.0]])]});
            var Q14;
            Q14=makeQuery(id+"F10.imprint","IMPRINT",FACE,{"disambiguationData":[TD([[makeQuery(id+"F10.imprint","IMPRINT",EDGE,{"derivedFrom":sQuery(id+"F10.wireOp",EDGE,"E311")}),1.0]])]});
            var Q15;
            Q15=makeQuery(id+"F10.imprint","IMPRINT",FACE,{"disambiguationData":[TD([[makeQuery(id+"F10.imprint","IMPRINT",EDGE,{"derivedFrom":sQuery(id+"F10.wireOp",EDGE,"E1390")}),1.0]])]});
            var Q16;
            Q16=makeQuery(id+"F10.imprint","IMPRINT",FACE,{"disambiguationData":[TD([[makeQuery(id+"F10.imprint","IMPRINT",EDGE,{"derivedFrom":sQuery(id+"F10.wireOp",EDGE,"E1346")}),-1.0]])]});
            var Q17;
            Q17=makeQuery(id+"F10.imprint","IMPRINT",FACE,{"disambiguationData":[TD([[makeQuery(id+"F10.imprint","IMPRINT",EDGE,{"derivedFrom":sQuery(id+"F10.wireOp",EDGE,"E1677")}),-1.0]])]});
            var Q18;
            Q18=makeQuery(id+"F10.imprint","IMPRINT",FACE,{"disambiguationData":[TD([[makeQuery(id+"F10.imprint","IMPRINT",EDGE,{"derivedFrom":sQuery(id+"F10.wireOp",EDGE,"E1341")}),-1.0]])]});
            var Q19;
            Q19=makeQuery(id+"F10.imprint","IMPRINT",FACE,{"disambiguationData":[TD([[makeQuery(id+"F10.imprint","IMPRINT",EDGE,{"derivedFrom":sQuery(id+"F10.wireOp",EDGE,"E1350")}),1.0]])]});
            var Q20;
            Q20=makeQuery(id+"F10.imprint","IMPRINT",FACE,{"disambiguationData":[TD([[makeQuery(id+"F10.imprint","IMPRINT",EDGE,{"derivedFrom":sQuery(id+"F10.wireOp",EDGE,"E1645")}),1.0]])]});
            var Q21;
            Q21=makeQuery(id+"F10.imprint","IMPRINT",FACE,{"disambiguationData":[TD([[makeQuery(id+"F10.imprint","IMPRINT",EDGE,{"derivedFrom":sQuery(id+"F10.wireOp",EDGE,"E1683")}),1.0]])]});
            var Q22;
            Q22=makeQuery(id+"F10.imprint","IMPRINT",FACE,{"disambiguationData":[TD([[makeQuery(id+"F10.imprint","IMPRINT",EDGE,{"derivedFrom":sQuery(id+"F10.wireOp",EDGE,"E1558")}),1.0]])]});
            var Q23;
            Q23=makeQuery(id+"F10.imprint","IMPRINT",FACE,{"disambiguationData":[TD([[makeQuery(id+"F10.imprint","IMPRINT",EDGE,{"derivedFrom":sQuery(id+"F10.wireOp",EDGE,"E1967")}),1.0]])]});
            var Q24;
            Q24=makeQuery(id+"F10.imprint","IMPRINT",FACE,{"disambiguationData":[TD([[makeQuery(id+"F10.imprint","IMPRINT",EDGE,{"derivedFrom":sQuery(id+"F10.wireOp",EDGE,"E1802")}),1.0]])]});
            var Q25;
            Q25=makeQuery(id+"F10.imprint","IMPRINT",FACE,{"disambiguationData":[TD([[makeQuery(id+"F10.imprint","IMPRINT",EDGE,{"derivedFrom":sQuery(id+"F10.wireOp",EDGE,"E1939")}),1.0]])]});
            var Q26;
            Q26=makeQuery(id+"F10.imprint","IMPRINT",FACE,{"disambiguationData":[TD([[makeQuery(id+"F10.imprint","IMPRINT",EDGE,{"derivedFrom":sQuery(id+"F10.wireOp",EDGE,"E1767")}),1.0]])]});
            var Q27;
            Q27=makeQuery(id+"F10.imprint","IMPRINT",FACE,{"disambiguationData":[TD([[makeQuery(id+"F10.imprint","IMPRINT",EDGE,{"derivedFrom":sQuery(id+"F10.wireOp",EDGE,"E1854")}),1.0]])]});
            var Q28;
            Q28=makeQuery(id+"F1.opRevolve","SWEPT_FACE",FACE,{"disambiguationData":[OSD([sQuery(id+"F0.wireOp",EDGE,"E1")])]});
            extrude(context, id + "F11", {"entities" : qUnion([Q0, Q1, Q2, Q3, Q4, Q5, Q6, Q7, Q8, Q9, Q10, Q11, Q12, Q13, Q14, Q15, Q16, Q17, Q18, Q19, Q20, Q21, Q22, Q23, Q24, Q25, Q26, Q27]), "operationType" : NewBodyOperationType.ADD, "endBound" : BoundingType.UP_TO_SURFACE, "oppositeDirection" : true, "depth" : 25 * mm, "endBoundEntityFace" : qUnion([Q28]), "offsetDistance" : 25 * mm});
        }
        {
            var Q0;
            Q0=makeQuery(id+"F1.opRevolve","SWEPT_FACE",FACE,{"disambiguationData":[OSD([sQuery(id+"F0.wireOp",EDGE,"E0")])]});
            var sketch = newSketch(context, id + "F12", { "sketchPlane" : qUnion([Q0])});
            skCircle(sketch, "E2643", {"center": v(0, 0) * mm, "radius": 54.75 * mm});
            skCircle(sketch, "E2644", {"center": v(0, 0) * mm, "radius": 100 * mm});
            skSolve(sketch);
        }
        {
            var Q0;
            Q0=qSketchRegion(id+"F12",true);
            extrude(context, id + "F13", {"entities" : qUnion([Q0]), "operationType" : NewBodyOperationType.REMOVE, "oppositeDirection" : true, "depth" : 124 * mm});
        }
    });
